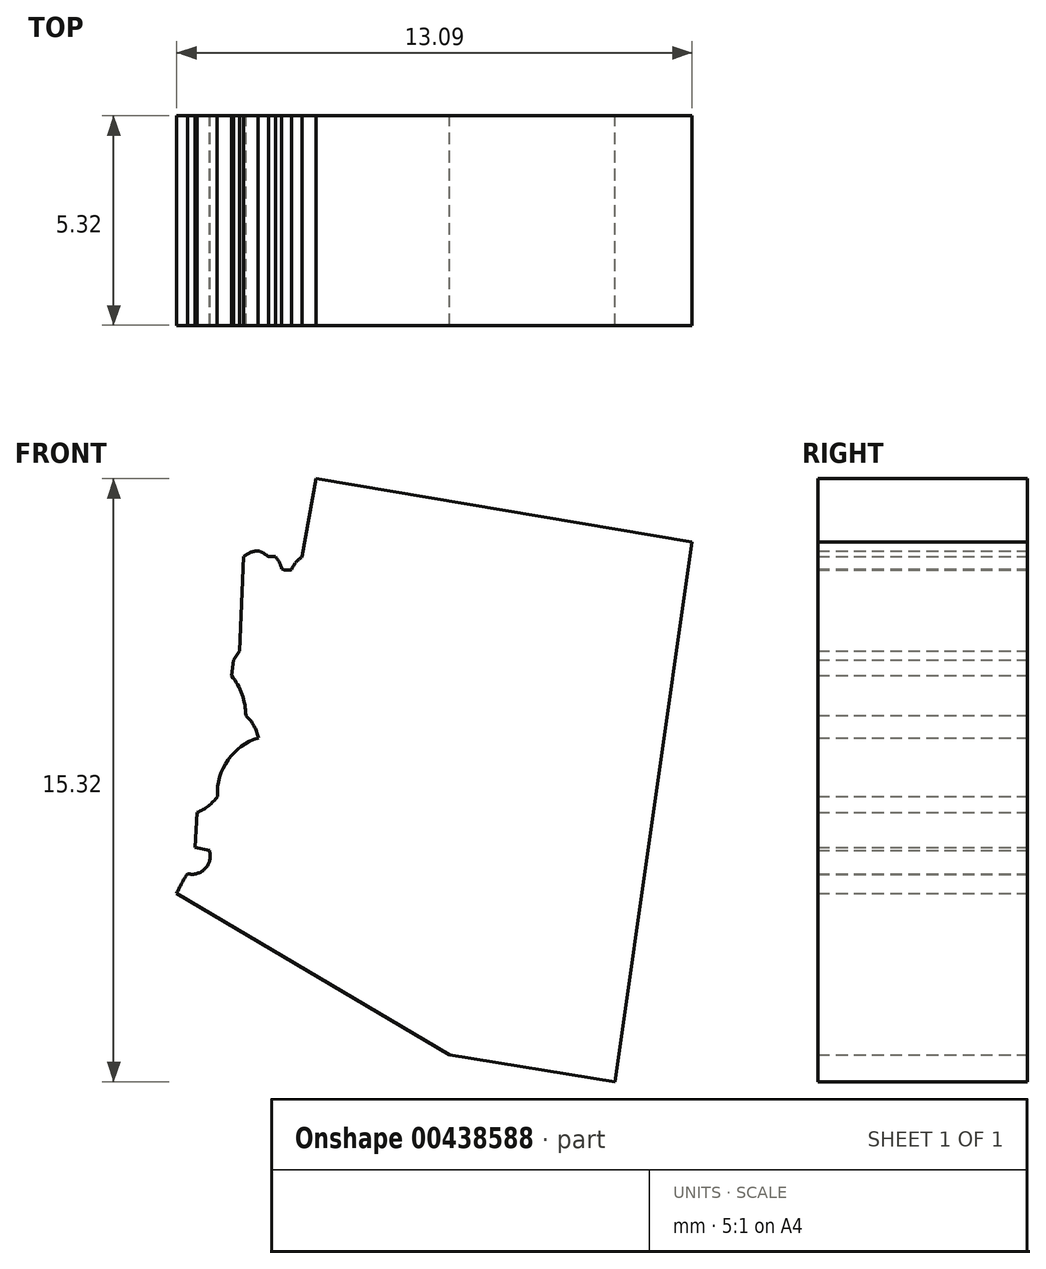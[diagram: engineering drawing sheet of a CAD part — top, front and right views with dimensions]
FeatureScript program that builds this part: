
annotation { "Feature Type Name" : "Feature", "Feature Type Description" : "" }
export const myFeature = defineFeature(function(context is Context, id is Id, definition is map)
    precondition{}
    {
        {
            var Q0;
            Q0=qCreatedBy(makeId("Front.planeOp"),FACE);
            var sketch = newSketch(context, id + "F0", { "sketchPlane" : qUnion([Q0])});
            skLineSegment(sketch, "E0", {"start": v(-91.2, -20.47) * mm, "end": v(-91.4, -20.34) * mm});
            skLineSegment(sketch, "E1", {"start": v(-91.4, -20.34) * mm, "end": v(-91.23, -19.86) * mm});
            skLineSegment(sketch, "E2", {"start": v(-91.47, -19.54) * mm, "end": v(-91.23, -19.86) * mm});
            skLineSegment(sketch, "E3", {"start": v(-91.47, -19.54) * mm, "end": v(-91.79, -19.4) * mm});
            skArc(sketch, "E4", {"start": v(-92.56, -18.19) * mm, "mid": v(-92.2, -18.82) * mm, "end": v(-91.79, -19.4) * mm});
            skArc(sketch, "E5", {"start": v(-93, -17.9) * mm, "mid": v(-92.78, -18.05) * mm, "end": v(-92.56, -18.19) * mm});
            skArc(sketch, "E6", {"start": v(-93, -17.65) * mm, "mid": v(-93, -17.78) * mm, "end": v(-93, -17.9) * mm});
            skArc(sketch, "E7", {"start": v(-93.6, -16.32) * mm, "mid": v(-93.31, -17) * mm, "end": v(-93, -17.65) * mm});
            skArc(sketch, "E8", {"start": v(-93.68, -15.85) * mm, "mid": v(-93.78, -15.74) * mm, "end": v(-93.9, -15.65) * mm});
            skArc(sketch, "E9", {"start": v(-93.68, -15.85) * mm, "mid": v(-93.64, -16.09) * mm, "end": v(-93.6, -16.32) * mm});
            skLineSegment(sketch, "E10", {"start": v(-107.57, 14.71) * mm, "end": v(-108.8, 4.95) * mm});
            skLineSegment(sketch, "E11", {"start": v(-94.83, 13.4) * mm, "end": v(-94.98, 10.98) * mm});
            skLineSegment(sketch, "E12", {"start": v(-116.05, 18.58) * mm, "end": v(-110.83, 17.66) * mm});
            skLineSegment(sketch, "E13", {"start": v(-110.83, 17.66) * mm, "end": v(-111.12, 15.24) * mm});
            skLineSegment(sketch, "E14", {"start": v(-111.12, 15.24) * mm, "end": v(-107.57, 14.71) * mm});
            skLineSegment(sketch, "E15", {"start": v(-118.36, 6.55) * mm, "end": v(-116.05, 18.58) * mm});
            skArc(sketch, "E16", {"start": v(-133.74, 23) * mm, "mid": v(-124.97, 20.48) * mm, "end": v(-116.05, 18.58) * mm});
            skLineSegment(sketch, "E17", {"start": v(-128.43, 13.81) * mm, "end": v(-126.5, 20.87) * mm});
            skLineSegment(sketch, "E18", {"start": v(-128.43, 13.81) * mm, "end": v(-120.45, 1.94) * mm});
            skLineSegment(sketch, "E19", {"start": v(-110.83, 17.66) * mm, "end": v(-109.56, 24.9) * mm});
            skLineSegment(sketch, "E20", {"start": v(-97.69, 23.43) * mm, "end": v(-109.56, 24.9) * mm});
            skLineSegment(sketch, "E21", {"start": v(-110.76, -8.77) * mm, "end": v(-108.8, 4.95) * mm});
            skLineSegment(sketch, "E22", {"start": v(-98.28, -8.44) * mm, "end": v(-97.44, 2.44) * mm});
            skLineSegment(sketch, "E23", {"start": v(-97.44, 2.44) * mm, "end": v(-97.32, 2.43) * mm});
            skLineSegment(sketch, "E24", {"start": v(-97.32, 2.43) * mm, "end": v(-97.23, 3.7) * mm});
            skLineSegment(sketch, "E25", {"start": v(-110.76, -8.77) * mm, "end": v(-109.06, -9.01) * mm});
            skLineSegment(sketch, "E26", {"start": v(-109.06, -9.01) * mm, "end": v(-108.94, -7.87) * mm});
            skLineSegment(sketch, "E27", {"start": v(-108.94, -7.87) * mm, "end": v(-105.63, -8.33) * mm});
            skLineSegment(sketch, "E28", {"start": v(-105.63, -8.33) * mm, "end": v(-105.63, -7.87) * mm});
            skLineSegment(sketch, "E29", {"start": v(-105.63, -7.87) * mm, "end": v(-98.28, -8.44) * mm});
            skLineSegment(sketch, "E30", {"start": v(-121.9, -3.98) * mm, "end": v(-114.96, -8.09) * mm});
            skLineSegment(sketch, "E31", {"start": v(-114.96, -8.09) * mm, "end": v(-110.76, -8.77) * mm});
            skArc(sketch, "E32", {"start": v(-97.32, 2.43) * mm, "mid": v(-94.44, 2.26) * mm, "end": v(-91.56, 2.2) * mm});
            skArc(sketch, "E33", {"start": v(-91.56, 2.2) * mm, "mid": v(-91.66, -0.16) * mm, "end": v(-91.72, -2.53) * mm});
            skArc(sketch, "E34", {"start": v(-126.53, 38.65) * mm, "mid": v(-104.72, 33.96) * mm, "end": v(-82.45, 32.53) * mm});
            skLineSegment(sketch, "E35", {"start": v(-97.69, 23.43) * mm, "end": v(-96.93, 33.08) * mm});
            skLineSegment(sketch, "E36", {"start": v(-98.07, 18.57) * mm, "end": v(-88.38, 18.08) * mm});
            skLineSegment(sketch, "E37", {"start": v(-94.98, 10.98) * mm, "end": v(-82.57, 10.6) * mm});
            skArc(sketch, "E38", {"start": v(-84.8, 19.22) * mm, "mid": v(-80.14, 19.27) * mm, "end": v(-75.47, 19.43) * mm});
            skArc(sketch, "E39", {"start": v(-83.28, 12.1) * mm, "mid": v(-79.64, 12.16) * mm, "end": v(-76, 12.3) * mm});
            skArc(sketch, "E40", {"start": v(-74.23, 17.12) * mm, "mid": v(-71.76, 17.15) * mm, "end": v(-69.3, 17.4) * mm});
            skLineSegment(sketch, "E41", {"start": v(-67.28, 15.71) * mm, "end": v(-63.63, 16.12) * mm});
            skLineSegment(sketch, "E42", {"start": v(-63.63, 16.12) * mm, "end": v(-62.92, 9.59) * mm});
            skLineSegment(sketch, "E43", {"start": v(-63.62, 15.96) * mm, "end": v(-61.24, 16.34) * mm});
            skLineSegment(sketch, "E44", {"start": v(-54.85, 18.69) * mm, "end": v(-54.78, 18) * mm});
            skLineSegment(sketch, "E45", {"start": v(-54.78, 18) * mm, "end": v(-47.02, 19.57) * mm});
            skLineSegment(sketch, "E46", {"start": v(-81.2, 3.21) * mm, "end": v(-81.2, 2.02) * mm});
            skLineSegment(sketch, "E47", {"start": v(-81.2, 2.02) * mm, "end": v(-72.53, 2.3) * mm});
            skArc(sketch, "E48", {"start": v(-81.2, 3.21) * mm, "mid": v(-81.15, 5.87) * mm, "end": v(-81.29, 8.53) * mm});
            skArc(sketch, "E49", {"start": v(-117.53, 36.3) * mm, "mid": v(-118.42, 32.77) * mm, "end": v(-119.02, 29.18) * mm});
            skArc(sketch, "E50", {"start": v(-68.32, 3.05) * mm, "mid": v(-56.66, 4.2) * mm, "end": v(-45.14, 6.29) * mm});
            skLineSegment(sketch, "E51", {"start": v(-71.32, 2.46) * mm, "end": v(-68.36, 2.6) * mm});
            skLineSegment(sketch, "E52", {"start": v(-68.36, 2.6) * mm, "end": v(-68.32, 3.05) * mm});
            skArc(sketch, "E53", {"start": v(-72.5, -1.3) * mm, "mid": v(-65.46, -0.82) * mm, "end": v(-58.46, 0.03) * mm});
            skLineSegment(sketch, "E54", {"start": v(-79.86, -6.45) * mm, "end": v(-73.99, -6.34) * mm});
            skLineSegment(sketch, "E55", {"start": v(-120.45, 1.94) * mm, "end": v(-120.3, 2.17) * mm});
            skLineSegment(sketch, "E56", {"start": v(-120.3, 2.17) * mm, "end": v(-120.2, 4.57) * mm});
            skArc(sketch, "E57", {"start": v(-119.83, 4.72) * mm, "mid": v(-120.02, 4.67) * mm, "end": v(-120.2, 4.57) * mm});
            skArc(sketch, "E58", {"start": v(-119.56, 4.57) * mm, "mid": v(-119.69, 4.66) * mm, "end": v(-119.83, 4.72) * mm});
            skArc(sketch, "E59", {"start": v(-119.38, 4.57) * mm, "mid": v(-119.47, 4.57) * mm, "end": v(-119.56, 4.57) * mm});
            skArc(sketch, "E60", {"start": v(-118.7, 4.57) * mm, "mid": v(-118.87, 4.42) * mm, "end": v(-118.98, 4.24) * mm});
            skArc(sketch, "E61", {"start": v(-119.22, 4.26) * mm, "mid": v(-119.28, 4.42) * mm, "end": v(-119.38, 4.57) * mm});
            skArc(sketch, "E62", {"start": v(-119.22, 4.26) * mm, "mid": v(-119.1, 4.22) * mm, "end": v(-118.98, 4.24) * mm});
            skLineSegment(sketch, "E63", {"start": v(-118.7, 4.57) * mm, "end": v(-118.36, 6.55) * mm});
            skArc(sketch, "E64", {"start": v(-126.62, -2.8) * mm, "mid": v(-124.12, -3.18) * mm, "end": v(-121.62, -3.49) * mm});
            skArc(sketch, "E65", {"start": v(-121.62, -3.49) * mm, "mid": v(-121.76, -3.73) * mm, "end": v(-121.9, -3.98) * mm});
            skLineSegment(sketch, "E66", {"start": v(-126.67, -1.34) * mm, "end": v(-126.62, -2.8) * mm});
            skLineSegment(sketch, "E67", {"start": v(-126.67, -1.34) * mm, "end": v(-127.1, -0.55) * mm});
            skLineSegment(sketch, "E68", {"start": v(-127.1, -0.55) * mm, "end": v(-127.33, -0.33) * mm});
            skLineSegment(sketch, "E69", {"start": v(-127.33, -0.33) * mm, "end": v(-127.8, 0.37) * mm});
            skLineSegment(sketch, "E70", {"start": v(-127.8, 0.37) * mm, "end": v(-128.45, 0.48) * mm});
            skLineSegment(sketch, "E71", {"start": v(-128.45, 0.48) * mm, "end": v(-128.45, 0.61) * mm});
            skLineSegment(sketch, "E72", {"start": v(-128.45, 0.61) * mm, "end": v(-128.35, 0.68) * mm});
            skLineSegment(sketch, "E73", {"start": v(-128.35, 0.68) * mm, "end": v(-128.39, 1) * mm});
            skLineSegment(sketch, "E74", {"start": v(-128.39, 1) * mm, "end": v(-128.54, 1.24) * mm});
            skLineSegment(sketch, "E75", {"start": v(-128.54, 1.24) * mm, "end": v(-129.08, 1.34) * mm});
            skLineSegment(sketch, "E76", {"start": v(-129.08, 1.34) * mm, "end": v(-129.48, 1.55) * mm});
            skLineSegment(sketch, "E77", {"start": v(-129.48, 1.55) * mm, "end": v(-129.9, 2.3) * mm});
            skLineSegment(sketch, "E78", {"start": v(-129.9, 2.3) * mm, "end": v(-130.24, 2.7) * mm});
            skLineSegment(sketch, "E79", {"start": v(-130.24, 2.7) * mm, "end": v(-130.64, 2.74) * mm});
            skLineSegment(sketch, "E80", {"start": v(-130.64, 2.74) * mm, "end": v(-131.5, 3.16) * mm});
            skLineSegment(sketch, "E81", {"start": v(-131.5, 3.16) * mm, "end": v(-131.93, 3.2) * mm});
            skLineSegment(sketch, "E82", {"start": v(-131.93, 3.2) * mm, "end": v(-132.23, 3.5) * mm});
            skLineSegment(sketch, "E83", {"start": v(-132.23, 3.5) * mm, "end": v(-131.93, 4.74) * mm});
            skLineSegment(sketch, "E84", {"start": v(-131.93, 4.74) * mm, "end": v(-131.93, 4.98) * mm});
            skLineSegment(sketch, "E85", {"start": v(-131.93, 4.98) * mm, "end": v(-132.1, 5.14) * mm});
            skLineSegment(sketch, "E86", {"start": v(-132.1, 5.14) * mm, "end": v(-132.1, 5.4) * mm});
            skLineSegment(sketch, "E87", {"start": v(-132.1, 5.4) * mm, "end": v(-132.68, 6.4) * mm});
            skLineSegment(sketch, "E88", {"start": v(-132.68, 6.4) * mm, "end": v(-133.14, 7.78) * mm});
            skLineSegment(sketch, "E89", {"start": v(-133.14, 7.78) * mm, "end": v(-133.45, 8.25) * mm});
            skLineSegment(sketch, "E90", {"start": v(-133.45, 8.25) * mm, "end": v(-133.55, 8.54) * mm});
            skLineSegment(sketch, "E91", {"start": v(-133.55, 8.54) * mm, "end": v(-133.49, 9.04) * mm});
            skArc(sketch, "E92", {"start": v(-133.49, 9.04) * mm, "mid": v(-133.08, 9.38) * mm, "end": v(-133.11, 9.91) * mm});
            skLineSegment(sketch, "E93", {"start": v(-133.11, 9.91) * mm, "end": v(-133.38, 9.97) * mm});
            skLineSegment(sketch, "E94", {"start": v(-133.38, 9.97) * mm, "end": v(-133.86, 10.65) * mm});
            skLineSegment(sketch, "E95", {"start": v(-133.86, 10.65) * mm, "end": v(-133.86, 11.63) * mm});
            skLineSegment(sketch, "E96", {"start": v(-133.86, 11.63) * mm, "end": v(-133.7, 12.33) * mm});
            skLineSegment(sketch, "E97", {"start": v(-133.7, 12.33) * mm, "end": v(-134.3, 13.03) * mm});
            skLineSegment(sketch, "E98", {"start": v(-134.3, 13.03) * mm, "end": v(-134.3, 13.29) * mm});
            skArc(sketch, "E99", {"start": v(-134.3, 13.29) * mm, "mid": v(-134.27, 13.76) * mm, "end": v(-134.42, 14.22) * mm});
            skLineSegment(sketch, "E100", {"start": v(-135.13, 15.58) * mm, "end": v(-134.42, 14.22) * mm});
            skLineSegment(sketch, "E101", {"start": v(-135.13, 15.58) * mm, "end": v(-135.01, 16) * mm});
            skLineSegment(sketch, "E102", {"start": v(-135.01, 16) * mm, "end": v(-134.96, 16.65) * mm});
            skLineSegment(sketch, "E103", {"start": v(-134.96, 16.65) * mm, "end": v(-134.76, 16.97) * mm});
            skLineSegment(sketch, "E104", {"start": v(-134.76, 16.97) * mm, "end": v(-134.73, 17.77) * mm});
            skLineSegment(sketch, "E105", {"start": v(-134.73, 17.77) * mm, "end": v(-135.01, 18.6) * mm});
            skLineSegment(sketch, "E106", {"start": v(-135.01, 18.6) * mm, "end": v(-135.32, 19.01) * mm});
            skLineSegment(sketch, "E107", {"start": v(-135.32, 19.01) * mm, "end": v(-135.07, 19.88) * mm});
            skLineSegment(sketch, "E108", {"start": v(-135.07, 19.88) * mm, "end": v(-134.88, 19.94) * mm});
            skLineSegment(sketch, "E109", {"start": v(-134.88, 19.94) * mm, "end": v(-134.84, 20.1) * mm});
            skLineSegment(sketch, "E110", {"start": v(-134.84, 20.1) * mm, "end": v(-134.5, 20.4) * mm});
            skLineSegment(sketch, "E111", {"start": v(-134.5, 20.4) * mm, "end": v(-133.92, 21.67) * mm});
            skLineSegment(sketch, "E112", {"start": v(-133.92, 21.67) * mm, "end": v(-133.92, 22.51) * mm});
            skLineSegment(sketch, "E113", {"start": v(-133.92, 22.51) * mm, "end": v(-133.74, 23) * mm});
            skArc(sketch, "E114", {"start": v(-120.14, 0.53) * mm, "mid": v(-120.23, 1.07) * mm, "end": v(-120.5, 1.55) * mm});
            skLineSegment(sketch, "E115", {"start": v(-120.45, 1.94) * mm, "end": v(-120.5, 1.55) * mm});
            skArc(sketch, "E116", {"start": v(-121.62, -3.49) * mm, "mid": v(-121.17, -3.36) * mm, "end": v(-121.06, -2.9) * mm});
            skLineSegment(sketch, "E117", {"start": v(-121.06, -2.9) * mm, "end": v(-121.42, -2.81) * mm});
            skLineSegment(sketch, "E118", {"start": v(-121.42, -2.81) * mm, "end": v(-121.38, -1.93) * mm});
            skArc(sketch, "E119", {"start": v(-121.38, -1.93) * mm, "mid": v(-121.09, -1.76) * mm, "end": v(-120.86, -1.52) * mm});
            skArc(sketch, "E120", {"start": v(-119.82, -0.04) * mm, "mid": v(-120.6, -0.6) * mm, "end": v(-120.86, -1.52) * mm});
            skArc(sketch, "E121", {"start": v(-119.82, -0.04) * mm, "mid": v(-119.93, 0.27) * mm, "end": v(-120.14, 0.53) * mm});
            skLineSegment(sketch, "E122", {"start": v(-121.32, 19.62) * mm, "end": v(-120.3, 24) * mm});
            skLineSegment(sketch, "E123", {"start": v(-120.3, 24) * mm, "end": v(-119.9, 24.82) * mm});
            skLineSegment(sketch, "E124", {"start": v(-119.9, 24.82) * mm, "end": v(-120.03, 25.08) * mm});
            skLineSegment(sketch, "E125", {"start": v(-120.03, 25.08) * mm, "end": v(-120.34, 25.15) * mm});
            skLineSegment(sketch, "E126", {"start": v(-119.02, 29.18) * mm, "end": v(-122.2, 30.03) * mm});
            skLineSegment(sketch, "E127", {"start": v(-122.2, 30.03) * mm, "end": v(-123.9, 30.03) * mm});
            skLineSegment(sketch, "E128", {"start": v(-123.9, 30.03) * mm, "end": v(-123.9, 30.16) * mm});
            skLineSegment(sketch, "E129", {"start": v(-123.9, 30.16) * mm, "end": v(-124.46, 29.94) * mm});
            skLineSegment(sketch, "E130", {"start": v(-124.46, 29.94) * mm, "end": v(-124.94, 29.94) * mm});
            skLineSegment(sketch, "E131", {"start": v(-124.94, 29.94) * mm, "end": v(-125.28, 30.18) * mm});
            skLineSegment(sketch, "E132", {"start": v(-125.28, 30.18) * mm, "end": v(-125.42, 30.1) * mm});
            skLineSegment(sketch, "E133", {"start": v(-125.42, 30.1) * mm, "end": v(-125.92, 30.1) * mm});
            skArc(sketch, "E134", {"start": v(-125.92, 30.1) * mm, "mid": v(-126.57, 30.42) * mm, "end": v(-127.28, 30.62) * mm});
            skArc(sketch, "E135", {"start": v(-128.83, 30.92) * mm, "mid": v(-128.11, 30.47) * mm, "end": v(-127.28, 30.62) * mm});
            skArc(sketch, "E136", {"start": v(-128.83, 30.92) * mm, "mid": v(-128.7, 31.65) * mm, "end": v(-129.02, 32.33) * mm});
            skLineSegment(sketch, "E137", {"start": v(-129.02, 32.33) * mm, "end": v(-129.43, 32.33) * mm});
            skLineSegment(sketch, "E138", {"start": v(-129.43, 32.33) * mm, "end": v(-129.43, 32.63) * mm});
            skLineSegment(sketch, "E139", {"start": v(-129.43, 32.63) * mm, "end": v(-129.68, 32.63) * mm});
            skLineSegment(sketch, "E140", {"start": v(-129.68, 32.63) * mm, "end": v(-129.98, 32.86) * mm});
            skLineSegment(sketch, "E141", {"start": v(-129.98, 32.86) * mm, "end": v(-130.16, 32.79) * mm});
            skLineSegment(sketch, "E142", {"start": v(-130.16, 32.79) * mm, "end": v(-130.42, 33.08) * mm});
            skLineSegment(sketch, "E143", {"start": v(-130.42, 33.08) * mm, "end": v(-130.38, 33.4) * mm});
            skLineSegment(sketch, "E144", {"start": v(-130.38, 33.4) * mm, "end": v(-130.1, 33.4) * mm});
            skLineSegment(sketch, "E145", {"start": v(-130.1, 33.4) * mm, "end": v(-129.92, 33.88) * mm});
            skLineSegment(sketch, "E146", {"start": v(-129.92, 33.88) * mm, "end": v(-130.2, 34.03) * mm});
            skLineSegment(sketch, "E147", {"start": v(-130.2, 34.03) * mm, "end": v(-130.15, 34.42) * mm});
            skLineSegment(sketch, "E148", {"start": v(-130.15, 34.42) * mm, "end": v(-129.65, 34.47) * mm});
            skLineSegment(sketch, "E149", {"start": v(-129.65, 34.47) * mm, "end": v(-130, 34.82) * mm});
            skLineSegment(sketch, "E150", {"start": v(-130, 34.82) * mm, "end": v(-130.15, 35.59) * mm});
            skLineSegment(sketch, "E151", {"start": v(-130.15, 35.59) * mm, "end": v(-130.08, 35.84) * mm});
            skLineSegment(sketch, "E152", {"start": v(-130.08, 35.84) * mm, "end": v(-130.08, 36.79) * mm});
            skLineSegment(sketch, "E153", {"start": v(-130.08, 36.79) * mm, "end": v(-130.26, 37.1) * mm});
            skLineSegment(sketch, "E154", {"start": v(-130.26, 37.1) * mm, "end": v(-130.26, 37.29) * mm});
            skLineSegment(sketch, "E155", {"start": v(-130.26, 37.29) * mm, "end": v(-130.06, 38.16) * mm});
            skLineSegment(sketch, "E156", {"start": v(-130.06, 38.16) * mm, "end": v(-129.8, 38.13) * mm});
            skArc(sketch, "E157", {"start": v(-129.8, 38.13) * mm, "mid": v(-128.59, 37.18) * mm, "end": v(-127.1, 36.73) * mm});
            skArc(sketch, "E158", {"start": v(-126.56, 36.06) * mm, "mid": v(-126.72, 36.48) * mm, "end": v(-127.1, 36.73) * mm});
            skArc(sketch, "E159", {"start": v(-126.43, 36.88) * mm, "mid": v(-126.52, 36.55) * mm, "end": v(-126.36, 36.24) * mm});
            skArc(sketch, "E160", {"start": v(-126.32, 37.66) * mm, "mid": v(-126.5, 37.29) * mm, "end": v(-126.43, 36.88) * mm});
            skLineSegment(sketch, "E161", {"start": v(-126.36, 36.24) * mm, "end": v(-126.36, 36.05) * mm});
            skLineSegment(sketch, "E162", {"start": v(-126.36, 36.05) * mm, "end": v(-126.56, 36.06) * mm});
            skLineSegment(sketch, "E163", {"start": v(-126.32, 37.66) * mm, "end": v(-126.66, 38.47) * mm});
            skLineSegment(sketch, "E164", {"start": v(-126.66, 38.47) * mm, "end": v(-126.6, 38.65) * mm});
            skLineSegment(sketch, "E165", {"start": v(-126.6, 38.65) * mm, "end": v(-126.53, 38.65) * mm});
            skArc(sketch, "E166", {"start": v(-119.58, 26.37) * mm, "mid": v(-120.13, 25.87) * mm, "end": v(-120.34, 25.15) * mm});
            skArc(sketch, "E167", {"start": v(-119.58, 26.37) * mm, "mid": v(-119.48, 26.58) * mm, "end": v(-119.45, 26.82) * mm});
            skArc(sketch, "E168", {"start": v(-118.46, 28.04) * mm, "mid": v(-118.98, 27.45) * mm, "end": v(-119.45, 26.82) * mm});
            skArc(sketch, "E169", {"start": v(-119.02, 29.18) * mm, "mid": v(-118.85, 28.78) * mm, "end": v(-118.52, 28.5) * mm});
            skLineSegment(sketch, "E170", {"start": v(-118.52, 28.5) * mm, "end": v(-118.46, 28.04) * mm});
            skArc(sketch, "E171", {"start": v(-54.85, 18.69) * mm, "mid": v(-54.12, 19.4) * mm, "end": v(-53.56, 20.24) * mm});
            skArc(sketch, "E172", {"start": v(-54.08, 21.34) * mm, "mid": v(-53.98, 21.07) * mm, "end": v(-53.88, 20.8) * mm});
            skArc(sketch, "E173", {"start": v(-53.56, 20.24) * mm, "mid": v(-53.62, 20.57) * mm, "end": v(-53.88, 20.8) * mm});
            skArc(sketch, "E174", {"start": v(-51.74, 21.88) * mm, "mid": v(-52.95, 21.8) * mm, "end": v(-54.08, 21.34) * mm});
            skArc(sketch, "E175", {"start": v(-51.74, 21.88) * mm, "mid": v(-51.47, 21.77) * mm, "end": v(-51.21, 21.88) * mm});
            skArc(sketch, "E176", {"start": v(-50.32, 22.04) * mm, "mid": v(-50.78, 22.04) * mm, "end": v(-51.21, 21.88) * mm});
            skArc(sketch, "E177", {"start": v(-50.32, 22.04) * mm, "mid": v(-49.98, 22.42) * mm, "end": v(-49.67, 22.82) * mm});
            skArc(sketch, "E178", {"start": v(-49.67, 22.82) * mm, "mid": v(-49.26, 22.99) * mm, "end": v(-49.4, 23.4) * mm});
            skArc(sketch, "E179", {"start": v(-49.27, 24) * mm, "mid": v(-49.38, 23.71) * mm, "end": v(-49.4, 23.4) * mm});
            skArc(sketch, "E180", {"start": v(-49.47, 24.8) * mm, "mid": v(-49.77, 24.3) * mm, "end": v(-49.27, 24) * mm});
            skArc(sketch, "E181", {"start": v(-49.47, 24.8) * mm, "mid": v(-49.29, 24.98) * mm, "end": v(-49.12, 25.18) * mm});
            skArc(sketch, "E182", {"start": v(-47.8, 26.87) * mm, "mid": v(-48.56, 26.1) * mm, "end": v(-49.12, 25.18) * mm});
            skArc(sketch, "E183", {"start": v(-47.02, 19.57) * mm, "mid": v(-46.74, 19.36) * mm, "end": v(-46.4, 19.26) * mm});
            skArc(sketch, "E184", {"start": v(-46.4, 19.26) * mm, "mid": v(-46.25, 18.82) * mm, "end": v(-45.96, 18.47) * mm});
            skArc(sketch, "E185", {"start": v(-45.48, 18.25) * mm, "mid": v(-45.68, 18.45) * mm, "end": v(-45.96, 18.47) * mm});
            skLineSegment(sketch, "E186", {"start": v(-45.48, 18.25) * mm, "end": v(-43.84, 17.74) * mm});
            skLineSegment(sketch, "E187", {"start": v(-43.84, 17.74) * mm, "end": v(-43.84, 16.86) * mm});
            skArc(sketch, "E188", {"start": v(-43.84, 16.86) * mm, "mid": v(-42.15, 17.41) * mm, "end": v(-40.77, 18.53) * mm});
            skLineSegment(sketch, "E189", {"start": v(-40.77, 18.53) * mm, "end": v(-41.18, 18.7) * mm});
            skArc(sketch, "E190", {"start": v(-42.5, 17.87) * mm, "mid": v(-41.77, 18.18) * mm, "end": v(-41.18, 18.7) * mm});
            skArc(sketch, "E191", {"start": v(-42.93, 17.87) * mm, "mid": v(-42.71, 17.83) * mm, "end": v(-42.5, 17.87) * mm});
            skLineSegment(sketch, "E192", {"start": v(-42.93, 17.87) * mm, "end": v(-43.43, 17.43) * mm});
            skLineSegment(sketch, "E193", {"start": v(-43.43, 17.43) * mm, "end": v(-43.62, 17.38) * mm});
            skLineSegment(sketch, "E194", {"start": v(-43.62, 17.38) * mm, "end": v(-43.62, 17.53) * mm});
            skLineSegment(sketch, "E195", {"start": v(-43.62, 17.53) * mm, "end": v(-43.43, 17.74) * mm});
            skLineSegment(sketch, "E196", {"start": v(-43.43, 17.74) * mm, "end": v(-43.43, 17.92) * mm});
            skLineSegment(sketch, "E197", {"start": v(-43.43, 17.92) * mm, "end": v(-43.63, 18.1) * mm});
            skLineSegment(sketch, "E198", {"start": v(-43.63, 18.1) * mm, "end": v(-43.5, 18.25) * mm});
            skLineSegment(sketch, "E199", {"start": v(-43.5, 18.25) * mm, "end": v(-43.5, 19.27) * mm});
            skLineSegment(sketch, "E200", {"start": v(-43.5, 19.27) * mm, "end": v(-43.79, 20.44) * mm});
            skLineSegment(sketch, "E201", {"start": v(-43.79, 20.44) * mm, "end": v(-43.79, 22.2) * mm});
            skLineSegment(sketch, "E202", {"start": v(-43.79, 22.2) * mm, "end": v(-44.19, 24.06) * mm});
            skArc(sketch, "E203", {"start": v(-44.19, 24.06) * mm, "mid": v(-44.34, 24.2) * mm, "end": v(-44.53, 24.12) * mm});
            skArc(sketch, "E204", {"start": v(-46.48, 27.1) * mm, "mid": v(-47.15, 27.04) * mm, "end": v(-47.8, 26.87) * mm});
            skLineSegment(sketch, "E205", {"start": v(-46.48, 27.1) * mm, "end": v(-45.15, 27.46) * mm});
            skLineSegment(sketch, "E206", {"start": v(-45.15, 27.46) * mm, "end": v(-44.73, 25.93) * mm});
            skArc(sketch, "E207", {"start": v(-44.87, 25.31) * mm, "mid": v(-44.72, 25.6) * mm, "end": v(-44.73, 25.93) * mm});
            skLineSegment(sketch, "E208", {"start": v(-44.87, 25.31) * mm, "end": v(-44.49, 24.59) * mm});
            skLineSegment(sketch, "E209", {"start": v(-44.49, 24.59) * mm, "end": v(-44.53, 24.12) * mm});
            skLineSegment(sketch, "E210", {"start": v(-133.74, 23) * mm, "end": v(-133.99, 23.5) * mm});
            skLineSegment(sketch, "E211", {"start": v(-133.99, 23.5) * mm, "end": v(-133.82, 24.17) * mm});
            skLineSegment(sketch, "E212", {"start": v(-133.82, 24.17) * mm, "end": v(-133.76, 25.13) * mm});
            skArc(sketch, "E213", {"start": v(-133.76, 25.13) * mm, "mid": v(-132.38, 27.43) * mm, "end": v(-131.4, 29.92) * mm});
            skLineSegment(sketch, "E214", {"start": v(-129.68, 32.63) * mm, "end": v(-130.39, 32.48) * mm});
            skArc(sketch, "E215", {"start": v(-131.4, 29.92) * mm, "mid": v(-130.84, 31.18) * mm, "end": v(-130.39, 32.48) * mm});
            skLineSegment(sketch, "E216", {"start": v(-88.38, 18.08) * mm, "end": v(-87.44, 17.46) * mm});
            skArc(sketch, "E217", {"start": v(-85.15, 17.16) * mm, "mid": v(-86.25, 17.64) * mm, "end": v(-87.44, 17.46) * mm});
            skArc(sketch, "E218", {"start": v(-85.15, 17.16) * mm, "mid": v(-84.96, 16.83) * mm, "end": v(-84.6, 16.73) * mm});
            skArc(sketch, "E219", {"start": v(-83.28, 12.1) * mm, "mid": v(-83.7, 14.47) * mm, "end": v(-84.6, 16.73) * mm});
            skArc(sketch, "E220", {"start": v(-83.28, 12.1) * mm, "mid": v(-83.04, 11.3) * mm, "end": v(-82.57, 10.6) * mm});
            skArc(sketch, "E221", {"start": v(-82.57, 10.6) * mm, "mid": v(-82.24, 10.36) * mm, "end": v(-81.85, 10.23) * mm});
            skArc(sketch, "E222", {"start": v(-82.01, 9.69) * mm, "mid": v(-81.77, 9.91) * mm, "end": v(-81.85, 10.23) * mm});
            skArc(sketch, "E223", {"start": v(-82.01, 9.69) * mm, "mid": v(-81.82, 9) * mm, "end": v(-81.29, 8.53) * mm});
            skLineSegment(sketch, "E224", {"start": v(-116.02, 35.96) * mm, "end": v(-116.5, 33.61) * mm});
            skLineSegment(sketch, "E225", {"start": v(-116.5, 33.61) * mm, "end": v(-116.13, 32.87) * mm});
            skLineSegment(sketch, "E226", {"start": v(-116.13, 32.87) * mm, "end": v(-116.24, 32.15) * mm});
            skArc(sketch, "E227", {"start": v(-116.24, 32.15) * mm, "mid": v(-116.03, 31.86) * mm, "end": v(-115.73, 31.68) * mm});
            skArc(sketch, "E228", {"start": v(-115.73, 31.68) * mm, "mid": v(-115.3, 30.6) * mm, "end": v(-114.4, 29.85) * mm});
            skLineSegment(sketch, "E229", {"start": v(-115.18, 27.31) * mm, "end": v(-114.4, 29.85) * mm});
            skLineSegment(sketch, "E230", {"start": v(-114.85, 27.03) * mm, "end": v(-115.18, 27.31) * mm});
            skLineSegment(sketch, "E231", {"start": v(-113.18, 24.88) * mm, "end": v(-113.72, 25.42) * mm});
            skLineSegment(sketch, "E232", {"start": v(-113.72, 25.42) * mm, "end": v(-114.14, 27.48) * mm});
            skLineSegment(sketch, "E233", {"start": v(-114.14, 27.48) * mm, "end": v(-114.85, 27.03) * mm});
            skArc(sketch, "E234", {"start": v(-113.18, 24.88) * mm, "mid": v(-113.16, 24.4) * mm, "end": v(-112.96, 23.97) * mm});
            skArc(sketch, "E235", {"start": v(-112.1, 24.07) * mm, "mid": v(-112.56, 24.25) * mm, "end": v(-112.96, 23.97) * mm});
            skArc(sketch, "E236", {"start": v(-111, 23.97) * mm, "mid": v(-111.53, 24.19) * mm, "end": v(-112.1, 24.07) * mm});
            skArc(sketch, "E237", {"start": v(-111, 23.97) * mm, "mid": v(-110.7, 24.09) * mm, "end": v(-110.59, 24.37) * mm});
            skArc(sketch, "E238", {"start": v(-110.17, 24.36) * mm, "mid": v(-110.02, 24.01) * mm, "end": v(-109.76, 23.74) * mm});
            skArc(sketch, "E239", {"start": v(-110.17, 24.36) * mm, "mid": v(-110.38, 24.42) * mm, "end": v(-110.59, 24.37) * mm});
            skArc(sketch, "E240", {"start": v(-80.77, -5.04) * mm, "mid": v(-80.77, -1.5) * mm, "end": v(-81.2, 2.02) * mm});
            skLineSegment(sketch, "E241", {"start": v(-80.77, -5.04) * mm, "end": v(-79.92, -5.19) * mm});
            skLineSegment(sketch, "E242", {"start": v(-79.92, -5.19) * mm, "end": v(-79.86, -6.45) * mm});
            skLineSegment(sketch, "E243", {"start": v(-79.86, -6.45) * mm, "end": v(-79.81, -9) * mm});
            skLineSegment(sketch, "E244", {"start": v(-91.2, -20.47) * mm, "end": v(-91.2, -20.9) * mm});
            skArc(sketch, "E245", {"start": v(-91.2, -20.9) * mm, "mid": v(-91.1, -21.18) * mm, "end": v(-90.86, -21.34) * mm});
            skArc(sketch, "E246", {"start": v(-90.86, -21.34) * mm, "mid": v(-90.74, -21.92) * mm, "end": v(-90.56, -22.48) * mm});
            skLineSegment(sketch, "E247", {"start": v(-86.64, -23.67) * mm, "end": v(-86.95, -23.9) * mm});
            skLineSegment(sketch, "E248", {"start": v(-86.95, -23.9) * mm, "end": v(-87.48, -23.49) * mm});
            skLineSegment(sketch, "E249", {"start": v(-87.48, -23.49) * mm, "end": v(-88.1, -23.4) * mm});
            skLineSegment(sketch, "E250", {"start": v(-88.1, -23.4) * mm, "end": v(-88.33, -23.46) * mm});
            skLineSegment(sketch, "E251", {"start": v(-88.33, -23.46) * mm, "end": v(-88.53, -23.47) * mm});
            skLineSegment(sketch, "E252", {"start": v(-88.53, -23.47) * mm, "end": v(-89, -23.04) * mm});
            skLineSegment(sketch, "E253", {"start": v(-89, -23.04) * mm, "end": v(-90.56, -22.48) * mm});
            skLineSegment(sketch, "E254", {"start": v(-71.55, 1.14) * mm, "end": v(-72.8, 1.14) * mm});
            skArc(sketch, "E255", {"start": v(-72.32, 1.72) * mm, "mid": v(-72.61, 1.47) * mm, "end": v(-72.8, 1.14) * mm});
            skArc(sketch, "E256", {"start": v(-72.32, 1.72) * mm, "mid": v(-72.35, 2.04) * mm, "end": v(-72.53, 2.3) * mm});
            skLineSegment(sketch, "E257", {"start": v(-84.6, 16.73) * mm, "end": v(-84.9, 17.32) * mm});
            skLineSegment(sketch, "E258", {"start": v(-84.9, 17.32) * mm, "end": v(-84.6, 18.44) * mm});
            skArc(sketch, "E259", {"start": v(-84.8, 19.22) * mm, "mid": v(-84.82, 18.8) * mm, "end": v(-84.6, 18.44) * mm});
            skArc(sketch, "E260", {"start": v(-97.5, 25.8) * mm, "mid": v(-91.18, 25.35) * mm, "end": v(-84.85, 25.13) * mm});
            skArc(sketch, "E261", {"start": v(-84.6, 19.22) * mm, "mid": v(-84.53, 21.43) * mm, "end": v(-84.57, 23.64) * mm});
            skArc(sketch, "E262", {"start": v(-85.19, 24.47) * mm, "mid": v(-84.9, 24.73) * mm, "end": v(-84.85, 25.13) * mm});
            skArc(sketch, "E263", {"start": v(-85.19, 24.47) * mm, "mid": v(-84.98, 23.98) * mm, "end": v(-84.57, 23.64) * mm});
            skArc(sketch, "E264", {"start": v(-85.64, 31.73) * mm, "mid": v(-85.63, 32.15) * mm, "end": v(-85.81, 32.53) * mm});
            skArc(sketch, "E265", {"start": v(-85.64, 31.73) * mm, "mid": v(-85.67, 30.6) * mm, "end": v(-85.37, 29.5) * mm});
            skLineSegment(sketch, "E266", {"start": v(-85.37, 29.5) * mm, "end": v(-84.92, 26.25) * mm});
            skLineSegment(sketch, "E267", {"start": v(-84.92, 26.25) * mm, "end": v(-84.85, 25.13) * mm});
            skArc(sketch, "E268", {"start": v(-79.3, -9.99) * mm, "mid": v(-79.42, -9.42) * mm, "end": v(-79.81, -9) * mm});
            skArc(sketch, "E269", {"start": v(-79.1, -12.52) * mm, "mid": v(-78.7, -11.22) * mm, "end": v(-79.3, -9.99) * mm});
            skArc(sketch, "E270", {"start": v(-79.3, -14.15) * mm, "mid": v(-79.05, -13.35) * mm, "end": v(-79.1, -12.52) * mm});
            skLineSegment(sketch, "E271", {"start": v(-79.3, -14.15) * mm, "end": v(-79.2, -14.64) * mm});
            skLineSegment(sketch, "E272", {"start": v(-79.2, -14.64) * mm, "end": v(-81.04, -15.3) * mm});
            skArc(sketch, "E273", {"start": v(-83.77, -17.32) * mm, "mid": v(-82.28, -16.48) * mm, "end": v(-81.04, -15.3) * mm});
            skArc(sketch, "E274", {"start": v(-83.77, -17.32) * mm, "mid": v(-84.63, -17.81) * mm, "end": v(-85.43, -18.38) * mm});
            skArc(sketch, "E275", {"start": v(-86.64, -19.53) * mm, "mid": v(-86.98, -21.6) * mm, "end": v(-86.64, -23.67) * mm});
            skLineSegment(sketch, "E276", {"start": v(-85.43, -18.38) * mm, "end": v(-85.8, -18.38) * mm});
            skLineSegment(sketch, "E277", {"start": v(-85.8, -18.38) * mm, "end": v(-86.26, -19.06) * mm});
            skLineSegment(sketch, "E278", {"start": v(-86.26, -19.06) * mm, "end": v(-86.7, -19.1) * mm});
            skLineSegment(sketch, "E279", {"start": v(-86.7, -19.1) * mm, "end": v(-86.82, -19.32) * mm});
            skLineSegment(sketch, "E280", {"start": v(-86.82, -19.32) * mm, "end": v(-86.64, -19.53) * mm});
            skLineSegment(sketch, "E281", {"start": v(-93.9, -15.65) * mm, "end": v(-93.9, -15.49) * mm});
            skLineSegment(sketch, "E282", {"start": v(-93.9, -15.49) * mm, "end": v(-94.81, -14.6) * mm});
            skLineSegment(sketch, "E283", {"start": v(-94.81, -14.6) * mm, "end": v(-94.82, -14.42) * mm});
            skLineSegment(sketch, "E284", {"start": v(-94.82, -14.42) * mm, "end": v(-95.13, -14.18) * mm});
            skLineSegment(sketch, "E285", {"start": v(-95.13, -14.18) * mm, "end": v(-96.74, -13.98) * mm});
            skLineSegment(sketch, "E286", {"start": v(-96.74, -13.98) * mm, "end": v(-97.09, -13.71) * mm});
            skLineSegment(sketch, "E287", {"start": v(-97.09, -13.71) * mm, "end": v(-98.02, -14.08) * mm});
            skLineSegment(sketch, "E288", {"start": v(-98.02, -14.08) * mm, "end": v(-98.34, -14.48) * mm});
            skLineSegment(sketch, "E289", {"start": v(-98.34, -14.48) * mm, "end": v(-98.38, -14.79) * mm});
            skLineSegment(sketch, "E290", {"start": v(-98.38, -14.79) * mm, "end": v(-99.07, -15.73) * mm});
            skLineSegment(sketch, "E291", {"start": v(-99.07, -15.73) * mm, "end": v(-100.11, -15.31) * mm});
            skLineSegment(sketch, "E292", {"start": v(-100.11, -15.31) * mm, "end": v(-100.36, -14.98) * mm});
            skLineSegment(sketch, "E293", {"start": v(-100.36, -14.98) * mm, "end": v(-100.94, -14.72) * mm});
            skLineSegment(sketch, "E294", {"start": v(-100.94, -14.72) * mm, "end": v(-101.7, -13.91) * mm});
            skLineSegment(sketch, "E295", {"start": v(-101.7, -13.91) * mm, "end": v(-101.96, -13.47) * mm});
            skLineSegment(sketch, "E296", {"start": v(-101.96, -13.47) * mm, "end": v(-101.98, -12.45) * mm});
            skLineSegment(sketch, "E297", {"start": v(-101.98, -12.45) * mm, "end": v(-102.32, -11.83) * mm});
            skLineSegment(sketch, "E298", {"start": v(-102.32, -11.83) * mm, "end": v(-102.39, -11.46) * mm});
            skLineSegment(sketch, "E299", {"start": v(-102.39, -11.46) * mm, "end": v(-102.68, -11.17) * mm});
            skLineSegment(sketch, "E300", {"start": v(-102.68, -11.17) * mm, "end": v(-103.2, -10.9) * mm});
            skLineSegment(sketch, "E301", {"start": v(-103.2, -10.9) * mm, "end": v(-104.18, -9.78) * mm});
            skLineSegment(sketch, "E302", {"start": v(-104.18, -9.78) * mm, "end": v(-104.3, -9.45) * mm});
            skLineSegment(sketch, "E303", {"start": v(-104.3, -9.45) * mm, "end": v(-104.78, -9.24) * mm});
            skLineSegment(sketch, "E304", {"start": v(-104.78, -9.24) * mm, "end": v(-104.96, -8.77) * mm});
            skLineSegment(sketch, "E305", {"start": v(-104.96, -8.77) * mm, "end": v(-105.33, -8.4) * mm});
            skLineSegment(sketch, "E306", {"start": v(-105.33, -8.4) * mm, "end": v(-105.63, -8.33) * mm});
            skArc(sketch, "E307", {"start": v(-63.21, -0.59) * mm, "mid": v(-62.45, -3.44) * mm, "end": v(-61.6, -6.26) * mm});
            skLineSegment(sketch, "E308", {"start": v(-68.2, -1.05) * mm, "end": v(-68.31, -8.82) * mm});
            skLineSegment(sketch, "E309", {"start": v(-68.31, -8.82) * mm, "end": v(-67.87, -12.38) * mm});
            skLineSegment(sketch, "E310", {"start": v(-67.87, -12.38) * mm, "end": v(-67.49, -12.34) * mm});
            skLineSegment(sketch, "E311", {"start": v(-67.49, -12.34) * mm, "end": v(-67.2, -11.6) * mm});
            skLineSegment(sketch, "E312", {"start": v(-67.2, -11.6) * mm, "end": v(-66.97, -11.7) * mm});
            skLineSegment(sketch, "E313", {"start": v(-66.97, -11.7) * mm, "end": v(-66.6, -12.37) * mm});
            skLineSegment(sketch, "E314", {"start": v(-66.6, -12.37) * mm, "end": v(-66.94, -12.6) * mm});
            skLineSegment(sketch, "E315", {"start": v(-66.94, -12.6) * mm, "end": v(-66.68, -12.65) * mm});
            skLineSegment(sketch, "E316", {"start": v(-66.68, -12.65) * mm, "end": v(-65.91, -12.35) * mm});
            skLineSegment(sketch, "E317", {"start": v(-65.91, -12.35) * mm, "end": v(-65.5, -12.28) * mm});
            skLineSegment(sketch, "E318", {"start": v(-65.5, -12.28) * mm, "end": v(-64.87, -12.09) * mm});
            skLineSegment(sketch, "E319", {"start": v(-64.87, -12.09) * mm, "end": v(-63.78, -11.97) * mm});
            skLineSegment(sketch, "E320", {"start": v(-63.78, -11.97) * mm, "end": v(-61.96, -12.62) * mm});
            skLineSegment(sketch, "E321", {"start": v(-61.96, -12.62) * mm, "end": v(-61.77, -12.85) * mm});
            skLineSegment(sketch, "E322", {"start": v(-61.77, -12.85) * mm, "end": v(-61.64, -12.85) * mm});
            skLineSegment(sketch, "E323", {"start": v(-61.64, -12.85) * mm, "end": v(-61.4, -13.04) * mm});
            skLineSegment(sketch, "E324", {"start": v(-61.4, -13.04) * mm, "end": v(-61.29, -13.42) * mm});
            skLineSegment(sketch, "E325", {"start": v(-61.29, -13.42) * mm, "end": v(-61.02, -13.25) * mm});
            skLineSegment(sketch, "E326", {"start": v(-61.02, -13.25) * mm, "end": v(-60.43, -13.21) * mm});
            skLineSegment(sketch, "E327", {"start": v(-60.43, -13.21) * mm, "end": v(-59.71, -12.62) * mm});
            skLineSegment(sketch, "E328", {"start": v(-59.71, -12.62) * mm, "end": v(-59.32, -12.68) * mm});
            skLineSegment(sketch, "E329", {"start": v(-59.32, -12.68) * mm, "end": v(-59.35, -12.24) * mm});
            skLineSegment(sketch, "E330", {"start": v(-59.35, -12.24) * mm, "end": v(-58.63, -12.13) * mm});
            skLineSegment(sketch, "E331", {"start": v(-58.63, -12.13) * mm, "end": v(-57.87, -12.41) * mm});
            skLineSegment(sketch, "E332", {"start": v(-57.87, -12.41) * mm, "end": v(-57.56, -12.82) * mm});
            skLineSegment(sketch, "E333", {"start": v(-57.56, -12.82) * mm, "end": v(-57.25, -12.97) * mm});
            skLineSegment(sketch, "E334", {"start": v(-57.25, -12.97) * mm, "end": v(-57.13, -13.42) * mm});
            skLineSegment(sketch, "E335", {"start": v(-57.13, -13.42) * mm, "end": v(-56.78, -13.5) * mm});
            skLineSegment(sketch, "E336", {"start": v(-56.78, -13.5) * mm, "end": v(-56.55, -13.94) * mm});
            skLineSegment(sketch, "E337", {"start": v(-56.55, -13.94) * mm, "end": v(-55.8, -14.03) * mm});
            skLineSegment(sketch, "E338", {"start": v(-60.6, -10.8) * mm, "end": v(-55.03, -10.52) * mm});
            skLineSegment(sketch, "E339", {"start": v(-66.34, -10.73) * mm, "end": v(-60.96, -10.18) * mm});
            skLineSegment(sketch, "E340", {"start": v(-60.96, -10.18) * mm, "end": v(-60.6, -10.8) * mm});
            skLineSegment(sketch, "E341", {"start": v(-66.34, -10.73) * mm, "end": v(-66.39, -11.09) * mm});
            skLineSegment(sketch, "E342", {"start": v(-66.39, -11.09) * mm, "end": v(-65.92, -11.5) * mm});
            skLineSegment(sketch, "E343", {"start": v(-65.92, -11.5) * mm, "end": v(-65.91, -12.35) * mm});
            skArc(sketch, "E344", {"start": v(-61.4, -6.84) * mm, "mid": v(-61.43, -6.53) * mm, "end": v(-61.6, -6.26) * mm});
            skArc(sketch, "E345", {"start": v(-61.13, -7.23) * mm, "mid": v(-61.2, -6.99) * mm, "end": v(-61.4, -6.84) * mm});
            skArc(sketch, "E346", {"start": v(-61.13, -7.23) * mm, "mid": v(-61.38, -7.9) * mm, "end": v(-61.28, -8.6) * mm});
            skArc(sketch, "E347", {"start": v(-61.28, -9.6) * mm, "mid": v(-61.22, -9.1) * mm, "end": v(-61.28, -8.6) * mm});
            skArc(sketch, "E348", {"start": v(-60.96, -10.18) * mm, "mid": v(-61.06, -9.86) * mm, "end": v(-61.28, -9.6) * mm});
            skLineSegment(sketch, "E349", {"start": v(-70.82, -11.07) * mm, "end": v(-74.7, -11.25) * mm});
            skLineSegment(sketch, "E350", {"start": v(-74.7, -11.25) * mm, "end": v(-74.65, -10.31) * mm});
            skLineSegment(sketch, "E351", {"start": v(-74.65, -10.31) * mm, "end": v(-73.69, -8.47) * mm});
            skLineSegment(sketch, "E352", {"start": v(-70.82, -11.07) * mm, "end": v(-70.95, -11.95) * mm});
            skLineSegment(sketch, "E353", {"start": v(-70.95, -11.95) * mm, "end": v(-70.56, -12.35) * mm});
            skLineSegment(sketch, "E354", {"start": v(-70.56, -12.35) * mm, "end": v(-70.32, -12.98) * mm});
            skLineSegment(sketch, "E355", {"start": v(-70.32, -12.98) * mm, "end": v(-69.9, -12.54) * mm});
            skArc(sketch, "E356", {"start": v(-69.9, -12.54) * mm, "mid": v(-69.6, -12.59) * mm, "end": v(-69.3, -12.54) * mm});
            skArc(sketch, "E357", {"start": v(-68.56, -12.54) * mm, "mid": v(-68.93, -12.38) * mm, "end": v(-69.3, -12.54) * mm});
            skLineSegment(sketch, "E358", {"start": v(-67.87, -12.38) * mm, "end": v(-67.98, -12.5) * mm});
            skLineSegment(sketch, "E359", {"start": v(-67.98, -12.5) * mm, "end": v(-68.56, -12.54) * mm});
            skArc(sketch, "E360", {"start": v(-82.04, -4.33) * mm, "mid": v(-81.46, -4.8) * mm, "end": v(-80.77, -5.04) * mm});
            skArc(sketch, "E361", {"start": v(-82.04, -4.33) * mm, "mid": v(-82.28, -4.3) * mm, "end": v(-82.44, -4.5) * mm});
            skArc(sketch, "E362", {"start": v(-82.86, -4.48) * mm, "mid": v(-83.14, -4.34) * mm, "end": v(-83.39, -4.54) * mm});
            skLineSegment(sketch, "E363", {"start": v(-82.44, -4.5) * mm, "end": v(-82.86, -4.48) * mm});
            skLineSegment(sketch, "E364", {"start": v(-83.39, -4.54) * mm, "end": v(-83.6, -4.44) * mm});
            skLineSegment(sketch, "E365", {"start": v(-83.6, -4.44) * mm, "end": v(-84.07, -4.45) * mm});
            skLineSegment(sketch, "E366", {"start": v(-84.07, -4.45) * mm, "end": v(-84.14, -4.67) * mm});
            skLineSegment(sketch, "E367", {"start": v(-84.14, -4.67) * mm, "end": v(-84.39, -4.8) * mm});
            skLineSegment(sketch, "E368", {"start": v(-84.39, -4.8) * mm, "end": v(-85.51, -4.48) * mm});
            skLineSegment(sketch, "E369", {"start": v(-85.51, -4.48) * mm, "end": v(-85.64, -4.28) * mm});
            skLineSegment(sketch, "E370", {"start": v(-85.64, -4.28) * mm, "end": v(-85.78, -4.3) * mm});
            skLineSegment(sketch, "E371", {"start": v(-85.78, -4.3) * mm, "end": v(-86, -4.72) * mm});
            skLineSegment(sketch, "E372", {"start": v(-86, -4.72) * mm, "end": v(-86.16, -4.78) * mm});
            skLineSegment(sketch, "E373", {"start": v(-86.16, -4.78) * mm, "end": v(-86.67, -4.59) * mm});
            skLineSegment(sketch, "E374", {"start": v(-86.67, -4.59) * mm, "end": v(-86.74, -4.33) * mm});
            skLineSegment(sketch, "E375", {"start": v(-86.74, -4.33) * mm, "end": v(-87.1, -4.32) * mm});
            skLineSegment(sketch, "E376", {"start": v(-87.1, -4.32) * mm, "end": v(-87.2, -4.25) * mm});
            skLineSegment(sketch, "E377", {"start": v(-87.2, -4.25) * mm, "end": v(-87.48, -4.51) * mm});
            skLineSegment(sketch, "E378", {"start": v(-87.48, -4.51) * mm, "end": v(-87.74, -4.43) * mm});
            skLineSegment(sketch, "E379", {"start": v(-87.74, -4.43) * mm, "end": v(-87.78, -4.19) * mm});
            skLineSegment(sketch, "E380", {"start": v(-87.78, -4.19) * mm, "end": v(-88.14, -3.8) * mm});
            skLineSegment(sketch, "E381", {"start": v(-88.14, -3.8) * mm, "end": v(-88.51, -3.73) * mm});
            skLineSegment(sketch, "E382", {"start": v(-88.51, -3.73) * mm, "end": v(-88.73, -3.92) * mm});
            skLineSegment(sketch, "E383", {"start": v(-88.73, -3.92) * mm, "end": v(-89.08, -3.68) * mm});
            skLineSegment(sketch, "E384", {"start": v(-89.08, -3.68) * mm, "end": v(-89.47, -3.64) * mm});
            skLineSegment(sketch, "E385", {"start": v(-89.47, -3.64) * mm, "end": v(-89.74, -3.51) * mm});
            skLineSegment(sketch, "E386", {"start": v(-89.74, -3.51) * mm, "end": v(-90.2, -3.48) * mm});
            skLineSegment(sketch, "E387", {"start": v(-90.2, -3.48) * mm, "end": v(-90.21, -3.05) * mm});
            skLineSegment(sketch, "E388", {"start": v(-90.21, -3.05) * mm, "end": v(-90.46, -2.94) * mm});
            skLineSegment(sketch, "E389", {"start": v(-90.46, -2.94) * mm, "end": v(-90.49, -3.07) * mm});
            skLineSegment(sketch, "E390", {"start": v(-90.49, -3.07) * mm, "end": v(-90.67, -3.09) * mm});
            skLineSegment(sketch, "E391", {"start": v(-90.67, -3.09) * mm, "end": v(-90.86, -2.86) * mm});
            skLineSegment(sketch, "E392", {"start": v(-90.86, -2.86) * mm, "end": v(-90.95, -3.07) * mm});
            skLineSegment(sketch, "E393", {"start": v(-90.95, -3.07) * mm, "end": v(-91.1, -3.09) * mm});
            skLineSegment(sketch, "E394", {"start": v(-91.1, -3.09) * mm, "end": v(-91.72, -2.53) * mm});
            skLineSegment(sketch, "E395", {"start": v(-79.2, -14.64) * mm, "end": v(-78.77, -14.49) * mm});
            skLineSegment(sketch, "E396", {"start": v(-78.77, -14.49) * mm, "end": v(-77.82, -14.42) * mm});
            skLineSegment(sketch, "E397", {"start": v(-77.82, -14.42) * mm, "end": v(-76.68, -14.82) * mm});
            skLineSegment(sketch, "E398", {"start": v(-76.68, -14.82) * mm, "end": v(-76, -14.94) * mm});
            skLineSegment(sketch, "E399", {"start": v(-76, -14.94) * mm, "end": v(-75.48, -14.7) * mm});
            skLineSegment(sketch, "E400", {"start": v(-75.48, -14.7) * mm, "end": v(-75.71, -14.57) * mm});
            skLineSegment(sketch, "E401", {"start": v(-75.71, -14.57) * mm, "end": v(-75.65, -14.4) * mm});
            skLineSegment(sketch, "E402", {"start": v(-75.65, -14.4) * mm, "end": v(-75.3, -14.27) * mm});
            skLineSegment(sketch, "E403", {"start": v(-75.3, -14.27) * mm, "end": v(-75.11, -14.42) * mm});
            skLineSegment(sketch, "E404", {"start": v(-75.11, -14.42) * mm, "end": v(-74.88, -14.3) * mm});
            skLineSegment(sketch, "E405", {"start": v(-74.88, -14.3) * mm, "end": v(-74.55, -14.38) * mm});
            skLineSegment(sketch, "E406", {"start": v(-74.55, -14.38) * mm, "end": v(-74.35, -14.7) * mm});
            skLineSegment(sketch, "E407", {"start": v(-74.35, -14.7) * mm, "end": v(-74.35, -14.93) * mm});
            skLineSegment(sketch, "E408", {"start": v(-74.35, -14.93) * mm, "end": v(-73.84, -14.94) * mm});
            skLineSegment(sketch, "E409", {"start": v(-73.84, -14.94) * mm, "end": v(-73.64, -15.11) * mm});
            skLineSegment(sketch, "E410", {"start": v(-73.64, -15.11) * mm, "end": v(-73.83, -15.4) * mm});
            skLineSegment(sketch, "E411", {"start": v(-73.83, -15.4) * mm, "end": v(-72.77, -16) * mm});
            skLineSegment(sketch, "E412", {"start": v(-72.77, -16) * mm, "end": v(-72.34, -15.84) * mm});
            skLineSegment(sketch, "E413", {"start": v(-72.34, -15.84) * mm, "end": v(-72.27, -15.58) * mm});
            skLineSegment(sketch, "E414", {"start": v(-72.27, -15.58) * mm, "end": v(-71.96, -15.52) * mm});
            skLineSegment(sketch, "E415", {"start": v(-71.96, -15.52) * mm, "end": v(-71.8, -15.34) * mm});
            skLineSegment(sketch, "E416", {"start": v(-71.8, -15.34) * mm, "end": v(-71.62, -15.46) * mm});
            skLineSegment(sketch, "E417", {"start": v(-71.62, -15.46) * mm, "end": v(-71.54, -15.76) * mm});
            skLineSegment(sketch, "E418", {"start": v(-71.54, -15.76) * mm, "end": v(-71.42, -15.83) * mm});
            skLineSegment(sketch, "E419", {"start": v(-71.42, -15.83) * mm, "end": v(-71.14, -15.44) * mm});
            skLineSegment(sketch, "E420", {"start": v(-71.14, -15.44) * mm, "end": v(-71.14, -15.36) * mm});
            skLineSegment(sketch, "E421", {"start": v(-71.14, -15.36) * mm, "end": v(-71.27, -15.32) * mm});
            skLineSegment(sketch, "E422", {"start": v(-71.27, -15.32) * mm, "end": v(-71.2, -15.2) * mm});
            skLineSegment(sketch, "E423", {"start": v(-71.2, -15.2) * mm, "end": v(-71.16, -14.96) * mm});
            skLineSegment(sketch, "E424", {"start": v(-71.16, -14.96) * mm, "end": v(-70.96, -14.93) * mm});
            skLineSegment(sketch, "E425", {"start": v(-70.96, -14.93) * mm, "end": v(-70.82, -14.78) * mm});
            skLineSegment(sketch, "E426", {"start": v(-70.82, -14.78) * mm, "end": v(-70.72, -14.87) * mm});
            skLineSegment(sketch, "E427", {"start": v(-70.72, -14.87) * mm, "end": v(-70.75, -15.17) * mm});
            skLineSegment(sketch, "E428", {"start": v(-70.75, -15.17) * mm, "end": v(-70.4, -15.24) * mm});
            skLineSegment(sketch, "E429", {"start": v(-70.4, -15.24) * mm, "end": v(-69.77, -15.52) * mm});
            skLineSegment(sketch, "E430", {"start": v(-69.77, -15.52) * mm, "end": v(-69.7, -15.65) * mm});
            skLineSegment(sketch, "E431", {"start": v(-69.7, -15.65) * mm, "end": v(-69.35, -15.66) * mm});
            skLineSegment(sketch, "E432", {"start": v(-69.35, -15.66) * mm, "end": v(-69.22, -15.75) * mm});
            skLineSegment(sketch, "E433", {"start": v(-69.22, -15.75) * mm, "end": v(-68.97, -15.44) * mm});
            skLineSegment(sketch, "E434", {"start": v(-68.97, -15.44) * mm, "end": v(-68.98, -15.3) * mm});
            skLineSegment(sketch, "E435", {"start": v(-68.98, -15.3) * mm, "end": v(-69.13, -15.27) * mm});
            skLineSegment(sketch, "E436", {"start": v(-69.13, -15.27) * mm, "end": v(-69.48, -14.96) * mm});
            skLineSegment(sketch, "E437", {"start": v(-69.48, -14.96) * mm, "end": v(-70.16, -14.85) * mm});
            skLineSegment(sketch, "E438", {"start": v(-70.16, -14.85) * mm, "end": v(-70.48, -14.65) * mm});
            skLineSegment(sketch, "E439", {"start": v(-70.48, -14.65) * mm, "end": v(-70.24, -14.27) * mm});
            skLineSegment(sketch, "E440", {"start": v(-70.24, -14.27) * mm, "end": v(-70.3, -14.12) * mm});
            skLineSegment(sketch, "E441", {"start": v(-70.3, -14.12) * mm, "end": v(-69.95, -14.12) * mm});
            skLineSegment(sketch, "E442", {"start": v(-69.95, -14.12) * mm, "end": v(-69.76, -13.84) * mm});
            skLineSegment(sketch, "E443", {"start": v(-69.76, -13.84) * mm, "end": v(-69.93, -13.3) * mm});
            skLineSegment(sketch, "E444", {"start": v(-69.93, -13.3) * mm, "end": v(-70.27, -13.45) * mm});
            skLineSegment(sketch, "E445", {"start": v(-70.27, -13.45) * mm, "end": v(-70.31, -13.8) * mm});
            skLineSegment(sketch, "E446", {"start": v(-70.31, -13.8) * mm, "end": v(-70.67, -13.74) * mm});
            skLineSegment(sketch, "E447", {"start": v(-70.67, -13.74) * mm, "end": v(-70.78, -13.53) * mm});
            skLineSegment(sketch, "E448", {"start": v(-70.78, -13.53) * mm, "end": v(-70.32, -12.98) * mm});
            skLineSegment(sketch, "E449", {"start": v(-73.69, -8.47) * mm, "end": v(-73.78, -8.23) * mm});
            skLineSegment(sketch, "E450", {"start": v(-73.78, -8.23) * mm, "end": v(-73.62, -8.2) * mm});
            skLineSegment(sketch, "E451", {"start": v(-73.62, -8.2) * mm, "end": v(-73.64, -7.89) * mm});
            skLineSegment(sketch, "E452", {"start": v(-73.64, -7.89) * mm, "end": v(-73.82, -7.72) * mm});
            skLineSegment(sketch, "E453", {"start": v(-73.82, -7.72) * mm, "end": v(-73.83, -7.41) * mm});
            skLineSegment(sketch, "E454", {"start": v(-73.83, -7.41) * mm, "end": v(-74.04, -6.88) * mm});
            skLineSegment(sketch, "E455", {"start": v(-74.04, -6.88) * mm, "end": v(-73.99, -6.34) * mm});
            skLineSegment(sketch, "E456", {"start": v(-73.99, -6.34) * mm, "end": v(-73.94, -5.7) * mm});
            skLineSegment(sketch, "E457", {"start": v(-73.94, -5.7) * mm, "end": v(-74.1, -4.93) * mm});
            skLineSegment(sketch, "E458", {"start": v(-74.1, -4.93) * mm, "end": v(-74.02, -4) * mm});
            skLineSegment(sketch, "E459", {"start": v(-74.02, -4) * mm, "end": v(-73.62, -3.7) * mm});
            skLineSegment(sketch, "E460", {"start": v(-73.62, -3.7) * mm, "end": v(-73.66, -3.5) * mm});
            skLineSegment(sketch, "E461", {"start": v(-73.66, -3.5) * mm, "end": v(-73.33, -2.95) * mm});
            skLineSegment(sketch, "E462", {"start": v(-73.33, -2.95) * mm, "end": v(-72.95, -2.81) * mm});
            skLineSegment(sketch, "E463", {"start": v(-72.95, -2.81) * mm, "end": v(-73.02, -2.33) * mm});
            skLineSegment(sketch, "E464", {"start": v(-73.02, -2.33) * mm, "end": v(-72.7, -1.75) * mm});
            skLineSegment(sketch, "E465", {"start": v(-72.7, -1.75) * mm, "end": v(-72.55, -1.67) * mm});
            skLineSegment(sketch, "E466", {"start": v(-72.55, -1.67) * mm, "end": v(-72.43, -1.5) * mm});
            skLineSegment(sketch, "E467", {"start": v(-72.43, -1.5) * mm, "end": v(-72.5, -1.3) * mm});
            skLineSegment(sketch, "E468", {"start": v(-72.5, -1.3) * mm, "end": v(-72.15, -0.9) * mm});
            skLineSegment(sketch, "E469", {"start": v(-72.15, -0.9) * mm, "end": v(-72.05, -0.4) * mm});
            skLineSegment(sketch, "E470", {"start": v(-72.05, -0.4) * mm, "end": v(-72.18, -0.01) * mm});
            skLineSegment(sketch, "E471", {"start": v(-72.18, -0.01) * mm, "end": v(-71.73, 0.18) * mm});
            skLineSegment(sketch, "E472", {"start": v(-71.73, 0.18) * mm, "end": v(-71.55, 1.14) * mm});
            skLineSegment(sketch, "E473", {"start": v(-71.32, 2.46) * mm, "end": v(-71.32, 1.8) * mm});
            skLineSegment(sketch, "E474", {"start": v(-71.32, 1.8) * mm, "end": v(-71.55, 1.14) * mm});
            skLineSegment(sketch, "E475", {"start": v(-71.32, 2.46) * mm, "end": v(-70.65, 2.92) * mm});
            skLineSegment(sketch, "E476", {"start": v(-70.65, 2.92) * mm, "end": v(-70.6, 3.32) * mm});
            skLineSegment(sketch, "E477", {"start": v(-70.6, 3.32) * mm, "end": v(-70.53, 3.5) * mm});
            skLineSegment(sketch, "E478", {"start": v(-70.53, 3.5) * mm, "end": v(-70.54, 3.66) * mm});
            skLineSegment(sketch, "E479", {"start": v(-70.54, 3.66) * mm, "end": v(-70.7, 3.71) * mm});
            skLineSegment(sketch, "E480", {"start": v(-70.7, 3.71) * mm, "end": v(-71, 3.73) * mm});
            skLineSegment(sketch, "E481", {"start": v(-71, 3.73) * mm, "end": v(-71.39, 4.37) * mm});
            skLineSegment(sketch, "E482", {"start": v(-71.39, 4.37) * mm, "end": v(-71.71, 5.65) * mm});
            skLineSegment(sketch, "E483", {"start": v(-71.71, 5.65) * mm, "end": v(-72.12, 5.7) * mm});
            skLineSegment(sketch, "E484", {"start": v(-72.12, 5.7) * mm, "end": v(-73, 6.32) * mm});
            skLineSegment(sketch, "E485", {"start": v(-73, 6.32) * mm, "end": v(-73.17, 6.72) * mm});
            skLineSegment(sketch, "E486", {"start": v(-73.17, 6.72) * mm, "end": v(-72.93, 7.5) * mm});
            skLineSegment(sketch, "E487", {"start": v(-72.93, 7.5) * mm, "end": v(-72.78, 8.1) * mm});
            skLineSegment(sketch, "E488", {"start": v(-72.78, 8.1) * mm, "end": v(-73.8, 8.35) * mm});
            skLineSegment(sketch, "E489", {"start": v(-73.8, 8.35) * mm, "end": v(-73.82, 9) * mm});
            skLineSegment(sketch, "E490", {"start": v(-73.82, 9) * mm, "end": v(-74.42, 9.35) * mm});
            skLineSegment(sketch, "E491", {"start": v(-74.42, 9.35) * mm, "end": v(-75.22, 10.17) * mm});
            skLineSegment(sketch, "E492", {"start": v(-75.22, 10.17) * mm, "end": v(-75.54, 11.5) * mm});
            skLineSegment(sketch, "E493", {"start": v(-75.54, 11.5) * mm, "end": v(-75.44, 11.7) * mm});
            skLineSegment(sketch, "E494", {"start": v(-75.44, 11.7) * mm, "end": v(-75.29, 11.9) * mm});
            skLineSegment(sketch, "E495", {"start": v(-75.29, 11.9) * mm, "end": v(-75.3, 12.27) * mm});
            skLineSegment(sketch, "E496", {"start": v(-75.3, 12.27) * mm, "end": v(-74.9, 12.47) * mm});
            skLineSegment(sketch, "E497", {"start": v(-76, 12.3) * mm, "end": v(-75.44, 11.7) * mm});
            skLineSegment(sketch, "E498", {"start": v(-74.9, 12.47) * mm, "end": v(-74.9, 12.9) * mm});
            skLineSegment(sketch, "E499", {"start": v(-74.9, 12.9) * mm, "end": v(-74.63, 13.07) * mm});
            skLineSegment(sketch, "E500", {"start": v(-74.63, 13.07) * mm, "end": v(-74.56, 13.55) * mm});
            skLineSegment(sketch, "E501", {"start": v(-74.56, 13.55) * mm, "end": v(-74.88, 13.8) * mm});
            skLineSegment(sketch, "E502", {"start": v(-74.88, 13.8) * mm, "end": v(-74.75, 14.28) * mm});
            skLineSegment(sketch, "E503", {"start": v(-74.75, 14.28) * mm, "end": v(-73.7, 14.7) * mm});
            skLineSegment(sketch, "E504", {"start": v(-73.7, 14.7) * mm, "end": v(-73.36, 16) * mm});
            skLineSegment(sketch, "E505", {"start": v(-73.36, 16) * mm, "end": v(-73.82, 16.5) * mm});
            skLineSegment(sketch, "E506", {"start": v(-73.82, 16.5) * mm, "end": v(-73.85, 16.68) * mm});
            skLineSegment(sketch, "E507", {"start": v(-73.85, 16.68) * mm, "end": v(-74.24, 16.9) * mm});
            skLineSegment(sketch, "E508", {"start": v(-74.24, 16.9) * mm, "end": v(-74.23, 17.12) * mm});
            skLineSegment(sketch, "E509", {"start": v(-74.37, 17.35) * mm, "end": v(-75, 17.56) * mm});
            skLineSegment(sketch, "E510", {"start": v(-74.37, 17.35) * mm, "end": v(-74.23, 17.12) * mm});
            skLineSegment(sketch, "E511", {"start": v(-75, 17.56) * mm, "end": v(-75.25, 18.01) * mm});
            skLineSegment(sketch, "E512", {"start": v(-75.25, 18.01) * mm, "end": v(-75.27, 18.35) * mm});
            skLineSegment(sketch, "E513", {"start": v(-75.27, 18.35) * mm, "end": v(-75.07, 18.7) * mm});
            skLineSegment(sketch, "E514", {"start": v(-75.07, 18.7) * mm, "end": v(-75.08, 18.87) * mm});
            skLineSegment(sketch, "E515", {"start": v(-75.08, 18.87) * mm, "end": v(-75.34, 19.06) * mm});
            skLineSegment(sketch, "E516", {"start": v(-75.34, 19.06) * mm, "end": v(-75.47, 19.43) * mm});
            skLineSegment(sketch, "E517", {"start": v(-68.03, 9.8) * mm, "end": v(-68.5, 15.56) * mm});
            skLineSegment(sketch, "E518", {"start": v(-68.5, 15.56) * mm, "end": v(-67.92, 15.37) * mm});
            skLineSegment(sketch, "E519", {"start": v(-67.92, 15.37) * mm, "end": v(-67.28, 15.71) * mm});
            skLineSegment(sketch, "E520", {"start": v(-69.3, 17.4) * mm, "end": v(-69.15, 16.77) * mm});
            skLineSegment(sketch, "E521", {"start": v(-69.15, 16.77) * mm, "end": v(-68.87, 16.36) * mm});
            skLineSegment(sketch, "E522", {"start": v(-68.87, 16.36) * mm, "end": v(-68.66, 15.66) * mm});
            skLineSegment(sketch, "E523", {"start": v(-68.66, 15.66) * mm, "end": v(-68.5, 15.56) * mm});
            skLineSegment(sketch, "E524", {"start": v(-82.45, 32.53) * mm, "end": v(-82.38, 33.43) * mm});
            skLineSegment(sketch, "E525", {"start": v(-82.38, 33.43) * mm, "end": v(-81.99, 33.35) * mm});
            skLineSegment(sketch, "E526", {"start": v(-81.99, 33.35) * mm, "end": v(-81.75, 32.12) * mm});
            skLineSegment(sketch, "E527", {"start": v(-81.75, 32.12) * mm, "end": v(-81.51, 31.86) * mm});
            skLineSegment(sketch, "E528", {"start": v(-81.51, 31.86) * mm, "end": v(-80.98, 31.86) * mm});
            skLineSegment(sketch, "E529", {"start": v(-80.98, 31.86) * mm, "end": v(-80.97, 31.71) * mm});
            skLineSegment(sketch, "E530", {"start": v(-80.97, 31.71) * mm, "end": v(-80.3, 31.66) * mm});
            skLineSegment(sketch, "E531", {"start": v(-80.3, 31.66) * mm, "end": v(-80.3, 31.41) * mm});
            skLineSegment(sketch, "E532", {"start": v(-80.3, 31.41) * mm, "end": v(-79.66, 31.43) * mm});
            skLineSegment(sketch, "E533", {"start": v(-79.66, 31.43) * mm, "end": v(-79.53, 31.67) * mm});
            skLineSegment(sketch, "E534", {"start": v(-79.53, 31.67) * mm, "end": v(-79.31, 31.76) * mm});
            skLineSegment(sketch, "E535", {"start": v(-79.31, 31.76) * mm, "end": v(-79.14, 31.65) * mm});
            skLineSegment(sketch, "E536", {"start": v(-79.14, 31.65) * mm, "end": v(-78.84, 31.65) * mm});
            skLineSegment(sketch, "E537", {"start": v(-78.84, 31.65) * mm, "end": v(-77.58, 31.03) * mm});
            skLineSegment(sketch, "E538", {"start": v(-77.58, 31.03) * mm, "end": v(-77.35, 31.08) * mm});
            skLineSegment(sketch, "E539", {"start": v(-77.35, 31.08) * mm, "end": v(-77.32, 30.91) * mm});
            skLineSegment(sketch, "E540", {"start": v(-77.32, 30.91) * mm, "end": v(-77, 30.76) * mm});
            skLineSegment(sketch, "E541", {"start": v(-77, 30.76) * mm, "end": v(-76.87, 30.75) * mm});
            skLineSegment(sketch, "E542", {"start": v(-76.87, 30.75) * mm, "end": v(-76.83, 30.56) * mm});
            skLineSegment(sketch, "E543", {"start": v(-76.83, 30.56) * mm, "end": v(-76.54, 30.44) * mm});
            skLineSegment(sketch, "E544", {"start": v(-76.54, 30.44) * mm, "end": v(-76.3, 30.4) * mm});
            skLineSegment(sketch, "E545", {"start": v(-76.3, 30.4) * mm, "end": v(-76.08, 30.45) * mm});
            skLineSegment(sketch, "E546", {"start": v(-76.08, 30.45) * mm, "end": v(-75.56, 30.9) * mm});
            skLineSegment(sketch, "E547", {"start": v(-75.56, 30.9) * mm, "end": v(-75.36, 30.91) * mm});
            skLineSegment(sketch, "E548", {"start": v(-75.36, 30.91) * mm, "end": v(-75.26, 30.63) * mm});
            skLineSegment(sketch, "E549", {"start": v(-75.26, 30.63) * mm, "end": v(-75.09, 30.57) * mm});
            skLineSegment(sketch, "E550", {"start": v(-75.09, 30.57) * mm, "end": v(-74.94, 30.68) * mm});
            skLineSegment(sketch, "E551", {"start": v(-74.94, 30.68) * mm, "end": v(-74.05, 30.7) * mm});
            skLineSegment(sketch, "E552", {"start": v(-74.05, 30.7) * mm, "end": v(-73.85, 30.4) * mm});
            skLineSegment(sketch, "E553", {"start": v(-73.85, 30.4) * mm, "end": v(-73.68, 30.4) * mm});
            skLineSegment(sketch, "E554", {"start": v(-73.68, 30.4) * mm, "end": v(-73.6, 30.48) * mm});
            skLineSegment(sketch, "E555", {"start": v(-73.6, 30.48) * mm, "end": v(-73.18, 30.52) * mm});
            skLineSegment(sketch, "E556", {"start": v(-73.18, 30.52) * mm, "end": v(-73.4, 30.28) * mm});
            skLineSegment(sketch, "E557", {"start": v(-73.4, 30.28) * mm, "end": v(-73.87, 30.1) * mm});
            skLineSegment(sketch, "E558", {"start": v(-73.87, 30.1) * mm, "end": v(-75.11, 29.53) * mm});
            skLineSegment(sketch, "E559", {"start": v(-75.11, 29.53) * mm, "end": v(-75.48, 29.28) * mm});
            skLineSegment(sketch, "E560", {"start": v(-75.48, 29.28) * mm, "end": v(-75.72, 28.92) * mm});
            skLineSegment(sketch, "E561", {"start": v(-75.72, 28.92) * mm, "end": v(-76.09, 28.34) * mm});
            skLineSegment(sketch, "E562", {"start": v(-76.09, 28.34) * mm, "end": v(-76.25, 28.3) * mm});
            skLineSegment(sketch, "E563", {"start": v(-76.25, 28.3) * mm, "end": v(-76.74, 27.69) * mm});
            skLineSegment(sketch, "E564", {"start": v(-76.74, 27.69) * mm, "end": v(-77.07, 27.7) * mm});
            skLineSegment(sketch, "E565", {"start": v(-77.07, 27.7) * mm, "end": v(-77.32, 27.4) * mm});
            skLineSegment(sketch, "E566", {"start": v(-77.32, 27.4) * mm, "end": v(-77.24, 27.25) * mm});
            skLineSegment(sketch, "E567", {"start": v(-77.24, 27.25) * mm, "end": v(-76.79, 27.21) * mm});
            skLineSegment(sketch, "E568", {"start": v(-76.79, 27.21) * mm, "end": v(-75.19, 27.9) * mm});
            skLineSegment(sketch, "E569", {"start": v(-75.19, 27.9) * mm, "end": v(-74.97, 27.73) * mm});
            skLineSegment(sketch, "E570", {"start": v(-74.97, 27.73) * mm, "end": v(-75.33, 27.15) * mm});
            skLineSegment(sketch, "E571", {"start": v(-75.33, 27.15) * mm, "end": v(-75.3, 26.96) * mm});
            skLineSegment(sketch, "E572", {"start": v(-75.3, 26.96) * mm, "end": v(-75.02, 27.1) * mm});
            skLineSegment(sketch, "E573", {"start": v(-75.02, 27.1) * mm, "end": v(-74.69, 27.1) * mm});
            skLineSegment(sketch, "E574", {"start": v(-74.69, 27.1) * mm, "end": v(-74.55, 26.87) * mm});
            skLineSegment(sketch, "E575", {"start": v(-74.55, 26.87) * mm, "end": v(-74.48, 26.87) * mm});
            skLineSegment(sketch, "E576", {"start": v(-74.48, 26.87) * mm, "end": v(-74.3, 27.08) * mm});
            skLineSegment(sketch, "E577", {"start": v(-74.3, 27.08) * mm, "end": v(-73.96, 27.21) * mm});
            skLineSegment(sketch, "E578", {"start": v(-73.96, 27.21) * mm, "end": v(-73.47, 27.5) * mm});
            skLineSegment(sketch, "E579", {"start": v(-73.47, 27.5) * mm, "end": v(-73.5, 27.57) * mm});
            skLineSegment(sketch, "E580", {"start": v(-73.5, 27.57) * mm, "end": v(-73.4, 27.69) * mm});
            skLineSegment(sketch, "E581", {"start": v(-73.4, 27.69) * mm, "end": v(-72.7, 27.78) * mm});
            skLineSegment(sketch, "E582", {"start": v(-72.7, 27.78) * mm, "end": v(-72.05, 28.2) * mm});
            skLineSegment(sketch, "E583", {"start": v(-72.05, 28.2) * mm, "end": v(-71.78, 28.7) * mm});
            skLineSegment(sketch, "E584", {"start": v(-71.78, 28.7) * mm, "end": v(-71.58, 28.76) * mm});
            skLineSegment(sketch, "E585", {"start": v(-71.58, 28.76) * mm, "end": v(-71.2, 29.22) * mm});
            skLineSegment(sketch, "E586", {"start": v(-71.2, 29.22) * mm, "end": v(-70.78, 29.5) * mm});
            skLineSegment(sketch, "E587", {"start": v(-70.78, 29.5) * mm, "end": v(-70.24, 29.57) * mm});
            skLineSegment(sketch, "E588", {"start": v(-70.24, 29.57) * mm, "end": v(-70.05, 29.45) * mm});
            skLineSegment(sketch, "E589", {"start": v(-70.05, 29.45) * mm, "end": v(-70.1, 29.32) * mm});
            skLineSegment(sketch, "E590", {"start": v(-70.1, 29.32) * mm, "end": v(-70.48, 29.22) * mm});
            skLineSegment(sketch, "E591", {"start": v(-70.48, 29.22) * mm, "end": v(-70.68, 28.86) * mm});
            skLineSegment(sketch, "E592", {"start": v(-70.68, 28.86) * mm, "end": v(-70.92, 28.74) * mm});
            skLineSegment(sketch, "E593", {"start": v(-70.92, 28.74) * mm, "end": v(-70.96, 28.56) * mm});
            skLineSegment(sketch, "E594", {"start": v(-70.96, 28.56) * mm, "end": v(-71.27, 28.11) * mm});
            skLineSegment(sketch, "E595", {"start": v(-71.27, 28.11) * mm, "end": v(-71.24, 27.85) * mm});
            skLineSegment(sketch, "E596", {"start": v(-71.24, 27.85) * mm, "end": v(-71.18, 27.8) * mm});
            skLineSegment(sketch, "E597", {"start": v(-71.18, 27.8) * mm, "end": v(-70.68, 28.26) * mm});
            skLineSegment(sketch, "E598", {"start": v(-70.68, 28.26) * mm, "end": v(-70.54, 28.11) * mm});
            skLineSegment(sketch, "E599", {"start": v(-70.54, 28.11) * mm, "end": v(-69.81, 27.94) * mm});
            skLineSegment(sketch, "E600", {"start": v(-69.81, 27.94) * mm, "end": v(-69.34, 27.27) * mm});
            skLineSegment(sketch, "E601", {"start": v(-69.34, 27.27) * mm, "end": v(-68.86, 27.28) * mm});
            skLineSegment(sketch, "E602", {"start": v(-54.85, 18.69) * mm, "end": v(-55.4, 18.2) * mm});
            skLineSegment(sketch, "E603", {"start": v(-55.4, 18.2) * mm, "end": v(-56.04, 17.76) * mm});
            skLineSegment(sketch, "E604", {"start": v(-56.04, 17.76) * mm, "end": v(-55.2, 12.32) * mm});
            skLineSegment(sketch, "E605", {"start": v(-55.2, 12.32) * mm, "end": v(-46.6, 13.92) * mm});
            skLineSegment(sketch, "E606", {"start": v(-46.6, 13.92) * mm, "end": v(-45.76, 10.93) * mm});
            skLineSegment(sketch, "E607", {"start": v(-45.76, 10.93) * mm, "end": v(-44.57, 11.15) * mm});
            skLineSegment(sketch, "E608", {"start": v(-40.43, 19.54) * mm, "end": v(-40.76, 21.05) * mm});
            skLineSegment(sketch, "E609", {"start": v(-40.76, 21.05) * mm, "end": v(-40.1, 21.23) * mm});
            skLineSegment(sketch, "E610", {"start": v(-40.1, 21.23) * mm, "end": v(-39.29, 20.2) * mm});
            skLineSegment(sketch, "E611", {"start": v(-39.29, 20.2) * mm, "end": v(-39.75, 19.91) * mm});
            skLineSegment(sketch, "E612", {"start": v(-39.75, 19.91) * mm, "end": v(-39.85, 19.75) * mm});
            skLineSegment(sketch, "E613", {"start": v(-39.85, 19.75) * mm, "end": v(-40.43, 19.54) * mm});
            skLineSegment(sketch, "E614", {"start": v(-40.43, 19.54) * mm, "end": v(-40.5, 19.4) * mm});
            skLineSegment(sketch, "E615", {"start": v(-40.5, 19.4) * mm, "end": v(-42.2, 18.78) * mm});
            skLineSegment(sketch, "E616", {"start": v(-42.2, 18.78) * mm, "end": v(-42.25, 18.85) * mm});
            skLineSegment(sketch, "E617", {"start": v(-42.25, 18.85) * mm, "end": v(-42.86, 18.27) * mm});
            skLineSegment(sketch, "E618", {"start": v(-42.86, 18.27) * mm, "end": v(-43.43, 17.92) * mm});
            skLineSegment(sketch, "E619", {"start": v(-40.76, 21.05) * mm, "end": v(-43.79, 20.44) * mm});
            skLineSegment(sketch, "E620", {"start": v(-43.79, 22.2) * mm, "end": v(-40.28, 23.03) * mm});
            skLineSegment(sketch, "E621", {"start": v(-40.28, 23.03) * mm, "end": v(-40.03, 23.39) * mm});
            skLineSegment(sketch, "E622", {"start": v(-40.03, 23.39) * mm, "end": v(-39.63, 23.53) * mm});
            skLineSegment(sketch, "E623", {"start": v(-39.63, 23.53) * mm, "end": v(-39.35, 23.1) * mm});
            skLineSegment(sketch, "E624", {"start": v(-39.35, 23.1) * mm, "end": v(-39.6, 22.37) * mm});
            skLineSegment(sketch, "E625", {"start": v(-39.6, 22.37) * mm, "end": v(-39.4, 22.07) * mm});
            skLineSegment(sketch, "E626", {"start": v(-39.4, 22.07) * mm, "end": v(-39.28, 22.16) * mm});
            skLineSegment(sketch, "E627", {"start": v(-39.28, 22.16) * mm, "end": v(-39.04, 22.1) * mm});
            skLineSegment(sketch, "E628", {"start": v(-39.04, 22.1) * mm, "end": v(-38.43, 21.2) * mm});
            skLineSegment(sketch, "E629", {"start": v(-38.43, 21.2) * mm, "end": v(-37.96, 21.15) * mm});
            skLineSegment(sketch, "E630", {"start": v(-37.96, 21.15) * mm, "end": v(-37.7, 21.28) * mm});
            skLineSegment(sketch, "E631", {"start": v(-37.7, 21.28) * mm, "end": v(-37.59, 21.4) * mm});
            skLineSegment(sketch, "E632", {"start": v(-39.29, 20.2) * mm, "end": v(-38.98, 20.33) * mm});
            skLineSegment(sketch, "E633", {"start": v(-38.98, 20.33) * mm, "end": v(-39, 20.6) * mm});
            skLineSegment(sketch, "E634", {"start": v(-39, 20.6) * mm, "end": v(-38.6, 20.87) * mm});
            skLineSegment(sketch, "E635", {"start": v(-38.6, 20.87) * mm, "end": v(-38.5, 20.4) * mm});
            skLineSegment(sketch, "E636", {"start": v(-38.5, 20.4) * mm, "end": v(-38.25, 20.67) * mm});
            skLineSegment(sketch, "E637", {"start": v(-38.25, 20.67) * mm, "end": v(-37.92, 20.87) * mm});
            skLineSegment(sketch, "E638", {"start": v(-37.92, 20.87) * mm, "end": v(-37.54, 21) * mm});
            skLineSegment(sketch, "E639", {"start": v(-37.54, 21) * mm, "end": v(-37.3, 21.08) * mm});
            skLineSegment(sketch, "E640", {"start": v(-37.3, 21.08) * mm, "end": v(-37.36, 21.5) * mm});
            skLineSegment(sketch, "E641", {"start": v(-37.36, 21.5) * mm, "end": v(-37.54, 21.73) * mm});
            skLineSegment(sketch, "E642", {"start": v(-37.59, 21.4) * mm, "end": v(-37.54, 21.73) * mm});
            skLineSegment(sketch, "E643", {"start": v(-45.15, 27.46) * mm, "end": v(-42.22, 28.28) * mm});
            skLineSegment(sketch, "E644", {"start": v(-42.22, 28.28) * mm, "end": v(-42.09, 28) * mm});
            skLineSegment(sketch, "E645", {"start": v(-42.09, 28) * mm, "end": v(-42.2, 27.6) * mm});
            skLineSegment(sketch, "E646", {"start": v(-42.2, 27.6) * mm, "end": v(-41.92, 27.28) * mm});
            skLineSegment(sketch, "E647", {"start": v(-41.92, 27.28) * mm, "end": v(-41.98, 27.2) * mm});
            skLineSegment(sketch, "E648", {"start": v(-41.98, 27.2) * mm, "end": v(-41.9, 27.04) * mm});
            skLineSegment(sketch, "E649", {"start": v(-41.9, 27.04) * mm, "end": v(-42.38, 26.5) * mm});
            skLineSegment(sketch, "E650", {"start": v(-42.38, 26.5) * mm, "end": v(-42.63, 26.4) * mm});
            skLineSegment(sketch, "E651", {"start": v(-42.63, 26.4) * mm, "end": v(-42.63, 26.2) * mm});
            skLineSegment(sketch, "E652", {"start": v(-42.63, 26.2) * mm, "end": v(-42.52, 26.08) * mm});
            skLineSegment(sketch, "E653", {"start": v(-42.52, 26.08) * mm, "end": v(-42.63, 23.52) * mm});
            skLineSegment(sketch, "E654", {"start": v(-42.63, 23.52) * mm, "end": v(-42.52, 23.47) * mm});
            skLineSegment(sketch, "E655", {"start": v(-42.52, 23.47) * mm, "end": v(-42.54, 22.94) * mm});
            skLineSegment(sketch, "E656", {"start": v(-42.54, 22.94) * mm, "end": v(-42.54, 22.7) * mm});
            skLineSegment(sketch, "E657", {"start": v(-42.54, 22.7) * mm, "end": v(-42.35, 22.54) * mm});
            skLineSegment(sketch, "E658", {"start": v(-70.7, 3.71) * mm, "end": v(-70.47, 4.07) * mm});
            skLineSegment(sketch, "E659", {"start": v(-70.47, 4.07) * mm, "end": v(-70.17, 4.26) * mm});
            skLineSegment(sketch, "E660", {"start": v(-70.17, 4.26) * mm, "end": v(-69.36, 3.96) * mm});
            skLineSegment(sketch, "E661", {"start": v(-69.36, 3.96) * mm, "end": v(-69.25, 4.14) * mm});
            skLineSegment(sketch, "E662", {"start": v(-69.25, 4.14) * mm, "end": v(-69.4, 4.38) * mm});
            skLineSegment(sketch, "E663", {"start": v(-69.4, 4.38) * mm, "end": v(-69.37, 4.76) * mm});
            skLineSegment(sketch, "E664", {"start": v(-69.37, 4.76) * mm, "end": v(-69, 4.95) * mm});
            skLineSegment(sketch, "E665", {"start": v(-69, 4.95) * mm, "end": v(-68.68, 5.1) * mm});
            skLineSegment(sketch, "E666", {"start": v(-68.68, 5.1) * mm, "end": v(-68.89, 5.47) * mm});
            skLineSegment(sketch, "E667", {"start": v(-68.89, 5.47) * mm, "end": v(-68.68, 5.68) * mm});
            skLineSegment(sketch, "E668", {"start": v(-68.68, 5.68) * mm, "end": v(-68.61, 5.96) * mm});
            skLineSegment(sketch, "E669", {"start": v(-68.61, 5.96) * mm, "end": v(-68.54, 6.93) * mm});
            skLineSegment(sketch, "E670", {"start": v(-68.54, 6.93) * mm, "end": v(-67.85, 8) * mm});
            skLineSegment(sketch, "E671", {"start": v(-67.85, 8) * mm, "end": v(-67.9, 8.75) * mm});
            skLineSegment(sketch, "E672", {"start": v(-67.9, 8.75) * mm, "end": v(-68.16, 9.13) * mm});
            skLineSegment(sketch, "E673", {"start": v(-68.16, 9.13) * mm, "end": v(-68.03, 9.8) * mm});
            skLineSegment(sketch, "E674", {"start": v(-68.61, 5.96) * mm, "end": v(-67.3, 6.28) * mm});
            skLineSegment(sketch, "E675", {"start": v(-67.3, 6.28) * mm, "end": v(-66.86, 5.94) * mm});
            skLineSegment(sketch, "E676", {"start": v(-66.86, 5.94) * mm, "end": v(-66.72, 6.3) * mm});
            skLineSegment(sketch, "E677", {"start": v(-66.72, 6.3) * mm, "end": v(-66.36, 6.49) * mm});
            skLineSegment(sketch, "E678", {"start": v(-66.36, 6.49) * mm, "end": v(-66.04, 6.21) * mm});
            skLineSegment(sketch, "E679", {"start": v(-66.04, 6.21) * mm, "end": v(-65.87, 6.24) * mm});
            skLineSegment(sketch, "E680", {"start": v(-65.87, 6.24) * mm, "end": v(-65.8, 6.66) * mm});
            skLineSegment(sketch, "E681", {"start": v(-65.8, 6.66) * mm, "end": v(-65.42, 6.9) * mm});
            skLineSegment(sketch, "E682", {"start": v(-65.42, 6.9) * mm, "end": v(-65.28, 6.74) * mm});
            skLineSegment(sketch, "E683", {"start": v(-65.28, 6.74) * mm, "end": v(-64.78, 6.71) * mm});
            skLineSegment(sketch, "E684", {"start": v(-64.78, 6.71) * mm, "end": v(-64.74, 7.29) * mm});
            skLineSegment(sketch, "E685", {"start": v(-64.74, 7.29) * mm, "end": v(-63.86, 8.03) * mm});
            skLineSegment(sketch, "E686", {"start": v(-63.86, 8.03) * mm, "end": v(-63.84, 8.56) * mm});
            skLineSegment(sketch, "E687", {"start": v(-63.84, 8.56) * mm, "end": v(-63.48, 8.54) * mm});
            skLineSegment(sketch, "E688", {"start": v(-63.48, 8.54) * mm, "end": v(-62.78, 8.95) * mm});
            skLineSegment(sketch, "E689", {"start": v(-62.78, 8.95) * mm, "end": v(-62.8, 9.19) * mm});
            skLineSegment(sketch, "E690", {"start": v(-62.8, 9.19) * mm, "end": v(-63.06, 9.38) * mm});
            skLineSegment(sketch, "E691", {"start": v(-63.06, 9.38) * mm, "end": v(-62.92, 9.59) * mm});
            skLineSegment(sketch, "E692", {"start": v(-60.73, -0.29) * mm, "end": v(-60.8, 0.32) * mm});
            skLineSegment(sketch, "E693", {"start": v(-60.8, 0.32) * mm, "end": v(-60.23, 0.5) * mm});
            skLineSegment(sketch, "E694", {"start": v(-60.23, 0.5) * mm, "end": v(-60.25, 0.83) * mm});
            skLineSegment(sketch, "E695", {"start": v(-60.25, 0.83) * mm, "end": v(-59.75, 1.25) * mm});
            skLineSegment(sketch, "E696", {"start": v(-59.75, 1.25) * mm, "end": v(-59.25, 1.28) * mm});
            skLineSegment(sketch, "E697", {"start": v(-59.25, 1.28) * mm, "end": v(-58.88, 1.73) * mm});
            skLineSegment(sketch, "E698", {"start": v(-58.88, 1.73) * mm, "end": v(-58.33, 2) * mm});
            skLineSegment(sketch, "E699", {"start": v(-58.33, 2) * mm, "end": v(-58.3, 2.34) * mm});
            skLineSegment(sketch, "E700", {"start": v(-58.3, 2.34) * mm, "end": v(-57.8, 2.79) * mm});
            skLineSegment(sketch, "E701", {"start": v(-57.8, 2.79) * mm, "end": v(-57.68, 2.62) * mm});
            skLineSegment(sketch, "E702", {"start": v(-57.68, 2.62) * mm, "end": v(-57.46, 2.6) * mm});
            skLineSegment(sketch, "E703", {"start": v(-57.46, 2.6) * mm, "end": v(-57.24, 3.1) * mm});
            skLineSegment(sketch, "E704", {"start": v(-57.24, 3.1) * mm, "end": v(-56.76, 3.1) * mm});
            skLineSegment(sketch, "E705", {"start": v(-56.76, 3.1) * mm, "end": v(-56.6, 3.49) * mm});
            skLineSegment(sketch, "E706", {"start": v(-56.6, 3.49) * mm, "end": v(-56.26, 3.71) * mm});
            skLineSegment(sketch, "E707", {"start": v(-56.26, 3.71) * mm, "end": v(-56.22, 4.26) * mm});
            skLineSegment(sketch, "E708", {"start": v(-59.8, 3.8) * mm, "end": v(-58.62, 4.61) * mm});
            skLineSegment(sketch, "E709", {"start": v(-58.62, 4.61) * mm, "end": v(-58.64, 4.89) * mm});
            skLineSegment(sketch, "E710", {"start": v(-58.64, 4.89) * mm, "end": v(-57.16, 6.47) * mm});
            skLineSegment(sketch, "E711", {"start": v(-57.16, 6.47) * mm, "end": v(-58.09, 7.3) * mm});
            skLineSegment(sketch, "E712", {"start": v(-58.09, 7.3) * mm, "end": v(-58.15, 7.58) * mm});
            skLineSegment(sketch, "E713", {"start": v(-58.15, 7.58) * mm, "end": v(-58.48, 8.5) * mm});
            skLineSegment(sketch, "E714", {"start": v(-58.48, 8.5) * mm, "end": v(-59.1, 8.88) * mm});
            skLineSegment(sketch, "E715", {"start": v(-59.1, 8.88) * mm, "end": v(-59.25, 9.26) * mm});
            skLineSegment(sketch, "E716", {"start": v(-59.25, 9.26) * mm, "end": v(-59.87, 8.76) * mm});
            skLineSegment(sketch, "E717", {"start": v(-59.87, 8.76) * mm, "end": v(-60.02, 8.92) * mm});
            skLineSegment(sketch, "E718", {"start": v(-60.02, 8.92) * mm, "end": v(-60.34, 8.98) * mm});
            skLineSegment(sketch, "E719", {"start": v(-60.34, 8.98) * mm, "end": v(-60.7, 8.76) * mm});
            skLineSegment(sketch, "E720", {"start": v(-60.7, 8.76) * mm, "end": v(-61, 9.04) * mm});
            skLineSegment(sketch, "E721", {"start": v(-61, 9.04) * mm, "end": v(-61.62, 9.06) * mm});
            skLineSegment(sketch, "E722", {"start": v(-61.62, 9.06) * mm, "end": v(-61.92, 9.55) * mm});
            skLineSegment(sketch, "E723", {"start": v(-61.92, 9.55) * mm, "end": v(-62.16, 9.67) * mm});
            skLineSegment(sketch, "E724", {"start": v(-62.16, 9.67) * mm, "end": v(-62.92, 9.59) * mm});
            skLineSegment(sketch, "E725", {"start": v(-46.6, 13.92) * mm, "end": v(-46.17, 14.21) * mm});
            skLineSegment(sketch, "E726", {"start": v(-46.17, 14.21) * mm, "end": v(-45.6, 14.43) * mm});
            skLineSegment(sketch, "E727", {"start": v(-45.6, 14.43) * mm, "end": v(-44.93, 15.36) * mm});
            skLineSegment(sketch, "E728", {"start": v(-44.93, 15.36) * mm, "end": v(-45.54, 15.9) * mm});
            skLineSegment(sketch, "E729", {"start": v(-45.54, 15.9) * mm, "end": v(-45.68, 16.2) * mm});
            skLineSegment(sketch, "E730", {"start": v(-45.68, 16.2) * mm, "end": v(-45.94, 16.2) * mm});
            skLineSegment(sketch, "E731", {"start": v(-45.94, 16.2) * mm, "end": v(-46.07, 16.66) * mm});
            skLineSegment(sketch, "E732", {"start": v(-46.07, 16.66) * mm, "end": v(-45.83, 16.76) * mm});
            skLineSegment(sketch, "E733", {"start": v(-45.83, 16.76) * mm, "end": v(-45.84, 17.02) * mm});
            skLineSegment(sketch, "E734", {"start": v(-45.84, 17.02) * mm, "end": v(-46.03, 17.15) * mm});
            skLineSegment(sketch, "E735", {"start": v(-46.03, 17.15) * mm, "end": v(-45.76, 17.64) * mm});
            skLineSegment(sketch, "E736", {"start": v(-45.76, 17.64) * mm, "end": v(-45.7, 18.04) * mm});
            skLineSegment(sketch, "E737", {"start": v(-45.7, 18.04) * mm, "end": v(-45.48, 18.25) * mm});
            skLineSegment(sketch, "E738", {"start": v(-45.97, 14.3) * mm, "end": v(-46.06, 13.71) * mm});
            skLineSegment(sketch, "E739", {"start": v(-46.06, 13.71) * mm, "end": v(-45.74, 13.33) * mm});
            skLineSegment(sketch, "E740", {"start": v(-45.74, 13.33) * mm, "end": v(-45.09, 12.99) * mm});
            skLineSegment(sketch, "E741", {"start": v(-45.09, 12.99) * mm, "end": v(-44.61, 12.92) * mm});
            skLineSegment(sketch, "E742", {"start": v(-44.61, 12.92) * mm, "end": v(-44.62, 12.7) * mm});
            skLineSegment(sketch, "E743", {"start": v(-44.62, 12.7) * mm, "end": v(-44.69, 12.65) * mm});
            skLineSegment(sketch, "E744", {"start": v(-44.69, 12.65) * mm, "end": v(-44.68, 12.33) * mm});
            skLineSegment(sketch, "E745", {"start": v(-44.68, 12.33) * mm, "end": v(-44.35, 12.57) * mm});
            skLineSegment(sketch, "E746", {"start": v(-44.35, 12.57) * mm, "end": v(-44.26, 13.06) * mm});
            skLineSegment(sketch, "E747", {"start": v(-44.26, 13.06) * mm, "end": v(-43.84, 13.77) * mm});
            skLineSegment(sketch, "E748", {"start": v(-43.84, 13.77) * mm, "end": v(-43.53, 14.51) * mm});
            skLineSegment(sketch, "E749", {"start": v(-43.53, 14.51) * mm, "end": v(-43.57, 15.08) * mm});
            skLineSegment(sketch, "E750", {"start": v(-43.57, 15.08) * mm, "end": v(-43.57, 16.15) * mm});
            skLineSegment(sketch, "E751", {"start": v(-43.57, 16.15) * mm, "end": v(-43.74, 16.44) * mm});
            skLineSegment(sketch, "E752", {"start": v(-43.74, 16.44) * mm, "end": v(-44.14, 16.3) * mm});
            skLineSegment(sketch, "E753", {"start": v(-44.14, 16.3) * mm, "end": v(-44.2, 16.41) * mm});
            skLineSegment(sketch, "E754", {"start": v(-44.2, 16.41) * mm, "end": v(-43.9, 16.67) * mm});
            skLineSegment(sketch, "E755", {"start": v(-43.9, 16.67) * mm, "end": v(-43.84, 16.86) * mm});
            skLineSegment(sketch, "E756", {"start": v(-58.48, 8.5) * mm, "end": v(-58.14, 8.63) * mm});
            skLineSegment(sketch, "E757", {"start": v(-58.14, 8.63) * mm, "end": v(-58.07, 9) * mm});
            skLineSegment(sketch, "E758", {"start": v(-58.07, 9) * mm, "end": v(-57.92, 9.06) * mm});
            skLineSegment(sketch, "E759", {"start": v(-57.92, 9.06) * mm, "end": v(-57.83, 10.05) * mm});
            skLineSegment(sketch, "E760", {"start": v(-57.83, 10.05) * mm, "end": v(-57.6, 10.1) * mm});
            skLineSegment(sketch, "E761", {"start": v(-57.6, 10.1) * mm, "end": v(-57.43, 9.85) * mm});
            skLineSegment(sketch, "E762", {"start": v(-57.43, 9.85) * mm, "end": v(-57.23, 9.95) * mm});
            skLineSegment(sketch, "E763", {"start": v(-57.23, 9.95) * mm, "end": v(-57.22, 10.1) * mm});
            skLineSegment(sketch, "E764", {"start": v(-57.22, 10.1) * mm, "end": v(-57.39, 10.37) * mm});
            skLineSegment(sketch, "E765", {"start": v(-57.39, 10.37) * mm, "end": v(-56.79, 11.25) * mm});
            skLineSegment(sketch, "E766", {"start": v(-56.79, 11.25) * mm, "end": v(-56.62, 11.17) * mm});
            skLineSegment(sketch, "E767", {"start": v(-56.62, 11.17) * mm, "end": v(-55.75, 12.1) * mm});
            skLineSegment(sketch, "E768", {"start": v(-55.75, 12.1) * mm, "end": v(-55.67, 13.85) * mm});
            skLineSegment(sketch, "E769", {"start": v(-55.67, 13.85) * mm, "end": v(-55.83, 14.27) * mm});
            skLineSegment(sketch, "E770", {"start": v(-55.83, 14.27) * mm, "end": v(-55.53, 14.45) * mm});
            skLineSegment(sketch, "E771", {"start": v(-61.24, 16.34) * mm, "end": v(-60.6, 16.08) * mm});
            skLineSegment(sketch, "E772", {"start": v(-60.6, 16.08) * mm, "end": v(-60.01, 16.1) * mm});
            skLineSegment(sketch, "E773", {"start": v(-60.01, 16.1) * mm, "end": v(-59.6, 15.8) * mm});
            skLineSegment(sketch, "E774", {"start": v(-59.6, 15.8) * mm, "end": v(-59.36, 15.84) * mm});
            skLineSegment(sketch, "E775", {"start": v(-59.36, 15.84) * mm, "end": v(-58.75, 16.12) * mm});
            skLineSegment(sketch, "E776", {"start": v(-58.75, 16.12) * mm, "end": v(-58.06, 16.23) * mm});
            skLineSegment(sketch, "E777", {"start": v(-58.06, 16.23) * mm, "end": v(-57.25, 17.07) * mm});
            skLineSegment(sketch, "E778", {"start": v(-57.25, 17.07) * mm, "end": v(-56.04, 17.76) * mm});
            skLineSegment(sketch, "E779", {"start": v(-75.47, 19.43) * mm, "end": v(-75.6, 20.26) * mm});
            skLineSegment(sketch, "E780", {"start": v(-75.6, 20.26) * mm, "end": v(-75.73, 20.55) * mm});
            skLineSegment(sketch, "E781", {"start": v(-75.73, 20.55) * mm, "end": v(-76.5, 20.95) * mm});
            skLineSegment(sketch, "E782", {"start": v(-76.5, 20.95) * mm, "end": v(-76.93, 21.65) * mm});
            skLineSegment(sketch, "E783", {"start": v(-76.93, 21.65) * mm, "end": v(-77.45, 21.7) * mm});
            skLineSegment(sketch, "E784", {"start": v(-77.45, 21.7) * mm, "end": v(-77.58, 22.08) * mm});
            skLineSegment(sketch, "E785", {"start": v(-77.58, 22.08) * mm, "end": v(-77.84, 22.06) * mm});
            skLineSegment(sketch, "E786", {"start": v(-77.84, 22.06) * mm, "end": v(-78.16, 22.33) * mm});
            skLineSegment(sketch, "E787", {"start": v(-78.16, 22.33) * mm, "end": v(-78.28, 23.59) * mm});
            skLineSegment(sketch, "E788", {"start": v(-78.28, 23.59) * mm, "end": v(-78.11, 23.84) * mm});
            skLineSegment(sketch, "E789", {"start": v(-78.11, 23.84) * mm, "end": v(-78.16, 24.27) * mm});
            skLineSegment(sketch, "E790", {"start": v(-78.16, 24.27) * mm, "end": v(-78.5, 24.49) * mm});
            skLineSegment(sketch, "E791", {"start": v(-78.5, 24.49) * mm, "end": v(-78.24, 25.2) * mm});
            skLineSegment(sketch, "E792", {"start": v(-78.24, 25.2) * mm, "end": v(-77.53, 25.72) * mm});
            skLineSegment(sketch, "E793", {"start": v(-77.53, 25.72) * mm, "end": v(-77.53, 27.01) * mm});
            skLineSegment(sketch, "E794", {"start": v(-77.53, 27.01) * mm, "end": v(-77.24, 27.25) * mm});
            skLineSegment(sketch, "E795", {"start": v(-74.3, 27.08) * mm, "end": v(-73.9, 26.42) * mm});
            skLineSegment(sketch, "E796", {"start": v(-73.9, 26.42) * mm, "end": v(-73.2, 26.35) * mm});
            skLineSegment(sketch, "E797", {"start": v(-73.2, 26.35) * mm, "end": v(-72.04, 26.05) * mm});
            skLineSegment(sketch, "E798", {"start": v(-72.04, 26.05) * mm, "end": v(-71.77, 25.87) * mm});
            skLineSegment(sketch, "E799", {"start": v(-71.77, 25.87) * mm, "end": v(-70.36, 25.63) * mm});
            skLineSegment(sketch, "E800", {"start": v(-70.36, 25.63) * mm, "end": v(-70.27, 25.35) * mm});
            skLineSegment(sketch, "E801", {"start": v(-70.27, 25.35) * mm, "end": v(-69.85, 25.23) * mm});
            skLineSegment(sketch, "E802", {"start": v(-69.85, 25.23) * mm, "end": v(-69.73, 24.15) * mm});
            skLineSegment(sketch, "E803", {"start": v(-69.73, 24.15) * mm, "end": v(-69.38, 23.82) * mm});
            skLineSegment(sketch, "E804", {"start": v(-68.86, 27.28) * mm, "end": v(-68.72, 27.38) * mm});
            skLineSegment(sketch, "E805", {"start": v(-68.72, 27.38) * mm, "end": v(-68.43, 27.16) * mm});
            skLineSegment(sketch, "E806", {"start": v(-68.43, 27.16) * mm, "end": v(-68.2, 27.31) * mm});
            skLineSegment(sketch, "E807", {"start": v(-68.2, 27.31) * mm, "end": v(-68.04, 27.24) * mm});
            skLineSegment(sketch, "E808", {"start": v(-68.04, 27.24) * mm, "end": v(-67.43, 27.78) * mm});
            skLineSegment(sketch, "E809", {"start": v(-67.43, 27.78) * mm, "end": v(-67.02, 27.9) * mm});
            skLineSegment(sketch, "E810", {"start": v(-67.02, 27.9) * mm, "end": v(-66.4, 27.94) * mm});
            skLineSegment(sketch, "E811", {"start": v(-66.4, 27.94) * mm, "end": v(-65.61, 28.27) * mm});
            skLineSegment(sketch, "E812", {"start": v(-65.61, 28.27) * mm, "end": v(-65.42, 28.23) * mm});
            skLineSegment(sketch, "E813", {"start": v(-65.42, 28.23) * mm, "end": v(-65.44, 27.65) * mm});
            skLineSegment(sketch, "E814", {"start": v(-65.44, 27.65) * mm, "end": v(-65, 27.51) * mm});
            skLineSegment(sketch, "E815", {"start": v(-65, 27.51) * mm, "end": v(-64.12, 27.76) * mm});
            skLineSegment(sketch, "E816", {"start": v(-64.12, 27.76) * mm, "end": v(-64.03, 27.88) * mm});
            skLineSegment(sketch, "E817", {"start": v(-64.03, 27.88) * mm, "end": v(-63.87, 27.82) * mm});
            skLineSegment(sketch, "E818", {"start": v(-63.87, 27.82) * mm, "end": v(-63.87, 27.1) * mm});
            skLineSegment(sketch, "E819", {"start": v(-63.87, 27.1) * mm, "end": v(-63.34, 26.55) * mm});
            skLineSegment(sketch, "E820", {"start": v(-63.34, 26.55) * mm, "end": v(-63.8, 26.56) * mm});
            skLineSegment(sketch, "E821", {"start": v(-63.8, 26.56) * mm, "end": v(-64, 26.49) * mm});
            skLineSegment(sketch, "E822", {"start": v(-64, 26.49) * mm, "end": v(-64.34, 26.52) * mm});
            skLineSegment(sketch, "E823", {"start": v(-64.34, 26.52) * mm, "end": v(-64.65, 26.34) * mm});
            skLineSegment(sketch, "E824", {"start": v(-64.65, 26.34) * mm, "end": v(-65.37, 26.47) * mm});
            skLineSegment(sketch, "E825", {"start": v(-65.37, 26.47) * mm, "end": v(-66.08, 26.47) * mm});
            skLineSegment(sketch, "E826", {"start": v(-66.08, 26.47) * mm, "end": v(-66.27, 26.19) * mm});
            skLineSegment(sketch, "E827", {"start": v(-66.27, 26.19) * mm, "end": v(-67.3, 26.07) * mm});
            skLineSegment(sketch, "E828", {"start": v(-67.3, 26.07) * mm, "end": v(-67.51, 25.65) * mm});
            skLineSegment(sketch, "E829", {"start": v(-67.51, 25.65) * mm, "end": v(-67.6, 25.59) * mm});
            skLineSegment(sketch, "E830", {"start": v(-67.6, 25.59) * mm, "end": v(-67.86, 25.75) * mm});
            skLineSegment(sketch, "E831", {"start": v(-67.86, 25.75) * mm, "end": v(-68.37, 25.51) * mm});
            skLineSegment(sketch, "E832", {"start": v(-68.37, 25.51) * mm, "end": v(-68.6, 25.7) * mm});
            skLineSegment(sketch, "E833", {"start": v(-68.6, 25.7) * mm, "end": v(-68.65, 25.68) * mm});
            skLineSegment(sketch, "E834", {"start": v(-68.65, 25.68) * mm, "end": v(-69.38, 23.82) * mm});
            skLineSegment(sketch, "E835", {"start": v(-69.38, 23.82) * mm, "end": v(-70.08, 22.7) * mm});
            skLineSegment(sketch, "E836", {"start": v(-70.08, 22.7) * mm, "end": v(-70.04, 22.46) * mm});
            skLineSegment(sketch, "E837", {"start": v(-70.04, 22.46) * mm, "end": v(-69.86, 22.4) * mm});
            skLineSegment(sketch, "E838", {"start": v(-69.86, 22.4) * mm, "end": v(-69.8, 22.67) * mm});
            skLineSegment(sketch, "E839", {"start": v(-69.8, 22.67) * mm, "end": v(-69.29, 23.1) * mm});
            skLineSegment(sketch, "E840", {"start": v(-69.29, 23.1) * mm, "end": v(-68.48, 24.32) * mm});
            skLineSegment(sketch, "E841", {"start": v(-68.48, 24.32) * mm, "end": v(-68.39, 24.02) * mm});
            skLineSegment(sketch, "E842", {"start": v(-68.39, 24.02) * mm, "end": v(-69.06, 22.64) * mm});
            skLineSegment(sketch, "E843", {"start": v(-69.06, 22.64) * mm, "end": v(-69.18, 21.98) * mm});
            skLineSegment(sketch, "E844", {"start": v(-69.18, 21.98) * mm, "end": v(-69.09, 21.88) * mm});
            skLineSegment(sketch, "E845", {"start": v(-69.09, 21.88) * mm, "end": v(-69.05, 21.62) * mm});
            skLineSegment(sketch, "E846", {"start": v(-69.05, 21.62) * mm, "end": v(-69.38, 21.17) * mm});
            skLineSegment(sketch, "E847", {"start": v(-69.38, 21.17) * mm, "end": v(-69.22, 20.28) * mm});
            skLineSegment(sketch, "E848", {"start": v(-69.22, 20.28) * mm, "end": v(-69.57, 19.32) * mm});
            skLineSegment(sketch, "E849", {"start": v(-69.57, 19.32) * mm, "end": v(-69.44, 18.92) * mm});
            skLineSegment(sketch, "E850", {"start": v(-69.44, 18.92) * mm, "end": v(-69.4, 18.33) * mm});
            skLineSegment(sketch, "E851", {"start": v(-69.4, 18.33) * mm, "end": v(-69.2, 17.9) * mm});
            skLineSegment(sketch, "E852", {"start": v(-69.2, 17.9) * mm, "end": v(-69.3, 17.4) * mm});
            skLineSegment(sketch, "E853", {"start": v(-39.63, 23.53) * mm, "end": v(-39.47, 24.1) * mm});
            skLineSegment(sketch, "E854", {"start": v(-39.47, 24.1) * mm, "end": v(-39.77, 24.21) * mm});
            skLineSegment(sketch, "E855", {"start": v(-39.77, 24.21) * mm, "end": v(-39.78, 24.55) * mm});
            skLineSegment(sketch, "E856", {"start": v(-39.78, 24.55) * mm, "end": v(-40.18, 24.66) * mm});
            skLineSegment(sketch, "E857", {"start": v(-40.18, 24.66) * mm, "end": v(-41.63, 29.13) * mm});
            skLineSegment(sketch, "E858", {"start": v(-41.63, 29.13) * mm, "end": v(-41.7, 28.87) * mm});
            skLineSegment(sketch, "E859", {"start": v(-41.7, 28.87) * mm, "end": v(-41.9, 29.05) * mm});
            skLineSegment(sketch, "E860", {"start": v(-41.9, 29.05) * mm, "end": v(-42.01, 29) * mm});
            skLineSegment(sketch, "E861", {"start": v(-42.01, 29) * mm, "end": v(-42.22, 28.28) * mm});
            skLineSegment(sketch, "E862", {"start": v(-41.63, 29.13) * mm, "end": v(-41.48, 29.17) * mm});
            skLineSegment(sketch, "E863", {"start": v(-41.48, 29.17) * mm, "end": v(-41.1, 29.1) * mm});
            skLineSegment(sketch, "E864", {"start": v(-41.1, 29.1) * mm, "end": v(-41.02, 30.07) * mm});
            skLineSegment(sketch, "E865", {"start": v(-41.02, 30.07) * mm, "end": v(-40.57, 31.09) * mm});
            skLineSegment(sketch, "E866", {"start": v(-40.57, 31.09) * mm, "end": v(-40.79, 31.32) * mm});
            skLineSegment(sketch, "E867", {"start": v(-40.79, 31.32) * mm, "end": v(-40.79, 31.97) * mm});
            skLineSegment(sketch, "E868", {"start": v(-40.79, 31.97) * mm, "end": v(-40.6, 32.3) * mm});
            skLineSegment(sketch, "E869", {"start": v(-40.6, 32.3) * mm, "end": v(-40.6, 33.16) * mm});
            skLineSegment(sketch, "E870", {"start": v(-40.6, 33.16) * mm, "end": v(-39.94, 35) * mm});
            skLineSegment(sketch, "E871", {"start": v(-39.94, 35) * mm, "end": v(-39.77, 35) * mm});
            skLineSegment(sketch, "E872", {"start": v(-39.77, 35) * mm, "end": v(-39.56, 34.6) * mm});
            skLineSegment(sketch, "E873", {"start": v(-39.56, 34.6) * mm, "end": v(-39.2, 34.53) * mm});
            skLineSegment(sketch, "E874", {"start": v(-39.2, 34.53) * mm, "end": v(-39.06, 34.66) * mm});
            skLineSegment(sketch, "E875", {"start": v(-39.06, 34.66) * mm, "end": v(-39.09, 34.83) * mm});
            skLineSegment(sketch, "E876", {"start": v(-39.09, 34.83) * mm, "end": v(-38.46, 35.26) * mm});
            skLineSegment(sketch, "E877", {"start": v(-38.46, 35.26) * mm, "end": v(-37.51, 34.92) * mm});
            skLineSegment(sketch, "E878", {"start": v(-37.51, 34.92) * mm, "end": v(-36.5, 31.57) * mm});
            skLineSegment(sketch, "E879", {"start": v(-36.5, 31.57) * mm, "end": v(-35.89, 31.59) * mm});
            skLineSegment(sketch, "E880", {"start": v(-35.89, 31.59) * mm, "end": v(-35.77, 31.46) * mm});
            skLineSegment(sketch, "E881", {"start": v(-35.77, 31.46) * mm, "end": v(-35.8, 30.87) * mm});
            skLineSegment(sketch, "E882", {"start": v(-35.8, 30.87) * mm, "end": v(-35.45, 30.57) * mm});
            skLineSegment(sketch, "E883", {"start": v(-35.45, 30.57) * mm, "end": v(-35.26, 30.56) * mm});
            skLineSegment(sketch, "E884", {"start": v(-35.26, 30.56) * mm, "end": v(-35.22, 30.75) * mm});
            skLineSegment(sketch, "E885", {"start": v(-35.22, 30.75) * mm, "end": v(-34.96, 30.78) * mm});
            skLineSegment(sketch, "E886", {"start": v(-34.96, 30.78) * mm, "end": v(-34.51, 30.12) * mm});
            skLineSegment(sketch, "E887", {"start": v(-34.51, 30.12) * mm, "end": v(-34.77, 29.42) * mm});
            skLineSegment(sketch, "E888", {"start": v(-34.77, 29.42) * mm, "end": v(-34.95, 29.42) * mm});
            skLineSegment(sketch, "E889", {"start": v(-34.95, 29.42) * mm, "end": v(-35.9, 28.38) * mm});
            skLineSegment(sketch, "E890", {"start": v(-35.9, 28.38) * mm, "end": v(-36.07, 28.5) * mm});
            skLineSegment(sketch, "E891", {"start": v(-36.07, 28.5) * mm, "end": v(-36.16, 28.66) * mm});
            skLineSegment(sketch, "E892", {"start": v(-36.16, 28.66) * mm, "end": v(-36.39, 28.65) * mm});
            skLineSegment(sketch, "E893", {"start": v(-36.39, 28.65) * mm, "end": v(-36.45, 28.48) * mm});
            skLineSegment(sketch, "E894", {"start": v(-36.45, 28.48) * mm, "end": v(-36.75, 28.15) * mm});
            skLineSegment(sketch, "E895", {"start": v(-36.75, 28.15) * mm, "end": v(-36.7, 27.98) * mm});
            skLineSegment(sketch, "E896", {"start": v(-36.7, 27.98) * mm, "end": v(-36.7, 27.64) * mm});
            skLineSegment(sketch, "E897", {"start": v(-36.7, 27.64) * mm, "end": v(-36.92, 27.66) * mm});
            skLineSegment(sketch, "E898", {"start": v(-36.92, 27.66) * mm, "end": v(-36.98, 27.91) * mm});
            skLineSegment(sketch, "E899", {"start": v(-37.17, 27.92) * mm, "end": v(-37.38, 28.27) * mm});
            skLineSegment(sketch, "E900", {"start": v(-37.38, 28.27) * mm, "end": v(-37.57, 28.17) * mm});
            skLineSegment(sketch, "E901", {"start": v(-37.57, 28.17) * mm, "end": v(-37.45, 27.98) * mm});
            skLineSegment(sketch, "E902", {"start": v(-37.45, 27.98) * mm, "end": v(-37.48, 27.54) * mm});
            skLineSegment(sketch, "E903", {"start": v(-37.48, 27.54) * mm, "end": v(-37.47, 27.21) * mm});
            skLineSegment(sketch, "E904", {"start": v(-37.47, 27.21) * mm, "end": v(-37.64, 26.92) * mm});
            skLineSegment(sketch, "E905", {"start": v(-37.64, 26.92) * mm, "end": v(-37.84, 26.9) * mm});
            skLineSegment(sketch, "E906", {"start": v(-37.84, 26.9) * mm, "end": v(-37.96, 26.88) * mm});
            skLineSegment(sketch, "E907", {"start": v(-37.96, 26.88) * mm, "end": v(-37.96, 26.56) * mm});
            skLineSegment(sketch, "E908", {"start": v(-37.96, 26.56) * mm, "end": v(-38.71, 26.16) * mm});
            skLineSegment(sketch, "E909", {"start": v(-38.71, 26.16) * mm, "end": v(-38.94, 26.27) * mm});
            skLineSegment(sketch, "E910", {"start": v(-38.94, 26.27) * mm, "end": v(-39.24, 25.92) * mm});
            skLineSegment(sketch, "E911", {"start": v(-39.24, 25.92) * mm, "end": v(-39.16, 25.54) * mm});
            skLineSegment(sketch, "E912", {"start": v(-39.16, 25.54) * mm, "end": v(-39.27, 25.44) * mm});
            skLineSegment(sketch, "E913", {"start": v(-39.27, 25.44) * mm, "end": v(-39.47, 24.1) * mm});
            skLineSegment(sketch, "E914", {"start": v(-37.17, 27.92) * mm, "end": v(-36.98, 27.91) * mm});
            skLineSegment(sketch, "E915", {"start": v(-53.3, 12.67) * mm, "end": v(-53.07, 11.4) * mm});
            skLineSegment(sketch, "E916", {"start": v(-53.07, 11.4) * mm, "end": v(-52.55, 12.1) * mm});
            skLineSegment(sketch, "E917", {"start": v(-52.55, 12.1) * mm, "end": v(-52.21, 12.03) * mm});
            skLineSegment(sketch, "E918", {"start": v(-52.21, 12.03) * mm, "end": v(-51.88, 12.5) * mm});
            skLineSegment(sketch, "E919", {"start": v(-51.88, 12.5) * mm, "end": v(-51.65, 12.42) * mm});
            skLineSegment(sketch, "E920", {"start": v(-51.65, 12.42) * mm, "end": v(-51.45, 12.48) * mm});
            skLineSegment(sketch, "E921", {"start": v(-61.24, 16.34) * mm, "end": v(-60.9, 17.2) * mm});
            skLineSegment(sketch, "E922", {"start": v(-60.9, 17.2) * mm, "end": v(-60.82, 17.8) * mm});
            skLineSegment(sketch, "E923", {"start": v(-60.82, 17.8) * mm, "end": v(-60.5, 18.1) * mm});
            skLineSegment(sketch, "E924", {"start": v(-60.5, 18.1) * mm, "end": v(-60.39, 18.51) * mm});
            skLineSegment(sketch, "E925", {"start": v(-60.39, 18.51) * mm, "end": v(-60.1, 18.93) * mm});
            skLineSegment(sketch, "E926", {"start": v(-60.1, 18.93) * mm, "end": v(-59.93, 19.56) * mm});
            skLineSegment(sketch, "E927", {"start": v(-59.93, 19.56) * mm, "end": v(-60.03, 20.15) * mm});
            skLineSegment(sketch, "E928", {"start": v(-60.03, 20.15) * mm, "end": v(-60.33, 21.08) * mm});
            skLineSegment(sketch, "E929", {"start": v(-60.33, 21.08) * mm, "end": v(-60.49, 21.73) * mm});
            skLineSegment(sketch, "E930", {"start": v(-60.49, 21.73) * mm, "end": v(-61, 22.27) * mm});
            skLineSegment(sketch, "E931", {"start": v(-61, 22.27) * mm, "end": v(-61.6, 21.93) * mm});
            skLineSegment(sketch, "E932", {"start": v(-61.6, 21.93) * mm, "end": v(-61.8, 21.28) * mm});
            skLineSegment(sketch, "E933", {"start": v(-61.8, 21.28) * mm, "end": v(-62.19, 20.9) * mm});
            skLineSegment(sketch, "E934", {"start": v(-62.19, 20.9) * mm, "end": v(-62.72, 21.1) * mm});
            skLineSegment(sketch, "E935", {"start": v(-62.72, 21.1) * mm, "end": v(-62.62, 21.75) * mm});
            skLineSegment(sketch, "E936", {"start": v(-62.62, 21.75) * mm, "end": v(-62.2, 21.87) * mm});
            skLineSegment(sketch, "E937", {"start": v(-62.2, 21.87) * mm, "end": v(-62.13, 22.54) * mm});
            skLineSegment(sketch, "E938", {"start": v(-62.13, 22.54) * mm, "end": v(-61.83, 22.68) * mm});
            skLineSegment(sketch, "E939", {"start": v(-61.83, 22.68) * mm, "end": v(-61.87, 23.79) * mm});
            skLineSegment(sketch, "E940", {"start": v(-61.87, 23.79) * mm, "end": v(-62.26, 24.17) * mm});
            skLineSegment(sketch, "E941", {"start": v(-62.26, 24.17) * mm, "end": v(-62.3, 24.34) * mm});
            skLineSegment(sketch, "E942", {"start": v(-62.3, 24.34) * mm, "end": v(-62.2, 24.52) * mm});
            skLineSegment(sketch, "E943", {"start": v(-62.2, 24.52) * mm, "end": v(-62.03, 24.48) * mm});
            skLineSegment(sketch, "E944", {"start": v(-62.03, 24.48) * mm, "end": v(-61.99, 24.62) * mm});
            skLineSegment(sketch, "E945", {"start": v(-61.99, 24.62) * mm, "end": v(-62.4, 25.17) * mm});
            skLineSegment(sketch, "E946", {"start": v(-62.4, 25.17) * mm, "end": v(-62.86, 25.21) * mm});
            skLineSegment(sketch, "E947", {"start": v(-62.86, 25.21) * mm, "end": v(-63.73, 25.69) * mm});
            skLineSegment(sketch, "E948", {"start": v(-63.73, 25.69) * mm, "end": v(-64.08, 25.73) * mm});
            skLineSegment(sketch, "E949", {"start": v(-64.08, 25.73) * mm, "end": v(-64.24, 25.63) * mm});
            skLineSegment(sketch, "E950", {"start": v(-64.24, 25.63) * mm, "end": v(-64.6, 25.92) * mm});
            skLineSegment(sketch, "E951", {"start": v(-64.6, 25.92) * mm, "end": v(-65.29, 25.55) * mm});
            skLineSegment(sketch, "E952", {"start": v(-65.29, 25.55) * mm, "end": v(-65.25, 25.13) * mm});
            skLineSegment(sketch, "E953", {"start": v(-65.25, 25.13) * mm, "end": v(-65, 25.07) * mm});
            skLineSegment(sketch, "E954", {"start": v(-65, 25.07) * mm, "end": v(-64.83, 24.9) * mm});
            skLineSegment(sketch, "E955", {"start": v(-64.83, 24.9) * mm, "end": v(-65.1, 24.78) * mm});
            skLineSegment(sketch, "E956", {"start": v(-65.1, 24.78) * mm, "end": v(-65.3, 24.82) * mm});
            skLineSegment(sketch, "E957", {"start": v(-65.3, 24.82) * mm, "end": v(-65.55, 24.54) * mm});
            skLineSegment(sketch, "E958", {"start": v(-65.55, 24.54) * mm, "end": v(-65.49, 23.61) * mm});
            skLineSegment(sketch, "E959", {"start": v(-65.49, 23.61) * mm, "end": v(-65.96, 23.3) * mm});
            skLineSegment(sketch, "E960", {"start": v(-65.96, 23.3) * mm, "end": v(-66.06, 23.79) * mm});
            skLineSegment(sketch, "E961", {"start": v(-66.06, 23.79) * mm, "end": v(-65.76, 24.3) * mm});
            skLineSegment(sketch, "E962", {"start": v(-65.76, 24.3) * mm, "end": v(-65.88, 24.42) * mm});
            skLineSegment(sketch, "E963", {"start": v(-65.88, 24.42) * mm, "end": v(-66.1, 24.34) * mm});
            skLineSegment(sketch, "E964", {"start": v(-66.1, 24.34) * mm, "end": v(-66.22, 23.95) * mm});
            skLineSegment(sketch, "E965", {"start": v(-66.22, 23.95) * mm, "end": v(-66.7, 23.57) * mm});
            skLineSegment(sketch, "E966", {"start": v(-66.7, 23.57) * mm, "end": v(-66.67, 23.41) * mm});
            skLineSegment(sketch, "E967", {"start": v(-66.67, 23.41) * mm, "end": v(-66.7, 23.08) * mm});
            skLineSegment(sketch, "E968", {"start": v(-66.7, 23.08) * mm, "end": v(-66.97, 23.06) * mm});
            skLineSegment(sketch, "E969", {"start": v(-66.97, 23.06) * mm, "end": v(-66.87, 22.6) * mm});
            skLineSegment(sketch, "E970", {"start": v(-66.87, 22.6) * mm, "end": v(-67.17, 21.6) * mm});
            skLineSegment(sketch, "E971", {"start": v(-67.17, 21.6) * mm, "end": v(-67.05, 20.83) * mm});
            skLineSegment(sketch, "E972", {"start": v(-67.05, 20.83) * mm, "end": v(-67.28, 20.25) * mm});
            skLineSegment(sketch, "E973", {"start": v(-67.28, 20.25) * mm, "end": v(-66.34, 18.35) * mm});
            skLineSegment(sketch, "E974", {"start": v(-66.34, 18.35) * mm, "end": v(-66.71, 16.68) * mm});
            skLineSegment(sketch, "E975", {"start": v(-66.71, 16.68) * mm, "end": v(-66.87, 16.2) * mm});
            skLineSegment(sketch, "E976", {"start": v(-66.87, 16.2) * mm, "end": v(-67.28, 15.71) * mm});
            skLineSegment(sketch, "E977", {"start": v(-51.45, 12.48) * mm, "end": v(-50.84, 12.92) * mm});
            skLineSegment(sketch, "E978", {"start": v(-50.84, 12.92) * mm, "end": v(-49.9, 12.33) * mm});
            skLineSegment(sketch, "E979", {"start": v(-49.9, 12.33) * mm, "end": v(-49.97, 11.76) * mm});
            skLineSegment(sketch, "E980", {"start": v(-49.97, 11.76) * mm, "end": v(-51.03, 12.24) * mm});
            skLineSegment(sketch, "E981", {"start": v(-51.03, 12.24) * mm, "end": v(-51.13, 11.58) * mm});
            skLineSegment(sketch, "E982", {"start": v(-51.13, 11.58) * mm, "end": v(-51.47, 10.96) * mm});
            skLineSegment(sketch, "E983", {"start": v(-51.47, 10.96) * mm, "end": v(-51.77, 10.74) * mm});
            skLineSegment(sketch, "E984", {"start": v(-51.77, 10.74) * mm, "end": v(-51.8, 10.48) * mm});
            skLineSegment(sketch, "E985", {"start": v(-51.8, 10.48) * mm, "end": v(-52.22, 10.4) * mm});
            skLineSegment(sketch, "E986", {"start": v(-52.22, 10.4) * mm, "end": v(-52.3, 9.51) * mm});
            skLineSegment(sketch, "E987", {"start": v(-52.3, 9.51) * mm, "end": v(-52.94, 9.82) * mm});
            skLineSegment(sketch, "E988", {"start": v(-52.94, 9.82) * mm, "end": v(-53.18, 9.8) * mm});
            skLineSegment(sketch, "E989", {"start": v(-57.16, 6.47) * mm, "end": v(-56.6, 5.94) * mm});
            skLineSegment(sketch, "E990", {"start": v(-56.6, 5.94) * mm, "end": v(-56.15, 5.84) * mm});
            skLineSegment(sketch, "E991", {"start": v(-56.15, 5.84) * mm, "end": v(-55.87, 6.2) * mm});
            skLineSegment(sketch, "E992", {"start": v(-55.87, 6.2) * mm, "end": v(-55.75, 6.01) * mm});
            skLineSegment(sketch, "E993", {"start": v(-55.75, 6.01) * mm, "end": v(-55.13, 6.1) * mm});
            skLineSegment(sketch, "E994", {"start": v(-55.13, 6.1) * mm, "end": v(-54.99, 6.64) * mm});
            skLineSegment(sketch, "E995", {"start": v(-54.99, 6.64) * mm, "end": v(-54.66, 6.57) * mm});
            skLineSegment(sketch, "E996", {"start": v(-54.66, 6.57) * mm, "end": v(-54.31, 6.8) * mm});
            skLineSegment(sketch, "E997", {"start": v(-54.31, 6.8) * mm, "end": v(-54.09, 6.76) * mm});
            skLineSegment(sketch, "E998", {"start": v(-54.09, 6.76) * mm, "end": v(-53.88, 7.23) * mm});
            skLineSegment(sketch, "E999", {"start": v(-53.88, 7.23) * mm, "end": v(-54.03, 7.4) * mm});
            skLineSegment(sketch, "E1000", {"start": v(-54.03, 7.4) * mm, "end": v(-53.17, 9.3) * mm});
            skLineSegment(sketch, "E1001", {"start": v(-53.17, 9.3) * mm, "end": v(-53.18, 9.8) * mm});
            skLineSegment(sketch, "E1002", {"start": v(-46.06, 13.71) * mm, "end": v(-46.18, 13.78) * mm});
            skLineSegment(sketch, "E1003", {"start": v(-46.18, 13.78) * mm, "end": v(-46.23, 13.6) * mm});
            skLineSegment(sketch, "E1004", {"start": v(-46.23, 13.6) * mm, "end": v(-45.95, 13.22) * mm});
            skLineSegment(sketch, "E1005", {"start": v(-45.95, 13.22) * mm, "end": v(-45.74, 13.14) * mm});
            skLineSegment(sketch, "E1006", {"start": v(-45.74, 13.14) * mm, "end": v(-45.3, 12.2) * mm});
            skLineSegment(sketch, "E1007", {"start": v(-45.3, 12.2) * mm, "end": v(-44.92, 11.92) * mm});
            skLineSegment(sketch, "E1008", {"start": v(-44.92, 11.92) * mm, "end": v(-44.8, 11.98) * mm});
            skLineSegment(sketch, "E1009", {"start": v(-44.8, 11.98) * mm, "end": v(-44.58, 11.22) * mm});
            skLineSegment(sketch, "E1010", {"start": v(-44.58, 11.22) * mm, "end": v(-44.57, 10.53) * mm});
            skLineSegment(sketch, "E1011", {"start": v(-44.57, 10.53) * mm, "end": v(-44.81, 9.7) * mm});
            skLineSegment(sketch, "E1012", {"start": v(-44.81, 9.7) * mm, "end": v(-45.13, 9.25) * mm});
            skLineSegment(sketch, "E1013", {"start": v(-45.13, 9.25) * mm, "end": v(-45.15, 8.37) * mm});
            skLineSegment(sketch, "E1014", {"start": v(-45.15, 8.37) * mm, "end": v(-45.43, 7.6) * mm});
            skLineSegment(sketch, "E1015", {"start": v(-45.43, 7.6) * mm, "end": v(-45.6, 7.6) * mm});
            skLineSegment(sketch, "E1016", {"start": v(-45.6, 7.6) * mm, "end": v(-45.73, 7.87) * mm});
            skLineSegment(sketch, "E1017", {"start": v(-45.73, 7.87) * mm, "end": v(-45.75, 8.72) * mm});
            skLineSegment(sketch, "E1018", {"start": v(-45.75, 8.72) * mm, "end": v(-45.45, 9.24) * mm});
            skLineSegment(sketch, "E1019", {"start": v(-45.45, 9.24) * mm, "end": v(-45.44, 9.75) * mm});
            skLineSegment(sketch, "E1020", {"start": v(-45.44, 9.75) * mm, "end": v(-45.64, 9.72) * mm});
            skLineSegment(sketch, "E1021", {"start": v(-45.64, 9.72) * mm, "end": v(-46.01, 10.38) * mm});
            skLineSegment(sketch, "E1022", {"start": v(-46.01, 10.38) * mm, "end": v(-46.1, 10.27) * mm});
            skLineSegment(sketch, "E1023", {"start": v(-46.1, 10.27) * mm, "end": v(-46.68, 10.28) * mm});
            skLineSegment(sketch, "E1024", {"start": v(-46.68, 10.28) * mm, "end": v(-46.88, 10.65) * mm});
            skLineSegment(sketch, "E1025", {"start": v(-46.88, 10.65) * mm, "end": v(-46.92, 11.02) * mm});
            skLineSegment(sketch, "E1026", {"start": v(-46.92, 11.02) * mm, "end": v(-46.68, 11.16) * mm});
            skLineSegment(sketch, "E1027", {"start": v(-46.68, 11.16) * mm, "end": v(-46.9, 11.44) * mm});
            skLineSegment(sketch, "E1028", {"start": v(-46.9, 11.44) * mm, "end": v(-47.03, 11.2) * mm});
            skLineSegment(sketch, "E1029", {"start": v(-47.03, 11.2) * mm, "end": v(-47.1, 11.54) * mm});
            skLineSegment(sketch, "E1030", {"start": v(-47.1, 11.54) * mm, "end": v(-46.84, 11.74) * mm});
            skLineSegment(sketch, "E1031", {"start": v(-46.84, 11.74) * mm, "end": v(-46.88, 12.28) * mm});
            skLineSegment(sketch, "E1032", {"start": v(-46.88, 12.28) * mm, "end": v(-47.12, 12.27) * mm});
            skLineSegment(sketch, "E1033", {"start": v(-47.12, 12.27) * mm, "end": v(-47.07, 12.66) * mm});
            skLineSegment(sketch, "E1034", {"start": v(-47.07, 12.66) * mm, "end": v(-46.77, 12.98) * mm});
            skLineSegment(sketch, "E1035", {"start": v(-46.77, 12.98) * mm, "end": v(-46.9, 13.15) * mm});
            skLineSegment(sketch, "E1036", {"start": v(-46.9, 13.15) * mm, "end": v(-47.28, 12.81) * mm});
            skLineSegment(sketch, "E1037", {"start": v(-47.28, 12.81) * mm, "end": v(-47.54, 12.3) * mm});
            skLineSegment(sketch, "E1038", {"start": v(-47.54, 12.3) * mm, "end": v(-47.31, 11.96) * mm});
            skLineSegment(sketch, "E1039", {"start": v(-47.31, 11.96) * mm, "end": v(-47.5, 11.4) * mm});
            skLineSegment(sketch, "E1040", {"start": v(-47.5, 11.4) * mm, "end": v(-47.24, 10.74) * mm});
            skLineSegment(sketch, "E1041", {"start": v(-47.24, 10.74) * mm, "end": v(-47.02, 10.55) * mm});
            skLineSegment(sketch, "E1042", {"start": v(-47.02, 10.55) * mm, "end": v(-47.05, 10.37) * mm});
            skLineSegment(sketch, "E1043", {"start": v(-47.05, 10.37) * mm, "end": v(-46.9, 9.92) * mm});
            skLineSegment(sketch, "E1044", {"start": v(-46.9, 9.92) * mm, "end": v(-47.5, 9.98) * mm});
            skLineSegment(sketch, "E1045", {"start": v(-47.5, 9.98) * mm, "end": v(-47.97, 10) * mm});
            skLineSegment(sketch, "E1046", {"start": v(-47.97, 10) * mm, "end": v(-48.57, 10.12) * mm});
            skLineSegment(sketch, "E1047", {"start": v(-48.57, 10.12) * mm, "end": v(-48.65, 10.55) * mm});
            skLineSegment(sketch, "E1048", {"start": v(-48.65, 10.55) * mm, "end": v(-48.44, 10.81) * mm});
            skLineSegment(sketch, "E1049", {"start": v(-48.44, 10.81) * mm, "end": v(-48.42, 11.16) * mm});
            skLineSegment(sketch, "E1050", {"start": v(-48.42, 11.16) * mm, "end": v(-48.75, 11.58) * mm});
            skLineSegment(sketch, "E1051", {"start": v(-48.75, 11.58) * mm, "end": v(-49.42, 11.75) * mm});
            skLineSegment(sketch, "E1052", {"start": v(-49.42, 11.75) * mm, "end": v(-49.4, 12.07) * mm});
            skLineSegment(sketch, "E1053", {"start": v(-49.4, 12.07) * mm, "end": v(-49.9, 12.33) * mm});
            skLineSegment(sketch, "E1054", {"start": v(-47.97, 10) * mm, "end": v(-47.79, 9.81) * mm});
            skLineSegment(sketch, "E1055", {"start": v(-47.79, 9.81) * mm, "end": v(-47.15, 9.76) * mm});
            skLineSegment(sketch, "E1056", {"start": v(-47.15, 9.76) * mm, "end": v(-46.95, 9.5) * mm});
            skLineSegment(sketch, "E1057", {"start": v(-46.95, 9.5) * mm, "end": v(-46.6, 9.5) * mm});
            skLineSegment(sketch, "E1058", {"start": v(-46.6, 9.5) * mm, "end": v(-46.45, 9.33) * mm});
            skLineSegment(sketch, "E1059", {"start": v(-46.45, 9.33) * mm, "end": v(-46.48, 8.81) * mm});
            skLineSegment(sketch, "E1060", {"start": v(-46.48, 8.81) * mm, "end": v(-46.38, 8.75) * mm});
            skLineSegment(sketch, "E1061", {"start": v(-46.38, 8.75) * mm, "end": v(-46.38, 8.47) * mm});
            skLineSegment(sketch, "E1062", {"start": v(-46.38, 8.47) * mm, "end": v(-46.18, 8.21) * mm});
            skLineSegment(sketch, "E1063", {"start": v(-46.18, 8.21) * mm, "end": v(-46.2, 8.03) * mm});
            skLineSegment(sketch, "E1064", {"start": v(-46.2, 8.03) * mm, "end": v(-46.6, 8.16) * mm});
            skLineSegment(sketch, "E1065", {"start": v(-46.6, 8.16) * mm, "end": v(-46.6, 8.06) * mm});
            skLineSegment(sketch, "E1066", {"start": v(-46.6, 8.06) * mm, "end": v(-46.39, 7.9) * mm});
            skLineSegment(sketch, "E1067", {"start": v(-46.39, 7.9) * mm, "end": v(-46.39, 7.78) * mm});
            skLineSegment(sketch, "E1068", {"start": v(-46.39, 7.78) * mm, "end": v(-46.08, 7.5) * mm});
            skLineSegment(sketch, "E1069", {"start": v(-46.08, 7.5) * mm, "end": v(-46.02, 7.15) * mm});
            skLineSegment(sketch, "E1070", {"start": v(-46.02, 7.15) * mm, "end": v(-46.31, 7.05) * mm});
            skLineSegment(sketch, "E1071", {"start": v(-46.31, 7.05) * mm, "end": v(-46.31, 6.93) * mm});
            skLineSegment(sketch, "E1072", {"start": v(-46.31, 6.93) * mm, "end": v(-45.5, 7.1) * mm});
            skLineSegment(sketch, "E1073", {"start": v(-45.5, 7.1) * mm, "end": v(-45.14, 6.29) * mm});
            skLineSegment(sketch, "E1074", {"start": v(-45.14, 6.29) * mm, "end": v(-44.09, 4.58) * mm});
            skLineSegment(sketch, "E1075", {"start": v(-44.09, 4.58) * mm, "end": v(-44.49, 4.58) * mm});
            skLineSegment(sketch, "E1076", {"start": v(-58.46, 0.03) * mm, "end": v(-56.78, 0.8) * mm});
            skLineSegment(sketch, "E1077", {"start": v(-56.78, 0.8) * mm, "end": v(-54.18, 0.96) * mm});
            skLineSegment(sketch, "E1078", {"start": v(-54.18, 0.96) * mm, "end": v(-53.89, 0.64) * mm});
            skLineSegment(sketch, "E1079", {"start": v(-53.89, 0.64) * mm, "end": v(-53.8, 0.37) * mm});
            skLineSegment(sketch, "E1080", {"start": v(-53.8, 0.37) * mm, "end": v(-51.67, 0.56) * mm});
            skLineSegment(sketch, "E1081", {"start": v(-51.67, 0.56) * mm, "end": v(-49.1, -1.2) * mm});
            skLineSegment(sketch, "E1082", {"start": v(-49.1, -1.2) * mm, "end": v(-48.53, -1.05) * mm});
            skLineSegment(sketch, "E1083", {"start": v(-48.53, -1.05) * mm, "end": v(-47.81, -1) * mm});
            skLineSegment(sketch, "E1084", {"start": v(-47.81, -1) * mm, "end": v(-47.62, 0.05) * mm});
            skLineSegment(sketch, "E1085", {"start": v(-47.62, 0.05) * mm, "end": v(-46.45, 1.18) * mm});
            skLineSegment(sketch, "E1086", {"start": v(-46.45, 1.18) * mm, "end": v(-45.62, 1.52) * mm});
            skLineSegment(sketch, "E1087", {"start": v(-45.62, 1.52) * mm, "end": v(-45.32, 1.44) * mm});
            skLineSegment(sketch, "E1088", {"start": v(-45.32, 1.44) * mm, "end": v(-44.81, 2.27) * mm});
            skLineSegment(sketch, "E1089", {"start": v(-44.81, 2.27) * mm, "end": v(-45.16, 2.06) * mm});
            skLineSegment(sketch, "E1090", {"start": v(-45.16, 2.06) * mm, "end": v(-45.3, 2.25) * mm});
            skLineSegment(sketch, "E1091", {"start": v(-45.3, 2.25) * mm, "end": v(-45.75, 2.22) * mm});
            skLineSegment(sketch, "E1092", {"start": v(-45.75, 2.22) * mm, "end": v(-45.48, 2.94) * mm});
            skLineSegment(sketch, "E1093", {"start": v(-45.48, 2.94) * mm, "end": v(-45.78, 3.05) * mm});
            skLineSegment(sketch, "E1094", {"start": v(-45.78, 3.05) * mm, "end": v(-45.91, 3.34) * mm});
            skLineSegment(sketch, "E1095", {"start": v(-45.91, 3.34) * mm, "end": v(-45.35, 3.08) * mm});
            skLineSegment(sketch, "E1096", {"start": v(-45.35, 3.08) * mm, "end": v(-44.81, 3.24) * mm});
            skLineSegment(sketch, "E1097", {"start": v(-44.81, 3.24) * mm, "end": v(-44.6, 3.9) * mm});
            skLineSegment(sketch, "E1098", {"start": v(-44.6, 3.9) * mm, "end": v(-44.33, 4.04) * mm});
            skLineSegment(sketch, "E1099", {"start": v(-44.33, 4.04) * mm, "end": v(-44.49, 4.58) * mm});
            skLineSegment(sketch, "E1100", {"start": v(-58.46, 0.03) * mm, "end": v(-58.35, -0.21) * mm});
            skLineSegment(sketch, "E1101", {"start": v(-58.35, -0.21) * mm, "end": v(-58.67, -0.4) * mm});
            skLineSegment(sketch, "E1102", {"start": v(-58.67, -0.4) * mm, "end": v(-58.76, -0.8) * mm});
            skLineSegment(sketch, "E1103", {"start": v(-58.76, -0.8) * mm, "end": v(-58.08, -1.2) * mm});
            skLineSegment(sketch, "E1104", {"start": v(-58.08, -1.2) * mm, "end": v(-57.78, -1.14) * mm});
            skLineSegment(sketch, "E1105", {"start": v(-57.78, -1.14) * mm, "end": v(-57.01, -2.35) * mm});
            skLineSegment(sketch, "E1106", {"start": v(-57.01, -2.35) * mm, "end": v(-56.24, -2.8) * mm});
            skLineSegment(sketch, "E1107", {"start": v(-56.24, -2.8) * mm, "end": v(-56.1, -3.08) * mm});
            skLineSegment(sketch, "E1108", {"start": v(-56.1, -3.08) * mm, "end": v(-55.51, -3.4) * mm});
            skLineSegment(sketch, "E1109", {"start": v(-55.51, -3.4) * mm, "end": v(-55.04, -4) * mm});
            skLineSegment(sketch, "E1110", {"start": v(-55.04, -4) * mm, "end": v(-54.59, -4.22) * mm});
            skLineSegment(sketch, "E1111", {"start": v(-54.59, -4.22) * mm, "end": v(-54.12, -5.42) * mm});
            skLineSegment(sketch, "E1112", {"start": v(-54.12, -5.42) * mm, "end": v(-53.9, -5.42) * mm});
            skLineSegment(sketch, "E1113", {"start": v(-53.9, -5.42) * mm, "end": v(-53.53, -5.86) * mm});
            skLineSegment(sketch, "E1114", {"start": v(-53.53, -5.86) * mm, "end": v(-53.42, -6.31) * mm});
            skLineSegment(sketch, "E1115", {"start": v(-53.42, -6.31) * mm, "end": v(-52.82, -6.57) * mm});
            skLineSegment(sketch, "E1116", {"start": v(-52.82, -6.57) * mm, "end": v(-52.88, -6.35) * mm});
            skLineSegment(sketch, "E1117", {"start": v(-52.88, -6.35) * mm, "end": v(-52.1, -5.67) * mm});
            skLineSegment(sketch, "E1118", {"start": v(-52.1, -5.67) * mm, "end": v(-52.27, -5.3) * mm});
            skLineSegment(sketch, "E1119", {"start": v(-52.27, -5.3) * mm, "end": v(-51.86, -5.3) * mm});
            skLineSegment(sketch, "E1120", {"start": v(-51.86, -5.3) * mm, "end": v(-50.53, -3.76) * mm});
            skLineSegment(sketch, "E1121", {"start": v(-50.53, -3.76) * mm, "end": v(-50.33, -3.68) * mm});
            skLineSegment(sketch, "E1122", {"start": v(-50.33, -3.68) * mm, "end": v(-49.91, -3.2) * mm});
            skLineSegment(sketch, "E1123", {"start": v(-49.91, -3.2) * mm, "end": v(-49.88, -2.53) * mm});
            skLineSegment(sketch, "E1124", {"start": v(-49.88, -2.53) * mm, "end": v(-49.38, -1.6) * mm});
            skLineSegment(sketch, "E1125", {"start": v(-49.38, -1.6) * mm, "end": v(-49.1, -1.2) * mm});
            skLineSegment(sketch, "E1126", {"start": v(-52.82, -6.57) * mm, "end": v(-53.16, -7.37) * mm});
            skLineSegment(sketch, "E1127", {"start": v(-53.16, -7.37) * mm, "end": v(-53.14, -7.55) * mm});
            skLineSegment(sketch, "E1128", {"start": v(-53.14, -7.55) * mm, "end": v(-53.29, -8.05) * mm});
            skLineSegment(sketch, "E1129", {"start": v(-53.29, -8.05) * mm, "end": v(-53.62, -9.07) * mm});
            skLineSegment(sketch, "E1130", {"start": v(-53.62, -9.07) * mm, "end": v(-53.56, -9.89) * mm});
            skLineSegment(sketch, "E1131", {"start": v(-53.56, -9.89) * mm, "end": v(-54.64, -9.8) * mm});
            skLineSegment(sketch, "E1132", {"start": v(-54.64, -9.8) * mm, "end": v(-54.8, -10) * mm});
            skLineSegment(sketch, "E1133", {"start": v(-54.8, -10) * mm, "end": v(-54.73, -10.39) * mm});
            skLineSegment(sketch, "E1134", {"start": v(-54.73, -10.39) * mm, "end": v(-54.68, -10.89) * mm});
            skLineSegment(sketch, "E1135", {"start": v(-54.68, -10.89) * mm, "end": v(-55, -10.87) * mm});
            skLineSegment(sketch, "E1136", {"start": v(-55, -10.87) * mm, "end": v(-55.04, -10.5) * mm});
            skLineSegment(sketch, "E1137", {"start": v(-55.8, -14.03) * mm, "end": v(-55.24, -14.82) * mm});
            skLineSegment(sketch, "E1138", {"start": v(-55.24, -14.82) * mm, "end": v(-55.27, -16) * mm});
            skLineSegment(sketch, "E1139", {"start": v(-55.27, -16) * mm, "end": v(-55.5, -16.31) * mm});
            skLineSegment(sketch, "E1140", {"start": v(-55.5, -16.31) * mm, "end": v(-55.07, -17.58) * mm});
            skLineSegment(sketch, "E1141", {"start": v(-55.07, -17.58) * mm, "end": v(-54.87, -17.24) * mm});
            skLineSegment(sketch, "E1142", {"start": v(-54.87, -17.24) * mm, "end": v(-55.21, -16.96) * mm});
            skLineSegment(sketch, "E1143", {"start": v(-55.21, -16.96) * mm, "end": v(-54.42, -16.99) * mm});
            skLineSegment(sketch, "E1144", {"start": v(-54.42, -16.99) * mm, "end": v(-55.04, -17.95) * mm});
            skLineSegment(sketch, "E1145", {"start": v(-55.04, -17.95) * mm, "end": v(-54.4, -18.77) * mm});
            skLineSegment(sketch, "E1146", {"start": v(-54.4, -18.77) * mm, "end": v(-53.94, -19.39) * mm});
            skLineSegment(sketch, "E1147", {"start": v(-53.94, -19.39) * mm, "end": v(-53.58, -20.32) * mm});
            skLineSegment(sketch, "E1148", {"start": v(-53.58, -20.32) * mm, "end": v(-53.35, -20.46) * mm});
            skLineSegment(sketch, "E1149", {"start": v(-53.35, -20.46) * mm, "end": v(-53.12, -20.26) * mm});
            skLineSegment(sketch, "E1150", {"start": v(-53.12, -20.26) * mm, "end": v(-52.73, -20.57) * mm});
            skLineSegment(sketch, "E1151", {"start": v(-52.73, -20.57) * mm, "end": v(-52.64, -20.94) * mm});
            skLineSegment(sketch, "E1152", {"start": v(-52.64, -20.94) * mm, "end": v(-52.3, -21.48) * mm});
            skLineSegment(sketch, "E1153", {"start": v(-52.3, -21.48) * mm, "end": v(-52.1, -21.45) * mm});
            skLineSegment(sketch, "E1154", {"start": v(-52.1, -21.45) * mm, "end": v(-51.74, -21.5) * mm});
            skLineSegment(sketch, "E1155", {"start": v(-51.74, -21.5) * mm, "end": v(-51.32, -21.84) * mm});
            skLineSegment(sketch, "E1156", {"start": v(-51.32, -21.84) * mm, "end": v(-50.98, -22.3) * mm});
            skLineSegment(sketch, "E1157", {"start": v(-50.98, -22.3) * mm, "end": v(-50.81, -23.11) * mm});
            skLineSegment(sketch, "E1158", {"start": v(-50.81, -23.11) * mm, "end": v(-50.61, -23.28) * mm});
            skLineSegment(sketch, "E1159", {"start": v(-50.61, -23.28) * mm, "end": v(-50.3, -23.17) * mm});
            skLineSegment(sketch, "E1160", {"start": v(-50.3, -23.17) * mm, "end": v(-50.13, -22.83) * mm});
            skLineSegment(sketch, "E1161", {"start": v(-50.13, -22.83) * mm, "end": v(-49.9, -22.89) * mm});
            skLineSegment(sketch, "E1162", {"start": v(-49.9, -22.89) * mm, "end": v(-49.54, -22.83) * mm});
            skLineSegment(sketch, "E1163", {"start": v(-49.54, -22.83) * mm, "end": v(-49.06, -22.5) * mm});
            skLineSegment(sketch, "E1164", {"start": v(-49.06, -22.5) * mm, "end": v(-49.15, -22.07) * mm});
            skLineSegment(sketch, "E1165", {"start": v(-49.15, -22.07) * mm, "end": v(-49.15, -21.82) * mm});
            skLineSegment(sketch, "E1166", {"start": v(-49.15, -21.82) * mm, "end": v(-49.23, -21.45) * mm});
            skLineSegment(sketch, "E1167", {"start": v(-49.23, -21.45) * mm, "end": v(-48.8, -21.14) * mm});
            skLineSegment(sketch, "E1168", {"start": v(-48.8, -21.14) * mm, "end": v(-48.8, -20.69) * mm});
            skLineSegment(sketch, "E1169", {"start": v(-48.8, -20.69) * mm, "end": v(-48.95, -18.74) * mm});
            skLineSegment(sketch, "E1170", {"start": v(-48.95, -18.74) * mm, "end": v(-50.16, -16.48) * mm});
            skLineSegment(sketch, "E1171", {"start": v(-50.16, -16.48) * mm, "end": v(-50.7, -16.11) * mm});
            skLineSegment(sketch, "E1172", {"start": v(-50.7, -16.11) * mm, "end": v(-50.92, -15.32) * mm});
            skLineSegment(sketch, "E1173", {"start": v(-50.92, -15.32) * mm, "end": v(-50.75, -15.04) * mm});
            skLineSegment(sketch, "E1174", {"start": v(-50.75, -15.04) * mm, "end": v(-50.95, -14.56) * mm});
            skLineSegment(sketch, "E1175", {"start": v(-50.95, -14.56) * mm, "end": v(-51.69, -13.86) * mm});
            skLineSegment(sketch, "E1176", {"start": v(-51.69, -13.86) * mm, "end": v(-52.59, -12.47) * mm});
            skLineSegment(sketch, "E1177", {"start": v(-52.59, -12.47) * mm, "end": v(-53.3, -10.84) * mm});
            skLineSegment(sketch, "E1178", {"start": v(-53.3, -10.84) * mm, "end": v(-53.56, -9.89) * mm});
            skLineSegment(sketch, "E1179", {"start": v(-119.45, -10.84) * mm, "end": v(-120.42, -10.35) * mm});
            skLineSegment(sketch, "E1180", {"start": v(-120.42, -10.35) * mm, "end": v(-120.77, -10.52) * mm});
            skLineSegment(sketch, "E1181", {"start": v(-120.77, -10.52) * mm, "end": v(-121.47, -10.21) * mm});
            skLineSegment(sketch, "E1182", {"start": v(-121.47, -10.21) * mm, "end": v(-121.56, -10.52) * mm});
            skLineSegment(sketch, "E1183", {"start": v(-121.56, -10.52) * mm, "end": v(-122.26, -9.86) * mm});
            skLineSegment(sketch, "E1184", {"start": v(-122.26, -9.86) * mm, "end": v(-123.1, -9.82) * mm});
            skLineSegment(sketch, "E1185", {"start": v(-123.1, -9.82) * mm, "end": v(-123.34, -9.7) * mm});
            skLineSegment(sketch, "E1186", {"start": v(-123.34, -9.7) * mm, "end": v(-123.35, -9.2) * mm});
            skLineSegment(sketch, "E1187", {"start": v(-123.35, -9.2) * mm, "end": v(-123.76, -9.16) * mm});
            skLineSegment(sketch, "E1188", {"start": v(-123.76, -9.16) * mm, "end": v(-123.9, -9.42) * mm});
            skLineSegment(sketch, "E1189", {"start": v(-123.9, -9.42) * mm, "end": v(-123.96, -9.11) * mm});
            skLineSegment(sketch, "E1190", {"start": v(-123.96, -9.11) * mm, "end": v(-124.68, -8.61) * mm});
            skLineSegment(sketch, "E1191", {"start": v(-124.68, -8.61) * mm, "end": v(-125, -8.95) * mm});
            skLineSegment(sketch, "E1192", {"start": v(-125, -8.95) * mm, "end": v(-125.47, -9) * mm});
            skLineSegment(sketch, "E1193", {"start": v(-125.47, -9) * mm, "end": v(-125.67, -8.89) * mm});
            skLineSegment(sketch, "E1194", {"start": v(-125.67, -8.89) * mm, "end": v(-126.44, -9.24) * mm});
            skLineSegment(sketch, "E1195", {"start": v(-126.44, -9.24) * mm, "end": v(-126.7, -9.04) * mm});
            skLineSegment(sketch, "E1196", {"start": v(-126.7, -9.04) * mm, "end": v(-127, -9.37) * mm});
            skLineSegment(sketch, "E1197", {"start": v(-127, -9.37) * mm, "end": v(-127.12, -9.7) * mm});
            skLineSegment(sketch, "E1198", {"start": v(-127.12, -9.7) * mm, "end": v(-127.56, -10.07) * mm});
            skLineSegment(sketch, "E1199", {"start": v(-127.56, -10.07) * mm, "end": v(-128.01, -10.07) * mm});
            skLineSegment(sketch, "E1200", {"start": v(-128.01, -10.07) * mm, "end": v(-128.1, -10.06) * mm});
            skLineSegment(sketch, "E1201", {"start": v(-128.1, -10.06) * mm, "end": v(-128.55, -9.97) * mm});
            skLineSegment(sketch, "E1202", {"start": v(-128.55, -9.97) * mm, "end": v(-128.88, -10.23) * mm});
            skLineSegment(sketch, "E1203", {"start": v(-128.88, -10.23) * mm, "end": v(-128.29, -11.25) * mm});
            skLineSegment(sketch, "E1204", {"start": v(-128.29, -11.25) * mm, "end": v(-128.29, -11.95) * mm});
            skLineSegment(sketch, "E1205", {"start": v(-128.29, -11.95) * mm, "end": v(-127.79, -12.18) * mm});
            skLineSegment(sketch, "E1206", {"start": v(-127.79, -12.18) * mm, "end": v(-127.97, -12.28) * mm});
            skLineSegment(sketch, "E1207", {"start": v(-127.97, -12.28) * mm, "end": v(-127.62, -13.12) * mm});
            skLineSegment(sketch, "E1208", {"start": v(-127.62, -13.12) * mm, "end": v(-127.8, -13.27) * mm});
            skLineSegment(sketch, "E1209", {"start": v(-127.8, -13.27) * mm, "end": v(-128.64, -12.9) * mm});
            skLineSegment(sketch, "E1210", {"start": v(-128.64, -12.9) * mm, "end": v(-128.44, -12.47) * mm});
            skLineSegment(sketch, "E1211", {"start": v(-128.44, -12.47) * mm, "end": v(-128.65, -12.3) * mm});
            skLineSegment(sketch, "E1212", {"start": v(-128.65, -12.3) * mm, "end": v(-129.26, -12.36) * mm});
            skLineSegment(sketch, "E1213", {"start": v(-129.26, -12.36) * mm, "end": v(-129.26, -12.56) * mm});
            skLineSegment(sketch, "E1214", {"start": v(-129.26, -12.56) * mm, "end": v(-129.39, -12.57) * mm});
            skLineSegment(sketch, "E1215", {"start": v(-129.39, -12.57) * mm, "end": v(-129.48, -12.48) * mm});
            skLineSegment(sketch, "E1216", {"start": v(-129.48, -12.48) * mm, "end": v(-130.4, -12.5) * mm});
            skLineSegment(sketch, "E1217", {"start": v(-130.4, -12.5) * mm, "end": v(-130.48, -12.68) * mm});
            skLineSegment(sketch, "E1218", {"start": v(-130.48, -12.68) * mm, "end": v(-130.12, -13.17) * mm});
            skLineSegment(sketch, "E1219", {"start": v(-130.12, -13.17) * mm, "end": v(-130.2, -13.85) * mm});
            skLineSegment(sketch, "E1220", {"start": v(-130.2, -13.85) * mm, "end": v(-129.78, -14.34) * mm});
            skLineSegment(sketch, "E1221", {"start": v(-129.78, -14.34) * mm, "end": v(-129.3, -14.31) * mm});
            skLineSegment(sketch, "E1222", {"start": v(-129.3, -14.31) * mm, "end": v(-128.72, -14.57) * mm});
            skLineSegment(sketch, "E1223", {"start": v(-128.72, -14.57) * mm, "end": v(-128.05, -14.42) * mm});
            skLineSegment(sketch, "E1224", {"start": v(-128.05, -14.42) * mm, "end": v(-127.92, -14.62) * mm});
            skLineSegment(sketch, "E1225", {"start": v(-127.92, -14.62) * mm, "end": v(-128.18, -15.58) * mm});
            skLineSegment(sketch, "E1226", {"start": v(-119.45, -10.84) * mm, "end": v(-119.45, -20.33) * mm});
            skLineSegment(sketch, "E1227", {"start": v(-119.45, -20.33) * mm, "end": v(-119.3, -20.6) * mm});
            skLineSegment(sketch, "E1228", {"start": v(-119.3, -20.6) * mm, "end": v(-119.04, -20.53) * mm});
            skLineSegment(sketch, "E1229", {"start": v(-119.04, -20.53) * mm, "end": v(-118.9, -20.53) * mm});
            skLineSegment(sketch, "E1230", {"start": v(-118.9, -20.53) * mm, "end": v(-118.7, -20.38) * mm});
            skLineSegment(sketch, "E1231", {"start": v(-118.7, -20.38) * mm, "end": v(-118.54, -20.44) * mm});
            skLineSegment(sketch, "E1232", {"start": v(-118.54, -20.44) * mm, "end": v(-118.52, -20.75) * mm});
            skLineSegment(sketch, "E1233", {"start": v(-118.52, -20.75) * mm, "end": v(-117.81, -21.4) * mm});
            skLineSegment(sketch, "E1234", {"start": v(-117.81, -21.4) * mm, "end": v(-117.65, -21.8) * mm});
            skLineSegment(sketch, "E1235", {"start": v(-117.65, -21.8) * mm, "end": v(-117.1, -21.52) * mm});
            skLineSegment(sketch, "E1236", {"start": v(-117.1, -21.52) * mm, "end": v(-117.09, -21.11) * mm});
            skLineSegment(sketch, "E1237", {"start": v(-117.09, -21.11) * mm, "end": v(-116.82, -20.97) * mm});
            skLineSegment(sketch, "E1238", {"start": v(-116.47, -21.07) * mm, "end": v(-116.32, -21.46) * mm});
            skLineSegment(sketch, "E1239", {"start": v(-116.32, -21.46) * mm, "end": v(-116.06, -21.46) * mm});
            skLineSegment(sketch, "E1240", {"start": v(-116.06, -21.46) * mm, "end": v(-116.02, -21.9) * mm});
            skLineSegment(sketch, "E1241", {"start": v(-116.82, -20.97) * mm, "end": v(-116.47, -21.07) * mm});
            skLineSegment(sketch, "E1242", {"start": v(-116.02, -21.9) * mm, "end": v(-115.6, -21.9) * mm});
            skLineSegment(sketch, "E1243", {"start": v(-115.6, -21.9) * mm, "end": v(-115.17, -22.75) * mm});
            skLineSegment(sketch, "E1244", {"start": v(-115.17, -22.75) * mm, "end": v(-114.66, -23.31) * mm});
            skLineSegment(sketch, "E1245", {"start": v(-114.66, -23.31) * mm, "end": v(-114.51, -23.8) * mm});
            skLineSegment(sketch, "E1246", {"start": v(-114.51, -23.8) * mm, "end": v(-113.34, -24.17) * mm});
            skLineSegment(sketch, "E1247", {"start": v(-113.34, -24.17) * mm, "end": v(-113.21, -24.91) * mm});
            skLineSegment(sketch, "E1248", {"start": v(-113.21, -24.91) * mm, "end": v(-113.48, -25.6) * mm});
            skLineSegment(sketch, "E1249", {"start": v(-113.48, -25.6) * mm, "end": v(-113.62, -25.51) * mm});
            skLineSegment(sketch, "E1250", {"start": v(-113.62, -25.51) * mm, "end": v(-113.73, -25.23) * mm});
            skLineSegment(sketch, "E1251", {"start": v(-113.73, -25.23) * mm, "end": v(-114.23, -24.92) * mm});
            skLineSegment(sketch, "E1252", {"start": v(-114.23, -24.92) * mm, "end": v(-114.37, -24.98) * mm});
            skLineSegment(sketch, "E1253", {"start": v(-114.37, -24.98) * mm, "end": v(-114.22, -25.2) * mm});
            skLineSegment(sketch, "E1254", {"start": v(-114.22, -25.2) * mm, "end": v(-114.22, -25.78) * mm});
            skLineSegment(sketch, "E1255", {"start": v(-114.22, -25.78) * mm, "end": v(-114.51, -25.54) * mm});
            skLineSegment(sketch, "E1256", {"start": v(-114.51, -25.54) * mm, "end": v(-114.8, -25.32) * mm});
            skLineSegment(sketch, "E1257", {"start": v(-114.8, -25.32) * mm, "end": v(-114.57, -25.75) * mm});
            skLineSegment(sketch, "E1258", {"start": v(-114.57, -25.75) * mm, "end": v(-114.67, -25.88) * mm});
            skLineSegment(sketch, "E1259", {"start": v(-114.67, -25.88) * mm, "end": v(-115.11, -25.12) * mm});
            skLineSegment(sketch, "E1260", {"start": v(-115.11, -25.12) * mm, "end": v(-115.22, -25.24) * mm});
            skLineSegment(sketch, "E1261", {"start": v(-115.14, -24.88) * mm, "end": v(-115.3, -24.75) * mm});
            skLineSegment(sketch, "E1262", {"start": v(-115.3, -24.75) * mm, "end": v(-115.3, -24.18) * mm});
            skLineSegment(sketch, "E1263", {"start": v(-115.3, -24.18) * mm, "end": v(-115.49, -24.55) * mm});
            skLineSegment(sketch, "E1264", {"start": v(-115.49, -24.55) * mm, "end": v(-115.67, -24.68) * mm});
            skLineSegment(sketch, "E1265", {"start": v(-115.67, -24.68) * mm, "end": v(-115.78, -23.8) * mm});
            skLineSegment(sketch, "E1266", {"start": v(-115.78, -23.8) * mm, "end": v(-115.91, -23.73) * mm});
            skLineSegment(sketch, "E1267", {"start": v(-115.91, -23.73) * mm, "end": v(-115.91, -24.4) * mm});
            skLineSegment(sketch, "E1268", {"start": v(-115.91, -24.4) * mm, "end": v(-116.4, -23.7) * mm});
            skLineSegment(sketch, "E1269", {"start": v(-116.4, -23.7) * mm, "end": v(-116.71, -23.63) * mm});
            skLineSegment(sketch, "E1270", {"start": v(-116.71, -23.63) * mm, "end": v(-116.72, -23.23) * mm});
            skLineSegment(sketch, "E1271", {"start": v(-116.72, -23.23) * mm, "end": v(-116.89, -22.9) * mm});
            skLineSegment(sketch, "E1272", {"start": v(-116.89, -22.9) * mm, "end": v(-117.14, -22.73) * mm});
            skLineSegment(sketch, "E1273", {"start": v(-117.14, -22.73) * mm, "end": v(-117.14, -22.52) * mm});
            skLineSegment(sketch, "E1274", {"start": v(-117.14, -22.52) * mm, "end": v(-116.82, -22.36) * mm});
            skLineSegment(sketch, "E1275", {"start": v(-116.82, -22.36) * mm, "end": v(-116.93, -22.28) * mm});
            skLineSegment(sketch, "E1276", {"start": v(-116.93, -22.28) * mm, "end": v(-117.16, -22.42) * mm});
            skLineSegment(sketch, "E1277", {"start": v(-117.16, -22.42) * mm, "end": v(-117.64, -22.06) * mm});
            skLineSegment(sketch, "E1278", {"start": v(-117.64, -22.06) * mm, "end": v(-117.77, -21.89) * mm});
            skLineSegment(sketch, "E1279", {"start": v(-117.77, -21.89) * mm, "end": v(-118.85, -21.27) * mm});
            skLineSegment(sketch, "E1280", {"start": v(-118.85, -21.27) * mm, "end": v(-118.67, -20.95) * mm});
            skLineSegment(sketch, "E1281", {"start": v(-118.67, -20.95) * mm, "end": v(-118.66, -20.63) * mm});
            skLineSegment(sketch, "E1282", {"start": v(-118.66, -20.63) * mm, "end": v(-119.13, -20.97) * mm});
            skLineSegment(sketch, "E1283", {"start": v(-119.13, -20.97) * mm, "end": v(-120.21, -20.6) * mm});
            skLineSegment(sketch, "E1284", {"start": v(-120.21, -20.6) * mm, "end": v(-120.83, -20.57) * mm});
            skLineSegment(sketch, "E1285", {"start": v(-120.83, -20.57) * mm, "end": v(-120.9, -20.65) * mm});
            skLineSegment(sketch, "E1286", {"start": v(-120.9, -20.65) * mm, "end": v(-121.57, -20.22) * mm});
            skLineSegment(sketch, "E1287", {"start": v(-121.57, -20.22) * mm, "end": v(-121.78, -20.2) * mm});
            skLineSegment(sketch, "E1288", {"start": v(-121.78, -20.2) * mm, "end": v(-122.13, -19.56) * mm});
            skLineSegment(sketch, "E1289", {"start": v(-122.13, -19.56) * mm, "end": v(-122.46, -19.55) * mm});
            skLineSegment(sketch, "E1290", {"start": v(-122.46, -19.55) * mm, "end": v(-122.95, -19.74) * mm});
            skLineSegment(sketch, "E1291", {"start": v(-122.95, -19.74) * mm, "end": v(-122.94, -20.15) * mm});
            skLineSegment(sketch, "E1292", {"start": v(-122.94, -20.15) * mm, "end": v(-122.77, -20.17) * mm});
            skLineSegment(sketch, "E1293", {"start": v(-122.77, -20.17) * mm, "end": v(-122.82, -20.41) * mm});
            skLineSegment(sketch, "E1294", {"start": v(-122.82, -20.41) * mm, "end": v(-123, -20.6) * mm});
            skLineSegment(sketch, "E1295", {"start": v(-123, -20.6) * mm, "end": v(-123.16, -20.45) * mm});
            skLineSegment(sketch, "E1296", {"start": v(-123.16, -20.45) * mm, "end": v(-123.3, -20.58) * mm});
            skLineSegment(sketch, "E1297", {"start": v(-123.3, -20.58) * mm, "end": v(-123.57, -20.37) * mm});
            skLineSegment(sketch, "E1298", {"start": v(-123.57, -20.37) * mm, "end": v(-123.94, -20.61) * mm});
            skLineSegment(sketch, "E1299", {"start": v(-123.94, -20.61) * mm, "end": v(-124.47, -21.07) * mm});
            skLineSegment(sketch, "E1300", {"start": v(-124.47, -21.07) * mm, "end": v(-125.08, -21.07) * mm});
            skLineSegment(sketch, "E1301", {"start": v(-125.08, -21.07) * mm, "end": v(-125.1, -20.85) * mm});
            skLineSegment(sketch, "E1302", {"start": v(-125.1, -20.85) * mm, "end": v(-124.7, -20.8) * mm});
            skLineSegment(sketch, "E1303", {"start": v(-124.7, -20.8) * mm, "end": v(-124.68, -20.61) * mm});
            skLineSegment(sketch, "E1304", {"start": v(-124.68, -20.61) * mm, "end": v(-124.99, -20.54) * mm});
            skLineSegment(sketch, "E1305", {"start": v(-124.99, -20.54) * mm, "end": v(-124.44, -19.5) * mm});
            skLineSegment(sketch, "E1306", {"start": v(-124.44, -19.5) * mm, "end": v(-124.1, -19.32) * mm});
            skLineSegment(sketch, "E1307", {"start": v(-124.1, -19.32) * mm, "end": v(-123.96, -19.46) * mm});
            skLineSegment(sketch, "E1308", {"start": v(-123.96, -19.46) * mm, "end": v(-123.65, -19.48) * mm});
            skLineSegment(sketch, "E1309", {"start": v(-123.65, -19.48) * mm, "end": v(-123.8, -19.16) * mm});
            skLineSegment(sketch, "E1310", {"start": v(-123.8, -19.16) * mm, "end": v(-124.18, -19.08) * mm});
            skLineSegment(sketch, "E1311", {"start": v(-124.18, -19.08) * mm, "end": v(-124.8, -19.41) * mm});
            skLineSegment(sketch, "E1312", {"start": v(-124.8, -19.41) * mm, "end": v(-125.34, -20.35) * mm});
            skLineSegment(sketch, "E1313", {"start": v(-125.34, -20.35) * mm, "end": v(-125.86, -20.53) * mm});
            skLineSegment(sketch, "E1314", {"start": v(-125.86, -20.53) * mm, "end": v(-126.2, -20.83) * mm});
            skLineSegment(sketch, "E1315", {"start": v(-126.2, -20.83) * mm, "end": v(-126.2, -20.96) * mm});
            skLineSegment(sketch, "E1316", {"start": v(-126.2, -20.96) * mm, "end": v(-126, -21.1) * mm});
            skLineSegment(sketch, "E1317", {"start": v(-126, -21.1) * mm, "end": v(-125.87, -21.33) * mm});
            skLineSegment(sketch, "E1318", {"start": v(-125.87, -21.33) * mm, "end": v(-126.15, -21.64) * mm});
            skLineSegment(sketch, "E1319", {"start": v(-126.15, -21.64) * mm, "end": v(-127.99, -22.73) * mm});
            skLineSegment(sketch, "E1320", {"start": v(-127.99, -22.73) * mm, "end": v(-129.11, -23.1) * mm});
            skLineSegment(sketch, "E1321", {"start": v(-129.11, -23.1) * mm, "end": v(-128.96, -23.27) * mm});
            skLineSegment(sketch, "E1322", {"start": v(-128.96, -23.27) * mm, "end": v(-129.17, -23.54) * mm});
            skLineSegment(sketch, "E1323", {"start": v(-129.17, -23.54) * mm, "end": v(-129.46, -23.44) * mm});
            skLineSegment(sketch, "E1324", {"start": v(-129.46, -23.44) * mm, "end": v(-129.75, -23.43) * mm});
            skLineSegment(sketch, "E1325", {"start": v(-129.75, -23.43) * mm, "end": v(-129.86, -23.6) * mm});
            skLineSegment(sketch, "E1326", {"start": v(-129.86, -23.6) * mm, "end": v(-129.95, -23.46) * mm});
            skLineSegment(sketch, "E1327", {"start": v(-129.95, -23.46) * mm, "end": v(-130.63, -23.7) * mm});
            skLineSegment(sketch, "E1328", {"start": v(-130.63, -23.7) * mm, "end": v(-131.06, -23.53) * mm});
            skLineSegment(sketch, "E1329", {"start": v(-131.06, -23.53) * mm, "end": v(-131.34, -23.75) * mm});
            skLineSegment(sketch, "E1330", {"start": v(-131.34, -23.75) * mm, "end": v(-131.72, -23.74) * mm});
            skLineSegment(sketch, "E1331", {"start": v(-131.72, -23.74) * mm, "end": v(-132.1, -23.98) * mm});
            skLineSegment(sketch, "E1332", {"start": v(-132.1, -23.98) * mm, "end": v(-132.65, -23.86) * mm});
            skLineSegment(sketch, "E1333", {"start": v(-132.65, -23.86) * mm, "end": v(-133.01, -24) * mm});
            skLineSegment(sketch, "E1334", {"start": v(-133.01, -24) * mm, "end": v(-133.24, -23.88) * mm});
            skLineSegment(sketch, "E1335", {"start": v(-133.24, -23.88) * mm, "end": v(-133.2, -23.63) * mm});
            skLineSegment(sketch, "E1336", {"start": v(-133.2, -23.63) * mm, "end": v(-132.95, -23.5) * mm});
            skLineSegment(sketch, "E1337", {"start": v(-132.95, -23.5) * mm, "end": v(-132.24, -23.59) * mm});
            skLineSegment(sketch, "E1338", {"start": v(-132.24, -23.59) * mm, "end": v(-131.93, -23.48) * mm});
            skLineSegment(sketch, "E1339", {"start": v(-131.93, -23.48) * mm, "end": v(-131.78, -23.42) * mm});
            skLineSegment(sketch, "E1340", {"start": v(-131.78, -23.42) * mm, "end": v(-131.43, -23.11) * mm});
            skLineSegment(sketch, "E1341", {"start": v(-131.43, -23.11) * mm, "end": v(-131.2, -23.08) * mm});
            skLineSegment(sketch, "E1342", {"start": v(-131.2, -23.08) * mm, "end": v(-130.92, -22.98) * mm});
            skLineSegment(sketch, "E1343", {"start": v(-130.92, -22.98) * mm, "end": v(-130.7, -23) * mm});
            skLineSegment(sketch, "E1344", {"start": v(-130.7, -23) * mm, "end": v(-130.56, -23.16) * mm});
            skLineSegment(sketch, "E1345", {"start": v(-130.56, -23.16) * mm, "end": v(-130.33, -23.15) * mm});
            skLineSegment(sketch, "E1346", {"start": v(-130.33, -23.15) * mm, "end": v(-130.03, -22.8) * mm});
            skLineSegment(sketch, "E1347", {"start": v(-130.03, -22.8) * mm, "end": v(-129.24, -22.63) * mm});
            skLineSegment(sketch, "E1348", {"start": v(-129.24, -22.63) * mm, "end": v(-129.13, -22.67) * mm});
            skLineSegment(sketch, "E1349", {"start": v(-129.13, -22.67) * mm, "end": v(-128.98, -22.27) * mm});
            skLineSegment(sketch, "E1350", {"start": v(-128.98, -22.27) * mm, "end": v(-128.5, -22.1) * mm});
            skLineSegment(sketch, "E1351", {"start": v(-128.5, -22.1) * mm, "end": v(-128.08, -21.21) * mm});
            skLineSegment(sketch, "E1352", {"start": v(-128.08, -21.21) * mm, "end": v(-127.83, -21.04) * mm});
            skLineSegment(sketch, "E1353", {"start": v(-127.83, -21.04) * mm, "end": v(-127.78, -20.7) * mm});
            skLineSegment(sketch, "E1354", {"start": v(-127.78, -20.7) * mm, "end": v(-128.22, -20.92) * mm});
            skLineSegment(sketch, "E1355", {"start": v(-128.22, -20.92) * mm, "end": v(-128.44, -20.7) * mm});
            skLineSegment(sketch, "E1356", {"start": v(-128.44, -20.7) * mm, "end": v(-128.57, -20.68) * mm});
            skLineSegment(sketch, "E1357", {"start": v(-128.57, -20.68) * mm, "end": v(-128.76, -20.75) * mm});
            skLineSegment(sketch, "E1358", {"start": v(-128.76, -20.75) * mm, "end": v(-128.78, -21.05) * mm});
            skLineSegment(sketch, "E1359", {"start": v(-128.78, -21.05) * mm, "end": v(-128.88, -21.05) * mm});
            skLineSegment(sketch, "E1360", {"start": v(-128.88, -21.05) * mm, "end": v(-129, -20.39) * mm});
            skLineSegment(sketch, "E1361", {"start": v(-129, -20.39) * mm, "end": v(-129.16, -20.51) * mm});
            skLineSegment(sketch, "E1362", {"start": v(-129.16, -20.51) * mm, "end": v(-129.27, -20.52) * mm});
            skLineSegment(sketch, "E1363", {"start": v(-129.27, -20.52) * mm, "end": v(-129.3, -20.3) * mm});
            skLineSegment(sketch, "E1364", {"start": v(-129.3, -20.3) * mm, "end": v(-129.78, -20.33) * mm});
            skLineSegment(sketch, "E1365", {"start": v(-129.78, -20.33) * mm, "end": v(-130.06, -20.45) * mm});
            skLineSegment(sketch, "E1366", {"start": v(-130.06, -20.45) * mm, "end": v(-130.35, -20.4) * mm});
            skLineSegment(sketch, "E1367", {"start": v(-130.35, -20.4) * mm, "end": v(-130.13, -20.15) * mm});
            skLineSegment(sketch, "E1368", {"start": v(-130.13, -20.15) * mm, "end": v(-130.16, -19.72) * mm});
            skLineSegment(sketch, "E1369", {"start": v(-130.16, -19.72) * mm, "end": v(-129.82, -19.65) * mm});
            skLineSegment(sketch, "E1370", {"start": v(-129.82, -19.65) * mm, "end": v(-129.95, -19.48) * mm});
            skLineSegment(sketch, "E1371", {"start": v(-129.95, -19.48) * mm, "end": v(-129.9, -18.97) * mm});
            skLineSegment(sketch, "E1372", {"start": v(-129.9, -18.97) * mm, "end": v(-130.09, -18.8) * mm});
            skLineSegment(sketch, "E1373", {"start": v(-130.09, -18.8) * mm, "end": v(-130.2, -18.98) * mm});
            skLineSegment(sketch, "E1374", {"start": v(-130.2, -18.98) * mm, "end": v(-130.82, -18.96) * mm});
            skLineSegment(sketch, "E1375", {"start": v(-130.82, -18.96) * mm, "end": v(-130.98, -18.83) * mm});
            skLineSegment(sketch, "E1376", {"start": v(-130.98, -18.83) * mm, "end": v(-131.04, -18.46) * mm});
            skLineSegment(sketch, "E1377", {"start": v(-131.04, -18.46) * mm, "end": v(-131.23, -18.07) * mm});
            skLineSegment(sketch, "E1378", {"start": v(-131.23, -18.07) * mm, "end": v(-131.27, -17.86) * mm});
            skLineSegment(sketch, "E1379", {"start": v(-131.27, -17.86) * mm, "end": v(-131.03, -17.8) * mm});
            skLineSegment(sketch, "E1380", {"start": v(-131.03, -17.8) * mm, "end": v(-131.04, -17.6) * mm});
            skLineSegment(sketch, "E1381", {"start": v(-131.04, -17.6) * mm, "end": v(-130.88, -17.49) * mm});
            skLineSegment(sketch, "E1382", {"start": v(-130.88, -17.49) * mm, "end": v(-130.98, -17.43) * mm});
            skLineSegment(sketch, "E1383", {"start": v(-130.98, -17.43) * mm, "end": v(-131.1, -17.45) * mm});
            skLineSegment(sketch, "E1384", {"start": v(-131.1, -17.45) * mm, "end": v(-131.25, -17.17) * mm});
            skLineSegment(sketch, "E1385", {"start": v(-131.25, -17.17) * mm, "end": v(-131.17, -16.56) * mm});
            skLineSegment(sketch, "E1386", {"start": v(-131.17, -16.56) * mm, "end": v(-130.38, -16.06) * mm});
            skLineSegment(sketch, "E1387", {"start": v(-130.38, -16.06) * mm, "end": v(-130.16, -15.66) * mm});
            skLineSegment(sketch, "E1388", {"start": v(-130.16, -15.66) * mm, "end": v(-129.87, -15.5) * mm});
            skLineSegment(sketch, "E1389", {"start": v(-129.87, -15.5) * mm, "end": v(-129.61, -15.57) * mm});
            skLineSegment(sketch, "E1390", {"start": v(-129.61, -15.57) * mm, "end": v(-129.52, -15.91) * mm});
            skLineSegment(sketch, "E1391", {"start": v(-129.52, -15.91) * mm, "end": v(-129.21, -15.85) * mm});
            skLineSegment(sketch, "E1392", {"start": v(-129.21, -15.85) * mm, "end": v(-128.88, -15.64) * mm});
            skLineSegment(sketch, "E1393", {"start": v(-128.88, -15.64) * mm, "end": v(-128.6, -15.78) * mm});
            skLineSegment(sketch, "E1394", {"start": v(-128.6, -15.78) * mm, "end": v(-128.45, -15.78) * mm});
            skLineSegment(sketch, "E1395", {"start": v(-128.45, -15.78) * mm, "end": v(-128.18, -15.58) * mm});
            skLineSegment(sketch, "E1396", {"start": v(-110.63, -17.84) * mm, "end": v(-110.83, -18.15) * mm});
            skLineSegment(sketch, "E1397", {"start": v(-110.83, -18.15) * mm, "end": v(-111.16, -18.16) * mm});
            skLineSegment(sketch, "E1398", {"start": v(-111.16, -18.16) * mm, "end": v(-110.97, -17.79) * mm});
            skLineSegment(sketch, "E1399", {"start": v(-110.97, -17.79) * mm, "end": v(-110.72, -17.74) * mm});
            skLineSegment(sketch, "E1400", {"start": v(-110.72, -17.74) * mm, "end": v(-110.63, -17.84) * mm});
            skLineSegment(sketch, "E1401", {"start": v(-109.4, -18.04) * mm, "end": v(-110, -17.74) * mm});
            skLineSegment(sketch, "E1402", {"start": v(-110, -17.74) * mm, "end": v(-109.96, -17.32) * mm});
            skLineSegment(sketch, "E1403", {"start": v(-109.96, -17.32) * mm, "end": v(-109.46, -17.13) * mm});
            skLineSegment(sketch, "E1404", {"start": v(-109.46, -17.13) * mm, "end": v(-109.02, -17.2) * mm});
            skLineSegment(sketch, "E1405", {"start": v(-109.02, -17.2) * mm, "end": v(-108.98, -17.6) * mm});
            skLineSegment(sketch, "E1406", {"start": v(-108.98, -17.6) * mm, "end": v(-109.07, -18) * mm});
            skLineSegment(sketch, "E1407", {"start": v(-109.07, -18) * mm, "end": v(-109.4, -18.04) * mm});
            skLineSegment(sketch, "E1408", {"start": v(-105.16, -19.33) * mm, "end": v(-105.47, -19.18) * mm});
            skLineSegment(sketch, "E1409", {"start": v(-105.47, -19.18) * mm, "end": v(-105.9, -18.35) * mm});
            skLineSegment(sketch, "E1410", {"start": v(-105.9, -18.35) * mm, "end": v(-106.59, -18.66) * mm});
            skLineSegment(sketch, "E1411", {"start": v(-106.59, -18.66) * mm, "end": v(-106.65, -18.86) * mm});
            skLineSegment(sketch, "E1412", {"start": v(-106.65, -18.86) * mm, "end": v(-106.23, -19.49) * mm});
            skLineSegment(sketch, "E1413", {"start": v(-106.23, -19.49) * mm, "end": v(-105.8, -19.4) * mm});
            skLineSegment(sketch, "E1414", {"start": v(-105.8, -19.4) * mm, "end": v(-105.67, -19.54) * mm});
            skLineSegment(sketch, "E1415", {"start": v(-105.67, -19.54) * mm, "end": v(-105.25, -19.53) * mm});
            skLineSegment(sketch, "E1416", {"start": v(-105.25, -19.53) * mm, "end": v(-105.16, -19.33) * mm});
            skLineSegment(sketch, "E1417", {"start": v(-104.26, -19.64) * mm, "end": v(-104.41, -19.85) * mm});
            skLineSegment(sketch, "E1418", {"start": v(-104.41, -19.85) * mm, "end": v(-103.97, -20) * mm});
            skLineSegment(sketch, "E1419", {"start": v(-103.97, -20) * mm, "end": v(-103.32, -20.09) * mm});
            skLineSegment(sketch, "E1420", {"start": v(-103.32, -20.09) * mm, "end": v(-103.02, -19.91) * mm});
            skLineSegment(sketch, "E1421", {"start": v(-103.02, -19.91) * mm, "end": v(-103.02, -19.74) * mm});
            skLineSegment(sketch, "E1422", {"start": v(-103.02, -19.74) * mm, "end": v(-103.7, -19.73) * mm});
            skLineSegment(sketch, "E1423", {"start": v(-103.7, -19.73) * mm, "end": v(-103.77, -19.81) * mm});
            skLineSegment(sketch, "E1424", {"start": v(-103.77, -19.81) * mm, "end": v(-104, -19.68) * mm});
            skLineSegment(sketch, "E1425", {"start": v(-104, -19.68) * mm, "end": v(-104.26, -19.64) * mm});
            skLineSegment(sketch, "E1426", {"start": v(-103.36, -20.32) * mm, "end": v(-103.24, -20.47) * mm});
            skLineSegment(sketch, "E1427", {"start": v(-103.24, -20.47) * mm, "end": v(-103.23, -20.69) * mm});
            skLineSegment(sketch, "E1428", {"start": v(-103.23, -20.69) * mm, "end": v(-103.62, -20.87) * mm});
            skLineSegment(sketch, "E1429", {"start": v(-103.62, -20.87) * mm, "end": v(-103.83, -20.36) * mm});
            skLineSegment(sketch, "E1430", {"start": v(-103.83, -20.36) * mm, "end": v(-103.36, -20.32) * mm});
            skLineSegment(sketch, "E1431", {"start": v(-103.06, -20.3) * mm, "end": v(-102.77, -19.95) * mm});
            skLineSegment(sketch, "E1432", {"start": v(-102.77, -19.95) * mm, "end": v(-102.3, -20.22) * mm});
            skLineSegment(sketch, "E1433", {"start": v(-102.3, -20.22) * mm, "end": v(-101.88, -20.34) * mm});
            skLineSegment(sketch, "E1434", {"start": v(-101.88, -20.34) * mm, "end": v(-101.3, -20.65) * mm});
            skLineSegment(sketch, "E1435", {"start": v(-101.3, -20.65) * mm, "end": v(-101.31, -20.85) * mm});
            skLineSegment(sketch, "E1436", {"start": v(-101.31, -20.85) * mm, "end": v(-102.21, -21.2) * mm});
            skLineSegment(sketch, "E1437", {"start": v(-102.21, -21.2) * mm, "end": v(-102.46, -21.05) * mm});
            skLineSegment(sketch, "E1438", {"start": v(-102.46, -21.05) * mm, "end": v(-103.06, -20.3) * mm});
            skLineSegment(sketch, "E1439", {"start": v(-99.67, -24.28) * mm, "end": v(-99.57, -24.36) * mm});
            skLineSegment(sketch, "E1440", {"start": v(-99.57, -24.36) * mm, "end": v(-99.06, -24.25) * mm});
            skLineSegment(sketch, "E1441", {"start": v(-99.06, -24.25) * mm, "end": v(-98.57, -23.8) * mm});
            skLineSegment(sketch, "E1442", {"start": v(-98.57, -23.8) * mm, "end": v(-99.09, -23.44) * mm});
            skLineSegment(sketch, "E1443", {"start": v(-99.09, -23.44) * mm, "end": v(-99.38, -22.74) * mm});
            skLineSegment(sketch, "E1444", {"start": v(-99.38, -22.74) * mm, "end": v(-101, -21.92) * mm});
            skLineSegment(sketch, "E1445", {"start": v(-101, -21.92) * mm, "end": v(-101.21, -22.01) * mm});
            skLineSegment(sketch, "E1446", {"start": v(-101.21, -22.01) * mm, "end": v(-101, -22.44) * mm});
            skLineSegment(sketch, "E1447", {"start": v(-101, -22.44) * mm, "end": v(-101.21, -22.82) * mm});
            skLineSegment(sketch, "E1448", {"start": v(-101.21, -22.82) * mm, "end": v(-101.48, -22.92) * mm});
            skLineSegment(sketch, "E1449", {"start": v(-101.48, -22.92) * mm, "end": v(-101.56, -23.25) * mm});
            skLineSegment(sketch, "E1450", {"start": v(-101.56, -23.25) * mm, "end": v(-101.29, -23.47) * mm});
            skLineSegment(sketch, "E1451", {"start": v(-101.29, -23.47) * mm, "end": v(-101.11, -24.14) * mm});
            skLineSegment(sketch, "E1452", {"start": v(-101.11, -24.14) * mm, "end": v(-101.16, -24.86) * mm});
            skLineSegment(sketch, "E1453", {"start": v(-101.16, -24.86) * mm, "end": v(-100.65, -25.22) * mm});
            skLineSegment(sketch, "E1454", {"start": v(-100.65, -25.22) * mm, "end": v(-100, -24.5) * mm});
            skLineSegment(sketch, "E1455", {"start": v(-100, -24.5) * mm, "end": v(-99.67, -24.28) * mm});
            skLineSegment(sketch, "E1456", {"start": v(-58.46, 0.03) * mm, "end": v(-58.46, 0.03) * mm});
            skLineSegment(sketch, "E1457", {"start": v(-118.36, 6.55) * mm, "end": v(-108.8, 4.95) * mm});
            skArc(sketch, "E1458", {"start": v(-108.8, 4.95) * mm, "mid": v(-103.03, 4.15) * mm, "end": v(-97.23, 3.7) * mm});
            skLineSegment(sketch, "E1459", {"start": v(-95.44, 3.58) * mm, "end": v(-94.98, 10.98) * mm});
            skLineSegment(sketch, "E1460", {"start": v(-97.23, 3.7) * mm, "end": v(-95.44, 3.58) * mm});
            skLineSegment(sketch, "E1461", {"start": v(-95.44, 3.58) * mm, "end": v(-84.54, 3.23) * mm});
            skLineSegment(sketch, "E1462", {"start": v(-84.54, 3.23) * mm, "end": v(-81.2, 3.21) * mm});
            skLineSegment(sketch, "E1463", {"start": v(-107.57, 14.71) * mm, "end": v(-102.5, 14.07) * mm});
            skLineSegment(sketch, "E1464", {"start": v(-102.5, 14.07) * mm, "end": v(-98.46, 13.7) * mm});
            skLineSegment(sketch, "E1465", {"start": v(-98.46, 13.7) * mm, "end": v(-94.83, 13.4) * mm});
            skLineSegment(sketch, "E1466", {"start": v(-98.07, 18.57) * mm, "end": v(-98.46, 13.7) * mm});
            skLineSegment(sketch, "E1467", {"start": v(-98.07, 18.57) * mm, "end": v(-97.69, 23.43) * mm});
            skLineSegment(sketch, "E1468", {"start": v(-115.14, -24.88) * mm, "end": v(-115.22, -25.24) * mm});
            skSolve(sketch);
        }
        {
            var Q0;
            Q0=makeQuery(id+"F0.imprint","IMPRINT",FACE,{"disambiguationData":[TD([[makeQuery(id+"F0.imprint","IMPRINT",EDGE,{"derivedFrom":sQuery(id+"F0.wireOp",EDGE,"E21")}),1.0]])]});
            extrude(context, id + "F1", {"entities" : qUnion([Q0]), "depth" : 5.32 * mm, "offsetDistance" : 25.4 * mm});
        }
    });
